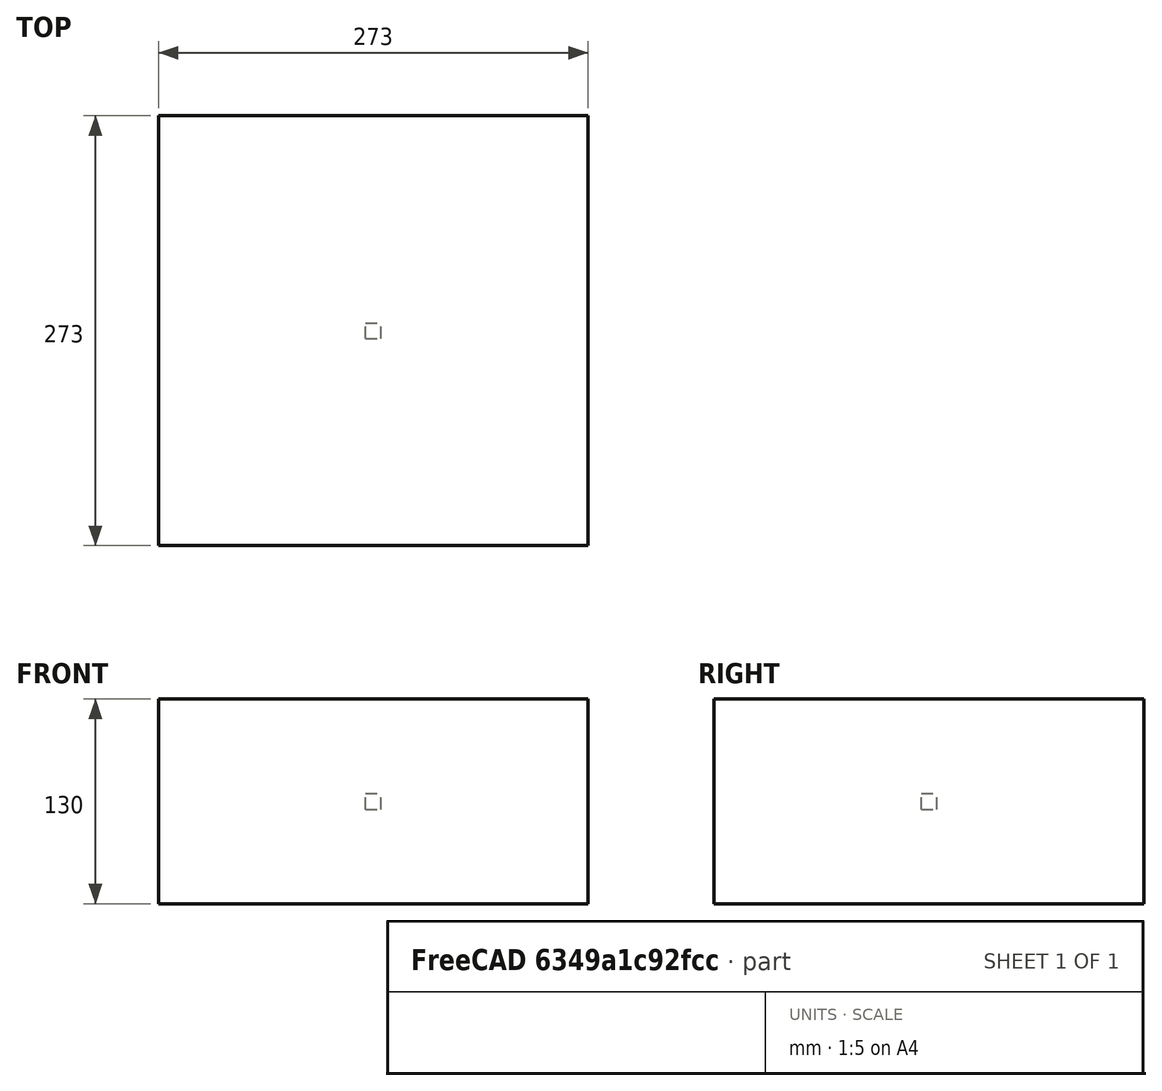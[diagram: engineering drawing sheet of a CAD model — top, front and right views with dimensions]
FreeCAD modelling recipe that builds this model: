
FCSTD DOCUMENT  (FreeCAD 1.0R39109 (Git))
Label: polarArray
License: All rights reserved
LicenseURL: http://en.wikipedia.org/wiki/All_rights_reserved
objects: App::DocumentObjectGroupPython×1251, Part::FeaturePython×3, App::Part×3
note: 2 computed .brp shape members not serialized (recipe doc carries the construction recipe); baked Part::Feature solids carry a one-line shape summary decoded from their .brp

FEATURE [App::DocumentObjectGroupPython] HALFPI  # scripted group (container) (typed FeaturePython)
  name = HALFPI
  value = pi/2.
FEATURE [App::DocumentObjectGroupPython] PI  # scripted group (container) (typed FeaturePython)
  name = PI
  value = 1.*pi
FEATURE [App::DocumentObjectGroupPython] TWOPI  # scripted group (container) (typed FeaturePython)
  name = TWOPI
  value = 2.*pi
FEATURE [App::DocumentObjectGroupPython] Constants  # scripted group (container) (typed FeaturePython)
  Group = -> [HALFPI,PI,TWOPI]
FEATURE [App::DocumentObjectGroupPython] Variables  # scripted group (container) (typed FeaturePython)
FEATURE [App::DocumentObjectGroupPython] Quantities  # scripted group (container) (typed FeaturePython)
FEATURE [App::DocumentObjectGroupPython] Isotopes  # scripted group (container) (typed FeaturePython)
FEATURE [App::DocumentObjectGroupPython] Elements  # scripted group (container) (typed FeaturePython)
FEATURE [App::DocumentObjectGroupPython] Matrix  # scripted group (container) (typed FeaturePython)
FEATURE [App::DocumentObjectGroupPython] Surfaces  # scripted group (container) (typed FeaturePython)
FEATURE [App::DocumentObjectGroupPython] Opticals  # scripted group (container) (typed FeaturePython)
  Group = -> [Matrix,Surfaces]
FEATURE [App::DocumentObjectGroupPython] G4Isotopes  # scripted group (container) (typed FeaturePython)
FEATURE [App::DocumentObjectGroupPython] H_element  # scripted group (container) (typed FeaturePython)
  Z = 1
  atom_value = 1.008
  formula = H
  name = H_element
FEATURE [App::DocumentObjectGroupPython] He_element  # scripted group (container) (typed FeaturePython)
  Z = 2
  atom_value = 4.0026
  formula = He
  name = He_element
FEATURE [App::DocumentObjectGroupPython] Li_element  # scripted group (container) (typed FeaturePython)
  Z = 3
  atom_value = 6.94
  formula = Li
  name = Li_element
FEATURE [App::DocumentObjectGroupPython] Be_element  # scripted group (container) (typed FeaturePython)
  Z = 4
  atom_value = 9.01218
  formula = Be
  name = Be_element
FEATURE [App::DocumentObjectGroupPython] B_element  # scripted group (container) (typed FeaturePython)
  Z = 5
  atom_value = 10.81
  formula = B
  name = B_element
FEATURE [App::DocumentObjectGroupPython] C_element  # scripted group (container) (typed FeaturePython)
  Z = 6
  atom_value = 12.011
  formula = C
  name = C_element
FEATURE [App::DocumentObjectGroupPython] N_element  # scripted group (container) (typed FeaturePython)
  Z = 7
  atom_value = 14.007
  formula = N
  name = N_element
FEATURE [App::DocumentObjectGroupPython] O_element  # scripted group (container) (typed FeaturePython)
  Z = 8
  atom_value = 15.999
  formula = O
  name = O_element
FEATURE [App::DocumentObjectGroupPython] F_element  # scripted group (container) (typed FeaturePython)
  Z = 9
  atom_value = 18.9984
  formula = F
  name = F_element
FEATURE [App::DocumentObjectGroupPython] Ne_element  # scripted group (container) (typed FeaturePython)
  Z = 10
  atom_value = 20.1797
  formula = Ne
  name = Ne_element
FEATURE [App::DocumentObjectGroupPython] Na_element  # scripted group (container) (typed FeaturePython)
  Z = 11
  atom_value = 22.9898
  formula = Na
  name = Na_element
FEATURE [App::DocumentObjectGroupPython] Mg_element  # scripted group (container) (typed FeaturePython)
  Z = 12
  atom_value = 24.305
  formula = Mg
  name = Mg_element
FEATURE [App::DocumentObjectGroupPython] Al_element  # scripted group (container) (typed FeaturePython)
  Z = 13
  atom_value = 26.9815
  formula = Al
  name = Al_element
FEATURE [App::DocumentObjectGroupPython] Si_element  # scripted group (container) (typed FeaturePython)
  Z = 14
  atom_value = 28.085
  formula = Si
  name = Si_element
FEATURE [App::DocumentObjectGroupPython] P_element  # scripted group (container) (typed FeaturePython)
  Z = 15
  atom_value = 30.9738
  formula = P
  name = P_element
FEATURE [App::DocumentObjectGroupPython] S_element  # scripted group (container) (typed FeaturePython)
  Z = 16
  atom_value = 32.06
  formula = S
  name = S_element
FEATURE [App::DocumentObjectGroupPython] Cl_element  # scripted group (container) (typed FeaturePython)
  Z = 17
  atom_value = 35.45
  formula = Cl
  name = Cl_element
FEATURE [App::DocumentObjectGroupPython] Ar_element  # scripted group (container) (typed FeaturePython)
  Z = 18
  atom_value = 39.95
  formula = Ar
  name = Ar_element
FEATURE [App::DocumentObjectGroupPython] K_element  # scripted group (container) (typed FeaturePython)
  Z = 19
  atom_value = 39.0983
  formula = K
  name = K_element
FEATURE [App::DocumentObjectGroupPython] Ca_element  # scripted group (container) (typed FeaturePython)
  Z = 20
  atom_value = 40.078
  formula = Ca
  name = Ca_element
FEATURE [App::DocumentObjectGroupPython] Sc_element  # scripted group (container) (typed FeaturePython)
  Z = 21
  atom_value = 44.9559
  formula = Sc
  name = Sc_element
FEATURE [App::DocumentObjectGroupPython] Ti_element  # scripted group (container) (typed FeaturePython)
  Z = 22
  atom_value = 47.867
  formula = Ti
  name = Ti_element
FEATURE [App::DocumentObjectGroupPython] V_element  # scripted group (container) (typed FeaturePython)
  Z = 23
  atom_value = 50.9415
  formula = V
  name = V_element
FEATURE [App::DocumentObjectGroupPython] Cr_element  # scripted group (container) (typed FeaturePython)
  Z = 24
  atom_value = 51.9961
  formula = Cr
  name = Cr_element
FEATURE [App::DocumentObjectGroupPython] Mn_element  # scripted group (container) (typed FeaturePython)
  Z = 25
  atom_value = 54.938
  formula = Mn
  name = Mn_element
FEATURE [App::DocumentObjectGroupPython] Fe_element  # scripted group (container) (typed FeaturePython)
  Z = 26
  atom_value = 55.845
  formula = Fe
  name = Fe_element
FEATURE [App::DocumentObjectGroupPython] Co_element  # scripted group (container) (typed FeaturePython)
  Z = 27
  atom_value = 58.9332
  formula = Co
  name = Co_element
FEATURE [App::DocumentObjectGroupPython] Ni_element  # scripted group (container) (typed FeaturePython)
  Z = 28
  atom_value = 58.6934
  formula = Ni
  name = Ni_element
FEATURE [App::DocumentObjectGroupPython] Cu_element  # scripted group (container) (typed FeaturePython)
  Z = 29
  atom_value = 63.546
  formula = Cu
  name = Cu_element
FEATURE [App::DocumentObjectGroupPython] Zn_element  # scripted group (container) (typed FeaturePython)
  Z = 30
  atom_value = 65.38
  formula = Zn
  name = Zn_element
FEATURE [App::DocumentObjectGroupPython] Ga_element  # scripted group (container) (typed FeaturePython)
  Z = 31
  atom_value = 69.723
  formula = Ga
  name = Ga_element
FEATURE [App::DocumentObjectGroupPython] Ge_element  # scripted group (container) (typed FeaturePython)
  Z = 32
  atom_value = 72.63
  formula = Ge
  name = Ge_element
FEATURE [App::DocumentObjectGroupPython] As_element  # scripted group (container) (typed FeaturePython)
  Z = 33
  atom_value = 74.9216
  formula = As
  name = As_element
FEATURE [App::DocumentObjectGroupPython] Se_element  # scripted group (container) (typed FeaturePython)
  Z = 34
  atom_value = 78.971
  formula = Se
  name = Se_element
FEATURE [App::DocumentObjectGroupPython] Br_element  # scripted group (container) (typed FeaturePython)
  Z = 35
  atom_value = 79.904
  formula = Br
  name = Br_element
FEATURE [App::DocumentObjectGroupPython] Kr_element  # scripted group (container) (typed FeaturePython)
  Z = 36
  atom_value = 83.798
  formula = Kr
  name = Kr_element
FEATURE [App::DocumentObjectGroupPython] Rb_element  # scripted group (container) (typed FeaturePython)
  Z = 37
  atom_value = 85.4678
  formula = Rb
  name = Rb_element
FEATURE [App::DocumentObjectGroupPython] Sr_element  # scripted group (container) (typed FeaturePython)
  Z = 38
  atom_value = 87.62
  formula = Sr
  name = Sr_element
FEATURE [App::DocumentObjectGroupPython] Y_element  # scripted group (container) (typed FeaturePython)
  Z = 39
  atom_value = 88.9058
  formula = Y
  name = Y_element
FEATURE [App::DocumentObjectGroupPython] Zr_element  # scripted group (container) (typed FeaturePython)
  Z = 40
  atom_value = 91.224
  formula = Zr
  name = Zr_element
FEATURE [App::DocumentObjectGroupPython] Nb_element  # scripted group (container) (typed FeaturePython)
  Z = 41
  atom_value = 92.9064
  formula = Nb
  name = Nb_element
FEATURE [App::DocumentObjectGroupPython] Mo_element  # scripted group (container) (typed FeaturePython)
  Z = 42
  atom_value = 95.95
  formula = Mo
  name = Mo_element
FEATURE [App::DocumentObjectGroupPython] Tc_element  # scripted group (container) (typed FeaturePython)
  Z = 43
  atom_value = 97
  formula = Tc
  name = Tc_element
FEATURE [App::DocumentObjectGroupPython] Ru_element  # scripted group (container) (typed FeaturePython)
  Z = 44
  atom_value = 101.07
  formula = Ru
  name = Ru_element
FEATURE [App::DocumentObjectGroupPython] Rh_element  # scripted group (container) (typed FeaturePython)
  Z = 45
  atom_value = 102.905
  formula = Rh
  name = Rh_element
FEATURE [App::DocumentObjectGroupPython] Pd_element  # scripted group (container) (typed FeaturePython)
  Z = 46
  atom_value = 106.42
  formula = Pd
  name = Pd_element
FEATURE [App::DocumentObjectGroupPython] Ag_element  # scripted group (container) (typed FeaturePython)
  Z = 47
  atom_value = 107.868
  formula = Ag
  name = Ag_element
FEATURE [App::DocumentObjectGroupPython] Cd_element  # scripted group (container) (typed FeaturePython)
  Z = 48
  atom_value = 112.414
  formula = Cd
  name = Cd_element
FEATURE [App::DocumentObjectGroupPython] In_element  # scripted group (container) (typed FeaturePython)
  Z = 49
  atom_value = 114.818
  formula = In
  name = In_element
FEATURE [App::DocumentObjectGroupPython] Sn_element  # scripted group (container) (typed FeaturePython)
  Z = 50
  atom_value = 118.71
  formula = Sn
  name = Sn_element
FEATURE [App::DocumentObjectGroupPython] Sb_element  # scripted group (container) (typed FeaturePython)
  Z = 51
  atom_value = 121.76
  formula = Sb
  name = Sb_element
FEATURE [App::DocumentObjectGroupPython] Te_element  # scripted group (container) (typed FeaturePython)
  Z = 52
  atom_value = 127.6
  formula = Te
  name = Te_element
FEATURE [App::DocumentObjectGroupPython] I_element  # scripted group (container) (typed FeaturePython)
  Z = 53
  atom_value = 126.904
  formula = I
  name = I_element
FEATURE [App::DocumentObjectGroupPython] Xe_element  # scripted group (container) (typed FeaturePython)
  Z = 54
  atom_value = 131.293
  formula = Xe
  name = Xe_element
FEATURE [App::DocumentObjectGroupPython] Cs_element  # scripted group (container) (typed FeaturePython)
  Z = 55
  atom_value = 132.905
  formula = Cs
  name = Cs_element
FEATURE [App::DocumentObjectGroupPython] Ba_element  # scripted group (container) (typed FeaturePython)
  Z = 56
  atom_value = 137.327
  formula = Ba
  name = Ba_element
FEATURE [App::DocumentObjectGroupPython] La_element  # scripted group (container) (typed FeaturePython)
  Z = 57
  atom_value = 138.905
  formula = La
  name = La_element
FEATURE [App::DocumentObjectGroupPython] Ce_element  # scripted group (container) (typed FeaturePython)
  Z = 58
  atom_value = 140.116
  formula = Ce
  name = Ce_element
FEATURE [App::DocumentObjectGroupPython] Pr_element  # scripted group (container) (typed FeaturePython)
  Z = 59
  atom_value = 140.908
  formula = Pr
  name = Pr_element
FEATURE [App::DocumentObjectGroupPython] Nd_element  # scripted group (container) (typed FeaturePython)
  Z = 60
  atom_value = 144.242
  formula = Nd
  name = Nd_element
FEATURE [App::DocumentObjectGroupPython] Pm_element  # scripted group (container) (typed FeaturePython)
  Z = 61
  atom_value = 145
  formula = Pm
  name = Pm_element
FEATURE [App::DocumentObjectGroupPython] Sm_element  # scripted group (container) (typed FeaturePython)
  Z = 62
  atom_value = 150.36
  formula = Sm
  name = Sm_element
FEATURE [App::DocumentObjectGroupPython] Eu_element  # scripted group (container) (typed FeaturePython)
  Z = 63
  atom_value = 151.964
  formula = Eu
  name = Eu_element
FEATURE [App::DocumentObjectGroupPython] Gd_element  # scripted group (container) (typed FeaturePython)
  Z = 64
  atom_value = 157.25
  formula = Gd
  name = Gd_element
FEATURE [App::DocumentObjectGroupPython] Tb_element  # scripted group (container) (typed FeaturePython)
  Z = 65
  atom_value = 158.925
  formula = Tb
  name = Tb_element
FEATURE [App::DocumentObjectGroupPython] Dy_element  # scripted group (container) (typed FeaturePython)
  Z = 66
  atom_value = 162.5
  formula = Dy
  name = Dy_element
FEATURE [App::DocumentObjectGroupPython] Ho_element  # scripted group (container) (typed FeaturePython)
  Z = 67
  atom_value = 164.93
  formula = Ho
  name = Ho_element
FEATURE [App::DocumentObjectGroupPython] Er_element  # scripted group (container) (typed FeaturePython)
  Z = 68
  atom_value = 167.259
  formula = Er
  name = Er_element
FEATURE [App::DocumentObjectGroupPython] Tm_element  # scripted group (container) (typed FeaturePython)
  Z = 69
  atom_value = 168.934
  formula = Tm
  name = Tm_element
FEATURE [App::DocumentObjectGroupPython] Yb_element  # scripted group (container) (typed FeaturePython)
  Z = 70
  atom_value = 173.045
  formula = Yb
  name = Yb_element
FEATURE [App::DocumentObjectGroupPython] Lu_element  # scripted group (container) (typed FeaturePython)
  Z = 71
  atom_value = 174.967
  formula = Lu
  name = Lu_element
FEATURE [App::DocumentObjectGroupPython] Hf_element  # scripted group (container) (typed FeaturePython)
  Z = 72
  atom_value = 178.49
  formula = Hf
  name = Hf_element
FEATURE [App::DocumentObjectGroupPython] Ta_element  # scripted group (container) (typed FeaturePython)
  Z = 73
  atom_value = 180.948
  formula = Ta
  name = Ta_element
FEATURE [App::DocumentObjectGroupPython] W_element  # scripted group (container) (typed FeaturePython)
  Z = 74
  atom_value = 183.84
  formula = W
  name = W_element
FEATURE [App::DocumentObjectGroupPython] Re_element  # scripted group (container) (typed FeaturePython)
  Z = 75
  atom_value = 186.207
  formula = Re
  name = Re_element
FEATURE [App::DocumentObjectGroupPython] Os_element  # scripted group (container) (typed FeaturePython)
  Z = 76
  atom_value = 190.23
  formula = Os
  name = Os_element
FEATURE [App::DocumentObjectGroupPython] Ir_element  # scripted group (container) (typed FeaturePython)
  Z = 77
  atom_value = 192.217
  formula = Ir
  name = Ir_element
FEATURE [App::DocumentObjectGroupPython] Pt_element  # scripted group (container) (typed FeaturePython)
  Z = 78
  atom_value = 195.084
  formula = Pt
  name = Pt_element
FEATURE [App::DocumentObjectGroupPython] Au_element  # scripted group (container) (typed FeaturePython)
  Z = 79
  atom_value = 196.967
  formula = Au
  name = Au_element
FEATURE [App::DocumentObjectGroupPython] Hg_element  # scripted group (container) (typed FeaturePython)
  Z = 80
  atom_value = 200.592
  formula = Hg
  name = Hg_element
FEATURE [App::DocumentObjectGroupPython] Tl_element  # scripted group (container) (typed FeaturePython)
  Z = 81
  atom_value = 204.38
  formula = Tl
  name = Tl_element
FEATURE [App::DocumentObjectGroupPython] Pb_element  # scripted group (container) (typed FeaturePython)
  Z = 82
  atom_value = 207.2
  formula = Pb
  name = Pb_element
FEATURE [App::DocumentObjectGroupPython] Bi_element  # scripted group (container) (typed FeaturePython)
  Z = 83
  atom_value = 208.98
  formula = Bi
  name = Bi_element
FEATURE [App::DocumentObjectGroupPython] Po_element  # scripted group (container) (typed FeaturePython)
  Z = 84
  atom_value = 209
  formula = Po
  name = Po_element
FEATURE [App::DocumentObjectGroupPython] At_element  # scripted group (container) (typed FeaturePython)
  Z = 85
  atom_value = 210
  formula = At
  name = At_element
FEATURE [App::DocumentObjectGroupPython] Rn_element  # scripted group (container) (typed FeaturePython)
  Z = 86
  atom_value = 222
  formula = Rn
  name = Rn_element
FEATURE [App::DocumentObjectGroupPython] Fr_element  # scripted group (container) (typed FeaturePython)
  Z = 87
  atom_value = 223
  formula = Fr
  name = Fr_element
FEATURE [App::DocumentObjectGroupPython] Ra_element  # scripted group (container) (typed FeaturePython)
  Z = 88
  atom_value = 226
  formula = Ra
  name = Ra_element
FEATURE [App::DocumentObjectGroupPython] Ac_element  # scripted group (container) (typed FeaturePython)
  Z = 89
  atom_value = 227
  formula = Ac
  name = Ac_element
FEATURE [App::DocumentObjectGroupPython] Th_element  # scripted group (container) (typed FeaturePython)
  Z = 90
  atom_value = 232.038
  formula = Th
  name = Th_element
FEATURE [App::DocumentObjectGroupPython] Pa_element  # scripted group (container) (typed FeaturePython)
  Z = 91
  atom_value = 231.036
  formula = Pa
  name = Pa_element
FEATURE [App::DocumentObjectGroupPython] U_element  # scripted group (container) (typed FeaturePython)
  Z = 92
  atom_value = 238.029
  formula = U
  name = U_element
FEATURE [App::DocumentObjectGroupPython] Np_element  # scripted group (container) (typed FeaturePython)
  Z = 93
  atom_value = 237
  formula = Np
  name = Np_element
FEATURE [App::DocumentObjectGroupPython] Pu_element  # scripted group (container) (typed FeaturePython)
  Z = 94
  atom_value = 244
  formula = Pu
  name = Pu_element
FEATURE [App::DocumentObjectGroupPython] Am_element  # scripted group (container) (typed FeaturePython)
  Z = 95
  atom_value = 243
  formula = Am
  name = Am_element
FEATURE [App::DocumentObjectGroupPython] Cm_element  # scripted group (container) (typed FeaturePython)
  Z = 96
  atom_value = 247
  formula = Cm
  name = Cm_element
FEATURE [App::DocumentObjectGroupPython] Bk_element  # scripted group (container) (typed FeaturePython)
  Z = 97
  atom_value = 247
  formula = Bk
  name = Bk_element
FEATURE [App::DocumentObjectGroupPython] Cf_element  # scripted group (container) (typed FeaturePython)
  Z = 98
  atom_value = 251
  formula = Cf
  name = Cf_element
FEATURE [App::DocumentObjectGroupPython] G4Elements  # scripted group (container) (typed FeaturePython)
  Group = -> [H_element,He_element,Li_element,Be_element,B_element,C_element,N_element,O_element,F_element,Ne_element,Na_element,Mg_element,Al_element,Si_element,P_element,S_element,Cl_element,Ar_element,K_element,Ca_element,Sc_element,Ti_element,V_element,Cr_element,Mn_element,Fe_element,Co_element,Ni_element,Cu_element,Zn_element,Ga_element,Ge_element,As_element,Se_element,Br_element,Kr_element,Rb_element,+61 more]
FEATURE [App::DocumentObjectGroupPython] H_element001  label="H_element : 0.101"  # scripted group (container) (typed FeaturePython)
  n = 0.101327
FEATURE [App::DocumentObjectGroupPython] C_element001  label="C_element : 0.775"  # scripted group (container) (typed FeaturePython)
  n = 0.7755
FEATURE [App::DocumentObjectGroupPython] N_element001  label="N_element : 0.035"  # scripted group (container) (typed FeaturePython)
  n = 0.035057
FEATURE [App::DocumentObjectGroupPython] O_element001  label="O_element : 0.052"  # scripted group (container) (typed FeaturePython)
  n = 0.0523159
FEATURE [App::DocumentObjectGroupPython] F_element001  label="F_element : 0.017"  # scripted group (container) (typed FeaturePython)
  n = 0.017422
FEATURE [App::DocumentObjectGroupPython] Ca_element001  label="Ca_element : 0.018"  # scripted group (container) (typed FeaturePython)
  n = 0.018378
FEATURE [App::DocumentObjectGroupPython] G4_A_150_TISSUE  label="G4_A-150_TISSUE"  # scripted group (container) (typed FeaturePython)
  Dunit = g/cm3
  Dvalue = 1.127
  Group = -> [H_element001,C_element001,N_element001,O_element001,F_element001,Ca_element001]
  conduct = 2
  density = 1
  expand = 3
  formula = G4_A-150_TISSUE
  name = G4_A-150_TISSUE
  specific = 4
FEATURE [App::DocumentObjectGroupPython] C_element002  label="C_element : 3"  # scripted group (container) (typed FeaturePython)
  n = 3
  ref = C_element
FEATURE [App::DocumentObjectGroupPython] H_element002  label="H_element : 6"  # scripted group (container) (typed FeaturePython)
  n = 6
  ref = H_element
FEATURE [App::DocumentObjectGroupPython] O_element002  label="O_element : 1"  # scripted group (container) (typed FeaturePython)
  n = 1
  ref = O_element
FEATURE [App::DocumentObjectGroupPython] G4_ACETONE  # scripted group (container) (typed FeaturePython)
  Dunit = g/cm3
  Dvalue = 0.7899
  Group = -> [C_element002,H_element002,O_element002]
  conduct = 2
  density = 1
  expand = 3
  formula = G4_ACETONE
  name = G4_ACETONE
  specific = 4
FEATURE [App::DocumentObjectGroupPython] C_element003  label="C_element : 2"  # scripted group (container) (typed FeaturePython)
  n = 2
  ref = C_element
FEATURE [App::DocumentObjectGroupPython] H_element003  label="H_element : 2"  # scripted group (container) (typed FeaturePython)
  n = 2
  ref = H_element
FEATURE [App::DocumentObjectGroupPython] G4_ACETYLENE  # scripted group (container) (typed FeaturePython)
  Dunit = g/cm3
  Dvalue = 0.0010967
  Group = -> [C_element003,H_element003]
  conduct = 2
  density = 1
  expand = 3
  formula = G4_ACETYLENE
  name = G4_ACETYLENE
  specific = 4
FEATURE [App::DocumentObjectGroupPython] C_element004  label="C_element : 5"  # scripted group (container) (typed FeaturePython)
  n = 5
  ref = C_element
FEATURE [App::DocumentObjectGroupPython] H_element004  label="H_element : 5"  # scripted group (container) (typed FeaturePython)
  n = 5
  ref = H_element
FEATURE [App::DocumentObjectGroupPython] N_element002  label="N_element : 5"  # scripted group (container) (typed FeaturePython)
  n = 5
  ref = N_element
FEATURE [App::DocumentObjectGroupPython] G4_ADENINE  # scripted group (container) (typed FeaturePython)
  Dunit = g/cm3
  Dvalue = 1.6
  Group = -> [C_element004,H_element004,N_element002]
  conduct = 2
  density = 1
  expand = 3
  formula = G4_ADENINE
  name = G4_ADENINE
  specific = 4
FEATURE [App::DocumentObjectGroupPython] H_element005  label="H_element : 0.114"  # scripted group (container) (typed FeaturePython)
  n = 0.114
FEATURE [App::DocumentObjectGroupPython] C_element005  label="C_element : 0.598"  # scripted group (container) (typed FeaturePython)
  n = 0.598
FEATURE [App::DocumentObjectGroupPython] N_element003  label="N_element : 0.007"  # scripted group (container) (typed FeaturePython)
  n = 0.007
FEATURE [App::DocumentObjectGroupPython] O_element003  label="O_element : 0.278"  # scripted group (container) (typed FeaturePython)
  n = 0.278
FEATURE [App::DocumentObjectGroupPython] Na_element001  label="Na_element : 0.001"  # scripted group (container) (typed FeaturePython)
  n = 0.001
FEATURE [App::DocumentObjectGroupPython] S_element001  label="S_element : 0.001"  # scripted group (container) (typed FeaturePython)
  n = 0.001
FEATURE [App::DocumentObjectGroupPython] Cl_element001  label="Cl_element : 0.001"  # scripted group (container) (typed FeaturePython)
  n = 0.001
FEATURE [App::DocumentObjectGroupPython] G4_ADIPOSE_TISSUE_ICRP  # scripted group (container) (typed FeaturePython)
  Dunit = g/cm3
  Dvalue = 0.95
  Group = -> [H_element005,C_element005,N_element003,O_element003,Na_element001,S_element001,Cl_element001]
  conduct = 2
  density = 1
  expand = 3
  formula = G4_ADIPOSE_TISSUE_ICRP
  name = G4_ADIPOSE_TISSUE_ICRP
  specific = 4
FEATURE [App::DocumentObjectGroupPython] C_element006  label="C_element : 0.000"  # scripted group (container) (typed FeaturePython)
  n = 0.000124
FEATURE [App::DocumentObjectGroupPython] N_element004  label="N_element : 0.755"  # scripted group (container) (typed FeaturePython)
  n = 0.755268
FEATURE [App::DocumentObjectGroupPython] O_element004  label="O_element : 0.232"  # scripted group (container) (typed FeaturePython)
  n = 0.231781
FEATURE [App::DocumentObjectGroupPython] Ar_element001  label="Ar_element : 0.013"  # scripted group (container) (typed FeaturePython)
  n = 0.012827
FEATURE [App::DocumentObjectGroupPython] G4_AIR  # scripted group (container) (typed FeaturePython)
  Dunit = g/cm3
  Dvalue = 0.00120479
  Group = -> [C_element006,N_element004,O_element004,Ar_element001]
  conduct = 2
  density = 1
  expand = 3
  formula = G4_AIR
  name = G4_AIR
  specific = 4
FEATURE [App::DocumentObjectGroupPython] C_element007  label="C_element : 006"  # scripted group (container) (typed FeaturePython)
  n = 3
  ref = C_element
FEATURE [App::DocumentObjectGroupPython] H_element006  label="H_element : 7"  # scripted group (container) (typed FeaturePython)
  n = 7
  ref = H_element
FEATURE [App::DocumentObjectGroupPython] N_element005  label="N_element : 1"  # scripted group (container) (typed FeaturePython)
  n = 1
  ref = N_element
FEATURE [App::DocumentObjectGroupPython] O_element005  label="O_element : 2"  # scripted group (container) (typed FeaturePython)
  n = 2
  ref = O_element
FEATURE [App::DocumentObjectGroupPython] G4_ALANINE  # scripted group (container) (typed FeaturePython)
  Dunit = g/cm3
  Dvalue = 1.42
  Group = -> [C_element007,H_element006,N_element005,O_element005]
  conduct = 2
  density = 1
  expand = 3
  formula = G4_ALANINE
  name = G4_ALANINE
  specific = 4
FEATURE [App::DocumentObjectGroupPython] Al_element001  label="Al_element : 2"  # scripted group (container) (typed FeaturePython)
  n = 2
  ref = Al_element
FEATURE [App::DocumentObjectGroupPython] O_element006  label="O_element : 3"  # scripted group (container) (typed FeaturePython)
  n = 3
  ref = O_element
FEATURE [App::DocumentObjectGroupPython] G4_ALUMINUM_OXIDE  # scripted group (container) (typed FeaturePython)
  Dunit = g/cm3
  Dvalue = 3.97
  Group = -> [Al_element001,O_element006]
  conduct = 2
  density = 1
  expand = 3
  formula = G4_ALUMINUM_OXIDE
  name = G4_ALUMINUM_OXIDE
  specific = 4
FEATURE [App::DocumentObjectGroupPython] H_element007  label="H_element : 0.106"  # scripted group (container) (typed FeaturePython)
  n = 0.10593
FEATURE [App::DocumentObjectGroupPython] C_element008  label="C_element : 0.789"  # scripted group (container) (typed FeaturePython)
  n = 0.788974
FEATURE [App::DocumentObjectGroupPython] O_element007  label="O_element : 0.105"  # scripted group (container) (typed FeaturePython)
  n = 0.105096
FEATURE [App::DocumentObjectGroupPython] G4_AMBER  # scripted group (container) (typed FeaturePython)
  Dunit = g/cm3
  Dvalue = 1.1
  Group = -> [H_element007,C_element008,O_element007]
  conduct = 2
  density = 1
  expand = 3
  formula = G4_AMBER
  name = G4_AMBER
  specific = 4
FEATURE [App::DocumentObjectGroupPython] N_element006  label="N_element : 006"  # scripted group (container) (typed FeaturePython)
  n = 1
  ref = N_element
FEATURE [App::DocumentObjectGroupPython] H_element008  label="H_element : 3"  # scripted group (container) (typed FeaturePython)
  n = 3
  ref = H_element
FEATURE [App::DocumentObjectGroupPython] G4_AMMONIA  # scripted group (container) (typed FeaturePython)
  Dunit = g/cm3
  Dvalue = 0.000826019
  Group = -> [N_element006,H_element008]
  conduct = 2
  density = 1
  expand = 3
  formula = G4_AMMONIA
  name = G4_AMMONIA
  specific = 4
FEATURE [App::DocumentObjectGroupPython] C_element009  label="C_element : 6"  # scripted group (container) (typed FeaturePython)
  n = 6
  ref = C_element
FEATURE [App::DocumentObjectGroupPython] H_element009  label="H_element : 008"  # scripted group (container) (typed FeaturePython)
  n = 7
  ref = H_element
FEATURE [App::DocumentObjectGroupPython] N_element007  label="N_element : 007"  # scripted group (container) (typed FeaturePython)
  n = 1
  ref = N_element
FEATURE [App::DocumentObjectGroupPython] G4_ANILINE  # scripted group (container) (typed FeaturePython)
  Dunit = g/cm3
  Dvalue = 1.0235
  Group = -> [C_element009,H_element009,N_element007]
  conduct = 2
  density = 1
  expand = 3
  formula = G4_ANILINE
  name = G4_ANILINE
  specific = 4
FEATURE [App::DocumentObjectGroupPython] C_element010  label="C_element : 14"  # scripted group (container) (typed FeaturePython)
  n = 14
  ref = C_element
FEATURE [App::DocumentObjectGroupPython] H_element010  label="H_element : 10"  # scripted group (container) (typed FeaturePython)
  n = 10
  ref = H_element
FEATURE [App::DocumentObjectGroupPython] G4_ANTHRACENE  # scripted group (container) (typed FeaturePython)
  Dunit = g/cm3
  Dvalue = 1.283
  Group = -> [C_element010,H_element010]
  conduct = 2
  density = 1
  expand = 3
  formula = G4_ANTHRACENE
  name = G4_ANTHRACENE
  specific = 4
FEATURE [App::DocumentObjectGroupPython] H_element011  label="H_element : 0.065"  # scripted group (container) (typed FeaturePython)
  n = 0.0654709
FEATURE [App::DocumentObjectGroupPython] C_element011  label="C_element : 0.537"  # scripted group (container) (typed FeaturePython)
  n = 0.536944
FEATURE [App::DocumentObjectGroupPython] N_element008  label="N_element : 0.021"  # scripted group (container) (typed FeaturePython)
  n = 0.0215
FEATURE [App::DocumentObjectGroupPython] O_element008  label="O_element : 0.032"  # scripted group (container) (typed FeaturePython)
  n = 0.032085
FEATURE [App::DocumentObjectGroupPython] F_element002  label="F_element : 0.167"  # scripted group (container) (typed FeaturePython)
  n = 0.167411
FEATURE [App::DocumentObjectGroupPython] Ca_element002  label="Ca_element : 0.177"  # scripted group (container) (typed FeaturePython)
  n = 0.176589
FEATURE [App::DocumentObjectGroupPython] G4_B_100_BONE  label="G4_B-100_BONE"  # scripted group (container) (typed FeaturePython)
  Dunit = g/cm3
  Dvalue = 1.45
  Group = -> [H_element011,C_element011,N_element008,O_element008,F_element002,Ca_element002]
  conduct = 2
  density = 1
  expand = 3
  formula = G4_B-100_BONE
  name = G4_B-100_BONE
  specific = 4
FEATURE [App::DocumentObjectGroupPython] H_element012  label="H_element : 0.057"  # scripted group (container) (typed FeaturePython)
  n = 0.057441
FEATURE [App::DocumentObjectGroupPython] C_element012  label="C_element : 0.790"  # scripted group (container) (typed FeaturePython)
  n = 0.774591
FEATURE [App::DocumentObjectGroupPython] O_element009  label="O_element : 0.168"  # scripted group (container) (typed FeaturePython)
  n = 0.167968
FEATURE [App::DocumentObjectGroupPython] G4_BAKELITE  # scripted group (container) (typed FeaturePython)
  Dunit = g/cm3
  Dvalue = 1.25
  Group = -> [H_element012,C_element012,O_element009]
  conduct = 2
  density = 1
  expand = 3
  formula = G4_BAKELITE
  name = G4_BAKELITE
  specific = 4
FEATURE [App::DocumentObjectGroupPython] Ba_element001  label="Ba_element : 1"  # scripted group (container) (typed FeaturePython)
  n = 1
  ref = Ba_element
FEATURE [App::DocumentObjectGroupPython] F_element003  label="F_element : 2"  # scripted group (container) (typed FeaturePython)
  n = 2
  ref = F_element
FEATURE [App::DocumentObjectGroupPython] G4_BARIUM_FLUORIDE  # scripted group (container) (typed FeaturePython)
  Dunit = g/cm3
  Dvalue = 4.89
  Group = -> [Ba_element001,F_element003]
  conduct = 2
  density = 1
  expand = 3
  formula = G4_BARIUM_FLUORIDE
  name = G4_BARIUM_FLUORIDE
  specific = 4
FEATURE [App::DocumentObjectGroupPython] Ba_element002  label="Ba_element : 002"  # scripted group (container) (typed FeaturePython)
  n = 1
  ref = Ba_element
FEATURE [App::DocumentObjectGroupPython] S_element002  label="S_element : 1"  # scripted group (container) (typed FeaturePython)
  n = 1
  ref = S_element
FEATURE [App::DocumentObjectGroupPython] O_element010  label="O_element : 4"  # scripted group (container) (typed FeaturePython)
  n = 4
  ref = O_element
FEATURE [App::DocumentObjectGroupPython] G4_BARIUM_SULFATE  # scripted group (container) (typed FeaturePython)
  Dunit = g/cm3
  Dvalue = 4.5
  Group = -> [Ba_element002,S_element002,O_element010]
  conduct = 2
  density = 1
  expand = 3
  formula = G4_BARIUM_SULFATE
  name = G4_BARIUM_SULFATE
  specific = 4
FEATURE [App::DocumentObjectGroupPython] C_element013  label="C_element : 007"  # scripted group (container) (typed FeaturePython)
  n = 6
  ref = C_element
FEATURE [App::DocumentObjectGroupPython] H_element013  label="H_element : 009"  # scripted group (container) (typed FeaturePython)
  n = 6
  ref = H_element
FEATURE [App::DocumentObjectGroupPython] G4_BENZENE  # scripted group (container) (typed FeaturePython)
  Dunit = g/cm3
  Dvalue = 0.87865
  Group = -> [C_element013,H_element013]
  conduct = 2
  density = 1
  expand = 3
  formula = G4_BENZENE
  name = G4_BENZENE
  specific = 4
FEATURE [App::DocumentObjectGroupPython] Be_element001  label="Be_element : 1"  # scripted group (container) (typed FeaturePython)
  n = 1
  ref = Be_element
FEATURE [App::DocumentObjectGroupPython] O_element011  label="O_element : 005"  # scripted group (container) (typed FeaturePython)
  n = 1
  ref = O_element
FEATURE [App::DocumentObjectGroupPython] G4_BERYLLIUM_OXIDE  # scripted group (container) (typed FeaturePython)
  Dunit = g/cm3
  Dvalue = 3.01
  Group = -> [Be_element001,O_element011]
  conduct = 2
  density = 1
  expand = 3
  formula = G4_BERYLLIUM_OXIDE
  name = G4_BERYLLIUM_OXIDE
  specific = 4
FEATURE [App::DocumentObjectGroupPython] Bi_element001  label="Bi_element : 4"  # scripted group (container) (typed FeaturePython)
  n = 4
  ref = Bi_element
FEATURE [App::DocumentObjectGroupPython] Ge_element001  label="Ge_element : 3"  # scripted group (container) (typed FeaturePython)
  n = 3
  ref = Ge_element
FEATURE [App::DocumentObjectGroupPython] O_element012  label="O_element : 12"  # scripted group (container) (typed FeaturePython)
  n = 12
  ref = O_element
FEATURE [App::DocumentObjectGroupPython] G4_BGO  # scripted group (container) (typed FeaturePython)
  Dunit = g/cm3
  Dvalue = 7.13
  Group = -> [Bi_element001,Ge_element001,O_element012]
  conduct = 2
  density = 1
  expand = 3
  formula = G4_BGO
  name = G4_BGO
  specific = 4
FEATURE [App::DocumentObjectGroupPython] H_element014  label="H_element : 0.102"  # scripted group (container) (typed FeaturePython)
  n = 0.102
FEATURE [App::DocumentObjectGroupPython] C_element014  label="C_element : 0.110"  # scripted group (container) (typed FeaturePython)
  n = 0.11
FEATURE [App::DocumentObjectGroupPython] N_element009  label="N_element : 0.033"  # scripted group (container) (typed FeaturePython)
  n = 0.033
FEATURE [App::DocumentObjectGroupPython] O_element013  label="O_element : 0.745"  # scripted group (container) (typed FeaturePython)
  n = 0.745
FEATURE [App::DocumentObjectGroupPython] Na_element002  label="Na_element : 0.002"  # scripted group (container) (typed FeaturePython)
  n = 0.001
FEATURE [App::DocumentObjectGroupPython] P_element001  label="P_element : 0.001"  # scripted group (container) (typed FeaturePython)
  n = 0.001
FEATURE [App::DocumentObjectGroupPython] S_element003  label="S_element : 0.002"  # scripted group (container) (typed FeaturePython)
  n = 0.002
FEATURE [App::DocumentObjectGroupPython] Cl_element002  label="Cl_element : 0.003"  # scripted group (container) (typed FeaturePython)
  n = 0.003
FEATURE [App::DocumentObjectGroupPython] K_element001  label="K_element : 0.002"  # scripted group (container) (typed FeaturePython)
  n = 0.002
FEATURE [App::DocumentObjectGroupPython] Fe_element001  label="Fe_element : 0.001"  # scripted group (container) (typed FeaturePython)
  n = 0.001
FEATURE [App::DocumentObjectGroupPython] G4_BLOOD_ICRP  # scripted group (container) (typed FeaturePython)
  Dunit = g/cm3
  Dvalue = 1.06
  Group = -> [H_element014,C_element014,N_element009,O_element013,Na_element002,P_element001,S_element003,Cl_element002,K_element001,Fe_element001]
  conduct = 2
  density = 1
  expand = 3
  formula = G4_BLOOD_ICRP
  name = G4_BLOOD_ICRP
  specific = 4
FEATURE [App::DocumentObjectGroupPython] H_element015  label="H_element : 0.064"  # scripted group (container) (typed FeaturePython)
  n = 0.064
FEATURE [App::DocumentObjectGroupPython] C_element015  label="C_element : 0.278"  # scripted group (container) (typed FeaturePython)
  n = 0.278
FEATURE [App::DocumentObjectGroupPython] N_element010  label="N_element : 0.027"  # scripted group (container) (typed FeaturePython)
  n = 0.027
FEATURE [App::DocumentObjectGroupPython] O_element014  label="O_element : 0.410"  # scripted group (container) (typed FeaturePython)
  n = 0.41
FEATURE [App::DocumentObjectGroupPython] Mg_element001  label="Mg_element : 0.002"  # scripted group (container) (typed FeaturePython)
  n = 0.002
FEATURE [App::DocumentObjectGroupPython] P_element002  label="P_element : 0.070"  # scripted group (container) (typed FeaturePython)
  n = 0.07
FEATURE [App::DocumentObjectGroupPython] S_element004  label="S_element : 0.003"  # scripted group (container) (typed FeaturePython)
  n = 0.002
FEATURE [App::DocumentObjectGroupPython] Ca_element003  label="Ca_element : 0.147"  # scripted group (container) (typed FeaturePython)
  n = 0.147
FEATURE [App::DocumentObjectGroupPython] G4_BONE_COMPACT_ICRU  # scripted group (container) (typed FeaturePython)
  Dunit = g/cm3
  Dvalue = 1.85
  Group = -> [H_element015,C_element015,N_element010,O_element014,Mg_element001,P_element002,S_element004,Ca_element003]
  conduct = 2
  density = 1
  expand = 3
  formula = G4_BONE_COMPACT_ICRU
  name = G4_BONE_COMPACT_ICRU
  specific = 4
FEATURE [App::DocumentObjectGroupPython] H_element016  label="H_element : 0.034"  # scripted group (container) (typed FeaturePython)
  n = 0.034
FEATURE [App::DocumentObjectGroupPython] C_element016  label="C_element : 0.155"  # scripted group (container) (typed FeaturePython)
  n = 0.155
FEATURE [App::DocumentObjectGroupPython] N_element011  label="N_element : 0.042"  # scripted group (container) (typed FeaturePython)
  n = 0.042
FEATURE [App::DocumentObjectGroupPython] O_element015  label="O_element : 0.435"  # scripted group (container) (typed FeaturePython)
  n = 0.435
FEATURE [App::DocumentObjectGroupPython] Na_element003  label="Na_element : 0.003"  # scripted group (container) (typed FeaturePython)
  n = 0.001
FEATURE [App::DocumentObjectGroupPython] Mg_element002  label="Mg_element : 0.003"  # scripted group (container) (typed FeaturePython)
  n = 0.002
FEATURE [App::DocumentObjectGroupPython] P_element003  label="P_element : 0.103"  # scripted group (container) (typed FeaturePython)
  n = 0.103
FEATURE [App::DocumentObjectGroupPython] S_element005  label="S_element : 0.004"  # scripted group (container) (typed FeaturePython)
  n = 0.003
FEATURE [App::DocumentObjectGroupPython] Ca_element004  label="Ca_element : 0.225"  # scripted group (container) (typed FeaturePython)
  n = 0.225
FEATURE [App::DocumentObjectGroupPython] G4_BONE_CORTICAL_ICRP  # scripted group (container) (typed FeaturePython)
  Dunit = g/cm3
  Dvalue = 1.92
  Group = -> [H_element016,C_element016,N_element011,O_element015,Na_element003,Mg_element002,P_element003,S_element005,Ca_element004]
  conduct = 2
  density = 1
  expand = 3
  formula = G4_BONE_CORTICAL_ICRP
  name = G4_BONE_CORTICAL_ICRP
  specific = 4
FEATURE [App::DocumentObjectGroupPython] B_element001  label="B_element : 4"  # scripted group (container) (typed FeaturePython)
  n = 4
  ref = B_element
FEATURE [App::DocumentObjectGroupPython] C_element017  label="C_element : 1"  # scripted group (container) (typed FeaturePython)
  n = 1
  ref = C_element
FEATURE [App::DocumentObjectGroupPython] G4_BORON_CARBIDE  # scripted group (container) (typed FeaturePython)
  Dunit = g/cm3
  Dvalue = 2.52
  Group = -> [B_element001,C_element017]
  conduct = 2
  density = 1
  expand = 3
  formula = G4_BORON_CARBIDE
  name = G4_BORON_CARBIDE
  specific = 4
FEATURE [App::DocumentObjectGroupPython] B_element002  label="B_element : 2"  # scripted group (container) (typed FeaturePython)
  n = 2
  ref = B_element
FEATURE [App::DocumentObjectGroupPython] O_element016  label="O_element : 006"  # scripted group (container) (typed FeaturePython)
  n = 3
  ref = O_element
FEATURE [App::DocumentObjectGroupPython] G4_BORON_OXIDE  # scripted group (container) (typed FeaturePython)
  Dunit = g/cm3
  Dvalue = 1.812
  Group = -> [B_element002,O_element016]
  conduct = 2
  density = 1
  expand = 3
  formula = G4_BORON_OXIDE
  name = G4_BORON_OXIDE
  specific = 4
FEATURE [App::DocumentObjectGroupPython] H_element017  label="H_element : 0.107"  # scripted group (container) (typed FeaturePython)
  n = 0.107
FEATURE [App::DocumentObjectGroupPython] C_element018  label="C_element : 0.145"  # scripted group (container) (typed FeaturePython)
  n = 0.145
FEATURE [App::DocumentObjectGroupPython] N_element012  label="N_element : 0.022"  # scripted group (container) (typed FeaturePython)
  n = 0.022
FEATURE [App::DocumentObjectGroupPython] O_element017  label="O_element : 0.712"  # scripted group (container) (typed FeaturePython)
  n = 0.712
FEATURE [App::DocumentObjectGroupPython] Na_element004  label="Na_element : 0.004"  # scripted group (container) (typed FeaturePython)
  n = 0.002
FEATURE [App::DocumentObjectGroupPython] P_element004  label="P_element : 0.004"  # scripted group (container) (typed FeaturePython)
  n = 0.004
FEATURE [App::DocumentObjectGroupPython] S_element006  label="S_element : 0.005"  # scripted group (container) (typed FeaturePython)
  n = 0.002
FEATURE [App::DocumentObjectGroupPython] Cl_element003  label="Cl_element : 0.004"  # scripted group (container) (typed FeaturePython)
  n = 0.003
FEATURE [App::DocumentObjectGroupPython] K_element002  label="K_element : 0.003"  # scripted group (container) (typed FeaturePython)
  n = 0.003
FEATURE [App::DocumentObjectGroupPython] G4_BRAIN_ICRP  # scripted group (container) (typed FeaturePython)
  Dunit = g/cm3
  Dvalue = 1.04
  Group = -> [H_element017,C_element018,N_element012,O_element017,Na_element004,P_element004,S_element006,Cl_element003,K_element002]
  conduct = 2
  density = 1
  expand = 3
  formula = G4_BRAIN_ICRP
  name = G4_BRAIN_ICRP
  specific = 4
FEATURE [App::DocumentObjectGroupPython] C_element019  label="C_element : 4"  # scripted group (container) (typed FeaturePython)
  n = 4
  ref = C_element
FEATURE [App::DocumentObjectGroupPython] H_element018  label="H_element : 010"  # scripted group (container) (typed FeaturePython)
  n = 10
  ref = H_element
FEATURE [App::DocumentObjectGroupPython] G4_BUTANE  # scripted group (container) (typed FeaturePython)
  Dunit = g/cm3
  Dvalue = 0.00249343
  Group = -> [C_element019,H_element018]
  conduct = 2
  density = 1
  expand = 3
  formula = G4_BUTANE
  name = G4_BUTANE
  specific = 4
FEATURE [App::DocumentObjectGroupPython] C_element020  label="C_element : 008"  # scripted group (container) (typed FeaturePython)
  n = 4
  ref = C_element
FEATURE [App::DocumentObjectGroupPython] H_element019  label="H_element : 011"  # scripted group (container) (typed FeaturePython)
  n = 10
  ref = H_element
FEATURE [App::DocumentObjectGroupPython] O_element018  label="O_element : 007"  # scripted group (container) (typed FeaturePython)
  n = 1
  ref = O_element
FEATURE [App::DocumentObjectGroupPython] G4_N_BUTYL_ALCOHOL  label="G4_N-BUTYL_ALCOHOL"  # scripted group (container) (typed FeaturePython)
  Dunit = g/cm3
  Dvalue = 0.8098
  Group = -> [C_element020,H_element019,O_element018]
  conduct = 2
  density = 1
  expand = 3
  formula = G4_N-BUTYL_ALCOHOL
  name = G4_N-BUTYL_ALCOHOL
  specific = 4
FEATURE [App::DocumentObjectGroupPython] H_element020  label="H_element : 0.025"  # scripted group (container) (typed FeaturePython)
  n = 0.02468
FEATURE [App::DocumentObjectGroupPython] C_element021  label="C_element : 0.502"  # scripted group (container) (typed FeaturePython)
  n = 0.501611
FEATURE [App::DocumentObjectGroupPython] O_element019  label="O_element : 0.005"  # scripted group (container) (typed FeaturePython)
  n = 0.004527
FEATURE [App::DocumentObjectGroupPython] F_element004  label="F_element : 0.465"  # scripted group (container) (typed FeaturePython)
  n = 0.465209
FEATURE [App::DocumentObjectGroupPython] Si_element001  label="Si_element : 0.004"  # scripted group (container) (typed FeaturePython)
  n = 0.003973
FEATURE [App::DocumentObjectGroupPython] G4_C_552  label="G4_C-552"  # scripted group (container) (typed FeaturePython)
  Dunit = g/cm3
  Dvalue = 1.76
  Group = -> [H_element020,C_element021,O_element019,F_element004,Si_element001]
  conduct = 2
  density = 1
  expand = 3
  formula = G4_C-552
  name = G4_C-552
  specific = 4
FEATURE [App::DocumentObjectGroupPython] Cd_element001  label="Cd_element : 1"  # scripted group (container) (typed FeaturePython)
  n = 1
  ref = Cd_element
FEATURE [App::DocumentObjectGroupPython] Te_element001  label="Te_element : 1"  # scripted group (container) (typed FeaturePython)
  n = 1
  ref = Te_element
FEATURE [App::DocumentObjectGroupPython] G4_CADMIUM_TELLURIDE  # scripted group (container) (typed FeaturePython)
  Dunit = g/cm3
  Dvalue = 6.2
  Group = -> [Cd_element001,Te_element001]
  conduct = 2
  density = 1
  expand = 3
  formula = G4_CADMIUM_TELLURIDE
  name = G4_CADMIUM_TELLURIDE
  specific = 4
FEATURE [App::DocumentObjectGroupPython] Cd_element002  label="Cd_element : 002"  # scripted group (container) (typed FeaturePython)
  n = 1
  ref = Cd_element
FEATURE [App::DocumentObjectGroupPython] W_element001  label="W_element : 1"  # scripted group (container) (typed FeaturePython)
  n = 1
  ref = W_element
FEATURE [App::DocumentObjectGroupPython] O_element020  label="O_element : 008"  # scripted group (container) (typed FeaturePython)
  n = 4
  ref = O_element
FEATURE [App::DocumentObjectGroupPython] G4_CADMIUM_TUNGSTATE  # scripted group (container) (typed FeaturePython)
  Dunit = g/cm3
  Dvalue = 7.9
  Group = -> [Cd_element002,W_element001,O_element020]
  conduct = 2
  density = 1
  expand = 3
  formula = G4_CADMIUM_TUNGSTATE
  name = G4_CADMIUM_TUNGSTATE
  specific = 4
FEATURE [App::DocumentObjectGroupPython] Ca_element005  label="Ca_element : 1"  # scripted group (container) (typed FeaturePython)
  n = 1
  ref = Ca_element
FEATURE [App::DocumentObjectGroupPython] C_element022  label="C_element : 009"  # scripted group (container) (typed FeaturePython)
  n = 1
  ref = C_element
FEATURE [App::DocumentObjectGroupPython] O_element021  label="O_element : 009"  # scripted group (container) (typed FeaturePython)
  n = 3
  ref = O_element
FEATURE [App::DocumentObjectGroupPython] G4_CALCIUM_CARBONATE  # scripted group (container) (typed FeaturePython)
  Dunit = g/cm3
  Dvalue = 2.8
  Group = -> [Ca_element005,C_element022,O_element021]
  conduct = 2
  density = 1
  expand = 3
  formula = G4_CALCIUM_CARBONATE
  name = G4_CALCIUM_CARBONATE
  specific = 4
FEATURE [App::DocumentObjectGroupPython] Ca_element006  label="Ca_element : 002"  # scripted group (container) (typed FeaturePython)
  n = 1
  ref = Ca_element
FEATURE [App::DocumentObjectGroupPython] F_element005  label="F_element : 003"  # scripted group (container) (typed FeaturePython)
  n = 2
  ref = F_element
FEATURE [App::DocumentObjectGroupPython] G4_CALCIUM_FLUORIDE  # scripted group (container) (typed FeaturePython)
  Dunit = g/cm3
  Dvalue = 3.18
  Group = -> [Ca_element006,F_element005]
  conduct = 2
  density = 1
  expand = 3
  formula = G4_CALCIUM_FLUORIDE
  name = G4_CALCIUM_FLUORIDE
  specific = 4
FEATURE [App::DocumentObjectGroupPython] Ca_element007  label="Ca_element : 003"  # scripted group (container) (typed FeaturePython)
  n = 1
  ref = Ca_element
FEATURE [App::DocumentObjectGroupPython] O_element022  label="O_element : 010"  # scripted group (container) (typed FeaturePython)
  n = 1
  ref = O_element
FEATURE [App::DocumentObjectGroupPython] G4_CALCIUM_OXIDE  # scripted group (container) (typed FeaturePython)
  Dunit = g/cm3
  Dvalue = 3.3
  Group = -> [Ca_element007,O_element022]
  conduct = 2
  density = 1
  expand = 3
  formula = G4_CALCIUM_OXIDE
  name = G4_CALCIUM_OXIDE
  specific = 4
FEATURE [App::DocumentObjectGroupPython] Ca_element008  label="Ca_element : 004"  # scripted group (container) (typed FeaturePython)
  n = 1
  ref = Ca_element
FEATURE [App::DocumentObjectGroupPython] S_element007  label="S_element : 002"  # scripted group (container) (typed FeaturePython)
  n = 1
  ref = S_element
FEATURE [App::DocumentObjectGroupPython] O_element023  label="O_element : 011"  # scripted group (container) (typed FeaturePython)
  n = 4
  ref = O_element
FEATURE [App::DocumentObjectGroupPython] G4_CALCIUM_SULFATE  # scripted group (container) (typed FeaturePython)
  Dunit = g/cm3
  Dvalue = 2.96
  Group = -> [Ca_element008,S_element007,O_element023]
  conduct = 2
  density = 1
  expand = 3
  formula = G4_CALCIUM_SULFATE
  name = G4_CALCIUM_SULFATE
  specific = 4
FEATURE [App::DocumentObjectGroupPython] Ca_element009  label="Ca_element : 005"  # scripted group (container) (typed FeaturePython)
  n = 1
  ref = Ca_element
FEATURE [App::DocumentObjectGroupPython] W_element002  label="W_element : 002"  # scripted group (container) (typed FeaturePython)
  n = 1
  ref = W_element
FEATURE [App::DocumentObjectGroupPython] O_element024  label="O_element : 012"  # scripted group (container) (typed FeaturePython)
  n = 4
  ref = O_element
FEATURE [App::DocumentObjectGroupPython] G4_CALCIUM_TUNGSTATE  # scripted group (container) (typed FeaturePython)
  Dunit = g/cm3
  Dvalue = 6.062
  Group = -> [Ca_element009,W_element002,O_element024]
  conduct = 2
  density = 1
  expand = 3
  formula = G4_CALCIUM_TUNGSTATE
  name = G4_CALCIUM_TUNGSTATE
  specific = 4
FEATURE [App::DocumentObjectGroupPython] C_element023  label="C_element : 010"  # scripted group (container) (typed FeaturePython)
  n = 1
  ref = C_element
FEATURE [App::DocumentObjectGroupPython] O_element025  label="O_element : 013"  # scripted group (container) (typed FeaturePython)
  n = 2
  ref = O_element
FEATURE [App::DocumentObjectGroupPython] G4_CARBON_DIOXIDE  # scripted group (container) (typed FeaturePython)
  Dunit = g/cm3
  Dvalue = 0.00184212
  Group = -> [C_element023,O_element025]
  conduct = 2
  density = 1
  expand = 3
  formula = G4_CARBON_DIOXIDE
  name = G4_CARBON_DIOXIDE
  specific = 4
FEATURE [App::DocumentObjectGroupPython] C_element024  label="C_element : 011"  # scripted group (container) (typed FeaturePython)
  n = 1
  ref = C_element
FEATURE [App::DocumentObjectGroupPython] Cl_element004  label="Cl_element : 4"  # scripted group (container) (typed FeaturePython)
  n = 4
  ref = Cl_element
FEATURE [App::DocumentObjectGroupPython] G4_CARBON_TETRACHLORIDE  # scripted group (container) (typed FeaturePython)
  Dunit = g/cm3
  Dvalue = 1.594
  Group = -> [C_element024,Cl_element004]
  conduct = 2
  density = 1
  expand = 3
  formula = G4_CARBON_TETRACHLORIDE
  name = G4_CARBON_TETRACHLORIDE
  specific = 4
FEATURE [App::DocumentObjectGroupPython] C_element025  label="C_element : 012"  # scripted group (container) (typed FeaturePython)
  n = 6
  ref = C_element
FEATURE [App::DocumentObjectGroupPython] H_element021  label="H_element : 012"  # scripted group (container) (typed FeaturePython)
  n = 10
  ref = H_element
FEATURE [App::DocumentObjectGroupPython] O_element026  label="O_element : 5"  # scripted group (container) (typed FeaturePython)
  n = 5
  ref = O_element
FEATURE [App::DocumentObjectGroupPython] G4_CELLULOSE_CELLOPHANE  # scripted group (container) (typed FeaturePython)
  Dunit = g/cm3
  Dvalue = 1.42
  Group = -> [C_element025,H_element021,O_element026]
  conduct = 2
  density = 1
  expand = 3
  formula = G4_CELLULOSE_CELLOPHANE
  name = G4_CELLULOSE_CELLOPHANE
  specific = 4
FEATURE [App::DocumentObjectGroupPython] H_element022  label="H_element : 0.067"  # scripted group (container) (typed FeaturePython)
  n = 0.067125
FEATURE [App::DocumentObjectGroupPython] C_element026  label="C_element : 0.545"  # scripted group (container) (typed FeaturePython)
  n = 0.545403
FEATURE [App::DocumentObjectGroupPython] O_element027  label="O_element : 0.387"  # scripted group (container) (typed FeaturePython)
  n = 0.387472
FEATURE [App::DocumentObjectGroupPython] G4_CELLULOSE_BUTYRATE  # scripted group (container) (typed FeaturePython)
  Dunit = g/cm3
  Dvalue = 1.2
  Group = -> [H_element022,C_element026,O_element027]
  conduct = 2
  density = 1
  expand = 3
  formula = G4_CELLULOSE_BUTYRATE
  name = G4_CELLULOSE_BUTYRATE
  specific = 4
FEATURE [App::DocumentObjectGroupPython] H_element023  label="H_element : 0.029"  # scripted group (container) (typed FeaturePython)
  n = 0.029216
FEATURE [App::DocumentObjectGroupPython] C_element027  label="C_element : 0.271"  # scripted group (container) (typed FeaturePython)
  n = 0.271296
FEATURE [App::DocumentObjectGroupPython] N_element013  label="N_element : 0.121"  # scripted group (container) (typed FeaturePython)
  n = 0.121276
FEATURE [App::DocumentObjectGroupPython] O_element028  label="O_element : 0.578"  # scripted group (container) (typed FeaturePython)
  n = 0.578212
FEATURE [App::DocumentObjectGroupPython] G4_CELLULOSE_NITRATE  # scripted group (container) (typed FeaturePython)
  Dunit = g/cm3
  Dvalue = 1.49
  Group = -> [H_element023,C_element027,N_element013,O_element028]
  conduct = 2
  density = 1
  expand = 3
  formula = G4_CELLULOSE_NITRATE
  name = G4_CELLULOSE_NITRATE
  specific = 4
FEATURE [App::DocumentObjectGroupPython] H_element024  label="H_element : 0.108"  # scripted group (container) (typed FeaturePython)
  n = 0.107596
FEATURE [App::DocumentObjectGroupPython] N_element014  label="N_element : 0.001"  # scripted group (container) (typed FeaturePython)
  n = 0.0008
FEATURE [App::DocumentObjectGroupPython] O_element029  label="O_element : 0.875"  # scripted group (container) (typed FeaturePython)
  n = 0.874976
FEATURE [App::DocumentObjectGroupPython] S_element008  label="S_element : 0.015"  # scripted group (container) (typed FeaturePython)
  n = 0.014627
FEATURE [App::DocumentObjectGroupPython] Ce_element001  label="Ce_element : 0.002"  # scripted group (container) (typed FeaturePython)
  n = 0.002001
FEATURE [App::DocumentObjectGroupPython] G4_CERIC_SULFATE  # scripted group (container) (typed FeaturePython)
  Dunit = g/cm3
  Dvalue = 1.03
  Group = -> [H_element024,N_element014,O_element029,S_element008,Ce_element001]
  conduct = 2
  density = 1
  expand = 3
  formula = G4_CERIC_SULFATE
  name = G4_CERIC_SULFATE
  specific = 4
FEATURE [App::DocumentObjectGroupPython] Cs_element001  label="Cs_element : 1"  # scripted group (container) (typed FeaturePython)
  n = 1
  ref = Cs_element
FEATURE [App::DocumentObjectGroupPython] F_element006  label="F_element : 1"  # scripted group (container) (typed FeaturePython)
  n = 1
  ref = F_element
FEATURE [App::DocumentObjectGroupPython] G4_CESIUM_FLUORIDE  # scripted group (container) (typed FeaturePython)
  Dunit = g/cm3
  Dvalue = 4.115
  Group = -> [Cs_element001,F_element006]
  conduct = 2
  density = 1
  expand = 3
  formula = G4_CESIUM_FLUORIDE
  name = G4_CESIUM_FLUORIDE
  specific = 4
FEATURE [App::DocumentObjectGroupPython] Cs_element002  label="Cs_element : 002"  # scripted group (container) (typed FeaturePython)
  n = 1
  ref = Cs_element
FEATURE [App::DocumentObjectGroupPython] I_element001  label="I_element : 1"  # scripted group (container) (typed FeaturePython)
  n = 1
  ref = I_element
FEATURE [App::DocumentObjectGroupPython] G4_CESIUM_IODIDE  # scripted group (container) (typed FeaturePython)
  Dunit = g/cm3
  Dvalue = 4.51
  Group = -> [Cs_element002,I_element001]
  conduct = 2
  density = 1
  expand = 3
  formula = G4_CESIUM_IODIDE
  name = G4_CESIUM_IODIDE
  specific = 4
FEATURE [App::DocumentObjectGroupPython] C_element028  label="C_element : 013"  # scripted group (container) (typed FeaturePython)
  n = 6
  ref = C_element
FEATURE [App::DocumentObjectGroupPython] H_element025  label="H_element : 013"  # scripted group (container) (typed FeaturePython)
  n = 5
  ref = H_element
FEATURE [App::DocumentObjectGroupPython] Cl_element005  label="Cl_element : 1"  # scripted group (container) (typed FeaturePython)
  n = 1
  ref = Cl_element
FEATURE [App::DocumentObjectGroupPython] G4_CHLOROBENZENE  # scripted group (container) (typed FeaturePython)
  Dunit = g/cm3
  Dvalue = 1.1058
  Group = -> [C_element028,H_element025,Cl_element005]
  conduct = 2
  density = 1
  expand = 3
  formula = G4_CHLOROBENZENE
  name = G4_CHLOROBENZENE
  specific = 4
FEATURE [App::DocumentObjectGroupPython] C_element029  label="C_element : 014"  # scripted group (container) (typed FeaturePython)
  n = 1
  ref = C_element
FEATURE [App::DocumentObjectGroupPython] H_element026  label="H_element : 1"  # scripted group (container) (typed FeaturePython)
  n = 1
  ref = H_element
FEATURE [App::DocumentObjectGroupPython] Cl_element006  label="Cl_element : 3"  # scripted group (container) (typed FeaturePython)
  n = 3
  ref = Cl_element
FEATURE [App::DocumentObjectGroupPython] G4_CHLOROFORM  # scripted group (container) (typed FeaturePython)
  Dunit = g/cm3
  Dvalue = 1.4832
  Group = -> [C_element029,H_element026,Cl_element006]
  conduct = 2
  density = 1
  expand = 3
  formula = G4_CHLOROFORM
  name = G4_CHLOROFORM
  specific = 4
FEATURE [App::DocumentObjectGroupPython] H_element027  label="H_element : 0.010"  # scripted group (container) (typed FeaturePython)
  n = 0.01
FEATURE [App::DocumentObjectGroupPython] C_element030  label="C_element : 0.001"  # scripted group (container) (typed FeaturePython)
  n = 0.001
FEATURE [App::DocumentObjectGroupPython] O_element030  label="O_element : 0.529"  # scripted group (container) (typed FeaturePython)
  n = 0.529107
FEATURE [App::DocumentObjectGroupPython] Na_element005  label="Na_element : 0.016"  # scripted group (container) (typed FeaturePython)
  n = 0.016
FEATURE [App::DocumentObjectGroupPython] Mg_element003  label="Mg_element : 0.004"  # scripted group (container) (typed FeaturePython)
  n = 0.002
FEATURE [App::DocumentObjectGroupPython] Al_element002  label="Al_element : 0.034"  # scripted group (container) (typed FeaturePython)
  n = 0.033872
FEATURE [App::DocumentObjectGroupPython] Si_element002  label="Si_element : 0.337"  # scripted group (container) (typed FeaturePython)
  n = 0.337021
FEATURE [App::DocumentObjectGroupPython] K_element003  label="K_element : 0.013"  # scripted group (container) (typed FeaturePython)
  n = 0.013
FEATURE [App::DocumentObjectGroupPython] Ca_element010  label="Ca_element : 0.044"  # scripted group (container) (typed FeaturePython)
  n = 0.044
FEATURE [App::DocumentObjectGroupPython] Fe_element002  label="Fe_element : 0.014"  # scripted group (container) (typed FeaturePython)
  n = 0.014
FEATURE [App::DocumentObjectGroupPython] G4_CONCRETE  # scripted group (container) (typed FeaturePython)
  Dunit = g/cm3
  Dvalue = 2.3
  Group = -> [H_element027,C_element030,O_element030,Na_element005,Mg_element003,Al_element002,Si_element002,K_element003,Ca_element010,Fe_element002]
  conduct = 2
  density = 1
  expand = 3
  formula = G4_CONCRETE
  name = G4_CONCRETE
  specific = 4
FEATURE [App::DocumentObjectGroupPython] C_element031  label="C_element : 015"  # scripted group (container) (typed FeaturePython)
  n = 6
  ref = C_element
FEATURE [App::DocumentObjectGroupPython] H_element028  label="H_element : 12"  # scripted group (container) (typed FeaturePython)
  n = 12
  ref = H_element
FEATURE [App::DocumentObjectGroupPython] G4_CYCLOHEXANE  # scripted group (container) (typed FeaturePython)
  Dunit = g/cm3
  Dvalue = 0.779
  Group = -> [C_element031,H_element028]
  conduct = 2
  density = 1
  expand = 3
  formula = G4_CYCLOHEXANE
  name = G4_CYCLOHEXANE
  specific = 4
FEATURE [App::DocumentObjectGroupPython] C_element032  label="C_element : 016"  # scripted group (container) (typed FeaturePython)
  n = 6
  ref = C_element
FEATURE [App::DocumentObjectGroupPython] H_element029  label="H_element : 4"  # scripted group (container) (typed FeaturePython)
  n = 4
  ref = H_element
FEATURE [App::DocumentObjectGroupPython] Cl_element007  label="Cl_element : 2"  # scripted group (container) (typed FeaturePython)
  n = 2
  ref = Cl_element
FEATURE [App::DocumentObjectGroupPython] G4_1_2_DICHLOROBENZENE  label="G4_1.2-DICHLOROBENZENE"  # scripted group (container) (typed FeaturePython)
  Dunit = g/cm3
  Dvalue = 1.3048
  Group = -> [C_element032,H_element029,Cl_element007]
  conduct = 2
  density = 1
  expand = 3
  formula = G4_1.2-DICHLOROBENZENE
  name = G4_1.2-DICHLOROBENZENE
  specific = 4
FEATURE [App::DocumentObjectGroupPython] C_element033  label="C_element : 017"  # scripted group (container) (typed FeaturePython)
  n = 4
  ref = C_element
FEATURE [App::DocumentObjectGroupPython] H_element030  label="H_element : 8"  # scripted group (container) (typed FeaturePython)
  n = 8
  ref = H_element
FEATURE [App::DocumentObjectGroupPython] O_element031  label="O_element : 014"  # scripted group (container) (typed FeaturePython)
  n = 1
  ref = O_element
FEATURE [App::DocumentObjectGroupPython] Cl_element008  label="Cl_element : 005"  # scripted group (container) (typed FeaturePython)
  n = 2
  ref = Cl_element
FEATURE [App::DocumentObjectGroupPython] G4_DICHLORODIETHYL_ETHER  # scripted group (container) (typed FeaturePython)
  Dunit = g/cm3
  Dvalue = 1.2199
  Group = -> [C_element033,H_element030,O_element031,Cl_element008]
  conduct = 2
  density = 1
  expand = 3
  formula = G4_DICHLORODIETHYL_ETHER
  name = G4_DICHLORODIETHYL_ETHER
  specific = 4
FEATURE [App::DocumentObjectGroupPython] C_element034  label="C_element : 018"  # scripted group (container) (typed FeaturePython)
  n = 2
  ref = C_element
FEATURE [App::DocumentObjectGroupPython] H_element031  label="H_element : 014"  # scripted group (container) (typed FeaturePython)
  n = 4
  ref = H_element
FEATURE [App::DocumentObjectGroupPython] Cl_element009  label="Cl_element : 006"  # scripted group (container) (typed FeaturePython)
  n = 2
  ref = Cl_element
FEATURE [App::DocumentObjectGroupPython] G4_1_2_DICHLOROETHANE  label="G4_1.2-DICHLOROETHANE"  # scripted group (container) (typed FeaturePython)
  Dunit = g/cm3
  Dvalue = 1.2351
  Group = -> [C_element034,H_element031,Cl_element009]
  conduct = 2
  density = 1
  expand = 3
  formula = G4_1.2-DICHLOROETHANE
  name = G4_1.2-DICHLOROETHANE
  specific = 4
FEATURE [App::DocumentObjectGroupPython] C_element035  label="C_element : 019"  # scripted group (container) (typed FeaturePython)
  n = 4
  ref = C_element
FEATURE [App::DocumentObjectGroupPython] H_element032  label="H_element : 015"  # scripted group (container) (typed FeaturePython)
  n = 10
  ref = H_element
FEATURE [App::DocumentObjectGroupPython] O_element032  label="O_element : 015"  # scripted group (container) (typed FeaturePython)
  n = 1
  ref = O_element
FEATURE [App::DocumentObjectGroupPython] G4_DIETHYL_ETHER  # scripted group (container) (typed FeaturePython)
  Dunit = g/cm3
  Dvalue = 0.71378
  Group = -> [C_element035,H_element032,O_element032]
  conduct = 2
  density = 1
  expand = 3
  formula = G4_DIETHYL_ETHER
  name = G4_DIETHYL_ETHER
  specific = 4
FEATURE [App::DocumentObjectGroupPython] C_element036  label="C_element : 020"  # scripted group (container) (typed FeaturePython)
  n = 3
  ref = C_element
FEATURE [App::DocumentObjectGroupPython] H_element033  label="H_element : 016"  # scripted group (container) (typed FeaturePython)
  n = 7
  ref = H_element
FEATURE [App::DocumentObjectGroupPython] N_element015  label="N_element : 008"  # scripted group (container) (typed FeaturePython)
  n = 1
  ref = N_element
FEATURE [App::DocumentObjectGroupPython] O_element033  label="O_element : 016"  # scripted group (container) (typed FeaturePython)
  n = 1
  ref = O_element
FEATURE [App::DocumentObjectGroupPython] G4_N_N_DIMETHYL_FORMAMIDE  label="G4_N.N-DIMETHYL_FORMAMIDE"  # scripted group (container) (typed FeaturePython)
  Dunit = g/cm3
  Dvalue = 0.9487
  Group = -> [C_element036,H_element033,N_element015,O_element033]
  conduct = 2
  density = 1
  expand = 3
  formula = G4_N.N-DIMETHYL_FORMAMIDE
  name = G4_N.N-DIMETHYL_FORMAMIDE
  specific = 4
FEATURE [App::DocumentObjectGroupPython] C_element037  label="C_element : 021"  # scripted group (container) (typed FeaturePython)
  n = 2
  ref = C_element
FEATURE [App::DocumentObjectGroupPython] H_element034  label="H_element : 017"  # scripted group (container) (typed FeaturePython)
  n = 6
  ref = H_element
FEATURE [App::DocumentObjectGroupPython] O_element034  label="O_element : 017"  # scripted group (container) (typed FeaturePython)
  n = 1
  ref = O_element
FEATURE [App::DocumentObjectGroupPython] S_element009  label="S_element : 003"  # scripted group (container) (typed FeaturePython)
  n = 1
  ref = S_element
FEATURE [App::DocumentObjectGroupPython] G4_DIMETHYL_SULFOXIDE  # scripted group (container) (typed FeaturePython)
  Dunit = g/cm3
  Dvalue = 1.1014
  Group = -> [C_element037,H_element034,O_element034,S_element009]
  conduct = 2
  density = 1
  expand = 3
  formula = G4_DIMETHYL_SULFOXIDE
  name = G4_DIMETHYL_SULFOXIDE
  specific = 4
FEATURE [App::DocumentObjectGroupPython] C_element038  label="C_element : 022"  # scripted group (container) (typed FeaturePython)
  n = 2
  ref = C_element
FEATURE [App::DocumentObjectGroupPython] H_element035  label="H_element : 018"  # scripted group (container) (typed FeaturePython)
  n = 6
  ref = H_element
FEATURE [App::DocumentObjectGroupPython] G4_ETHANE  # scripted group (container) (typed FeaturePython)
  Dunit = g/cm3
  Dvalue = 0.00125324
  Group = -> [C_element038,H_element035]
  conduct = 2
  density = 1
  expand = 3
  formula = G4_ETHANE
  name = G4_ETHANE
  specific = 4
FEATURE [App::DocumentObjectGroupPython] C_element039  label="C_element : 023"  # scripted group (container) (typed FeaturePython)
  n = 2
  ref = C_element
FEATURE [App::DocumentObjectGroupPython] H_element036  label="H_element : 019"  # scripted group (container) (typed FeaturePython)
  n = 6
  ref = H_element
FEATURE [App::DocumentObjectGroupPython] O_element035  label="O_element : 018"  # scripted group (container) (typed FeaturePython)
  n = 1
  ref = O_element
FEATURE [App::DocumentObjectGroupPython] G4_ETHYL_ALCOHOL  # scripted group (container) (typed FeaturePython)
  Dunit = g/cm3
  Dvalue = 0.7893
  Group = -> [C_element039,H_element036,O_element035]
  conduct = 2
  density = 1
  expand = 3
  formula = G4_ETHYL_ALCOHOL
  name = G4_ETHYL_ALCOHOL
  specific = 4
FEATURE [App::DocumentObjectGroupPython] H_element037  label="H_element : 0.090"  # scripted group (container) (typed FeaturePython)
  n = 0.090027
FEATURE [App::DocumentObjectGroupPython] C_element040  label="C_element : 0.585"  # scripted group (container) (typed FeaturePython)
  n = 0.585182
FEATURE [App::DocumentObjectGroupPython] O_element036  label="O_element : 0.325"  # scripted group (container) (typed FeaturePython)
  n = 0.324791
FEATURE [App::DocumentObjectGroupPython] G4_ETHYL_CELLULOSE  # scripted group (container) (typed FeaturePython)
  Dunit = g/cm3
  Dvalue = 1.13
  Group = -> [H_element037,C_element040,O_element036]
  conduct = 2
  density = 1
  expand = 3
  formula = G4_ETHYL_CELLULOSE
  name = G4_ETHYL_CELLULOSE
  specific = 4
FEATURE [App::DocumentObjectGroupPython] C_element041  label="C_element : 024"  # scripted group (container) (typed FeaturePython)
  n = 2
  ref = C_element
FEATURE [App::DocumentObjectGroupPython] H_element038  label="H_element : 020"  # scripted group (container) (typed FeaturePython)
  n = 4
  ref = H_element
FEATURE [App::DocumentObjectGroupPython] G4_ETHYLENE  # scripted group (container) (typed FeaturePython)
  Dunit = g/cm3
  Dvalue = 0.00117497
  Group = -> [C_element041,H_element038]
  conduct = 2
  density = 1
  expand = 3
  formula = G4_ETHYLENE
  name = G4_ETHYLENE
  specific = 4
FEATURE [App::DocumentObjectGroupPython] H_element039  label="H_element : 0.096"  # scripted group (container) (typed FeaturePython)
  n = 0.096
FEATURE [App::DocumentObjectGroupPython] C_element042  label="C_element : 0.195"  # scripted group (container) (typed FeaturePython)
  n = 0.195
FEATURE [App::DocumentObjectGroupPython] N_element016  label="N_element : 0.057"  # scripted group (container) (typed FeaturePython)
  n = 0.057
FEATURE [App::DocumentObjectGroupPython] O_element037  label="O_element : 0.646"  # scripted group (container) (typed FeaturePython)
  n = 0.646
FEATURE [App::DocumentObjectGroupPython] Na_element006  label="Na_element : 0.017"  # scripted group (container) (typed FeaturePython)
  n = 0.001
FEATURE [App::DocumentObjectGroupPython] P_element005  label="P_element : 0.104"  # scripted group (container) (typed FeaturePython)
  n = 0.001
FEATURE [App::DocumentObjectGroupPython] S_element010  label="S_element : 0.016"  # scripted group (container) (typed FeaturePython)
  n = 0.003
FEATURE [App::DocumentObjectGroupPython] Cl_element010  label="Cl_element : 0.005"  # scripted group (container) (typed FeaturePython)
  n = 0.001
FEATURE [App::DocumentObjectGroupPython] G4_EYE_LENS_ICRP  # scripted group (container) (typed FeaturePython)
  Dunit = g/cm3
  Dvalue = 1.07
  Group = -> [H_element039,C_element042,N_element016,O_element037,Na_element006,P_element005,S_element010,Cl_element010]
  conduct = 2
  density = 1
  expand = 3
  formula = G4_EYE_LENS_ICRP
  name = G4_EYE_LENS_ICRP
  specific = 4
FEATURE [App::DocumentObjectGroupPython] Fe_element003  label="Fe_element : 2"  # scripted group (container) (typed FeaturePython)
  n = 2
  ref = Fe_element
FEATURE [App::DocumentObjectGroupPython] O_element038  label="O_element : 019"  # scripted group (container) (typed FeaturePython)
  n = 3
  ref = O_element
FEATURE [App::DocumentObjectGroupPython] G4_FERRIC_OXIDE  # scripted group (container) (typed FeaturePython)
  Dunit = g/cm3
  Dvalue = 5.2
  Group = -> [Fe_element003,O_element038]
  conduct = 2
  density = 1
  expand = 3
  formula = G4_FERRIC_OXIDE
  name = G4_FERRIC_OXIDE
  specific = 4
FEATURE [App::DocumentObjectGroupPython] Fe_element004  label="Fe_element : 1"  # scripted group (container) (typed FeaturePython)
  n = 1
  ref = Fe_element
FEATURE [App::DocumentObjectGroupPython] B_element003  label="B_element : 1"  # scripted group (container) (typed FeaturePython)
  n = 1
  ref = B_element
FEATURE [App::DocumentObjectGroupPython] G4_FERROBORIDE  # scripted group (container) (typed FeaturePython)
  Dunit = g/cm3
  Dvalue = 7.15
  Group = -> [Fe_element004,B_element003]
  conduct = 2
  density = 1
  expand = 3
  formula = G4_FERROBORIDE
  name = G4_FERROBORIDE
  specific = 4
FEATURE [App::DocumentObjectGroupPython] Fe_element005  label="Fe_element : 003"  # scripted group (container) (typed FeaturePython)
  n = 1
  ref = Fe_element
FEATURE [App::DocumentObjectGroupPython] O_element039  label="O_element : 020"  # scripted group (container) (typed FeaturePython)
  n = 1
  ref = O_element
FEATURE [App::DocumentObjectGroupPython] G4_FERROUS_OXIDE  # scripted group (container) (typed FeaturePython)
  Dunit = g/cm3
  Dvalue = 5.7
  Group = -> [Fe_element005,O_element039]
  conduct = 2
  density = 1
  expand = 3
  formula = G4_FERROUS_OXIDE
  name = G4_FERROUS_OXIDE
  specific = 4
FEATURE [App::DocumentObjectGroupPython] H_element040  label="H_element : 0.115"  # scripted group (container) (typed FeaturePython)
  n = 0.108259
FEATURE [App::DocumentObjectGroupPython] N_element017  label="N_element : 0.000"  # scripted group (container) (typed FeaturePython)
  n = 2.7e-05
FEATURE [App::DocumentObjectGroupPython] O_element040  label="O_element : 0.879"  # scripted group (container) (typed FeaturePython)
  n = 0.878636
FEATURE [App::DocumentObjectGroupPython] Na_element007  label="Na_element : 0.000"  # scripted group (container) (typed FeaturePython)
  n = 2.2e-05
FEATURE [App::DocumentObjectGroupPython] S_element011  label="S_element : 0.013"  # scripted group (container) (typed FeaturePython)
  n = 0.012968
FEATURE [App::DocumentObjectGroupPython] Cl_element011  label="Cl_element : 0.000"  # scripted group (container) (typed FeaturePython)
  n = 3.4e-05
FEATURE [App::DocumentObjectGroupPython] Fe_element006  label="Fe_element : 0.000"  # scripted group (container) (typed FeaturePython)
  n = 5.4e-05
FEATURE [App::DocumentObjectGroupPython] G4_FERROUS_SULFATE  # scripted group (container) (typed FeaturePython)
  Dunit = g/cm3
  Dvalue = 1.024
  Group = -> [H_element040,N_element017,O_element040,Na_element007,S_element011,Cl_element011,Fe_element006]
  conduct = 2
  density = 1
  expand = 3
  formula = G4_FERROUS_SULFATE
  name = G4_FERROUS_SULFATE
  specific = 4
FEATURE [App::DocumentObjectGroupPython] C_element043  label="C_element : 0.099"  # scripted group (container) (typed FeaturePython)
  n = 0.099335
FEATURE [App::DocumentObjectGroupPython] F_element007  label="F_element : 0.314"  # scripted group (container) (typed FeaturePython)
  n = 0.314247
FEATURE [App::DocumentObjectGroupPython] Cl_element012  label="Cl_element : 0.586"  # scripted group (container) (typed FeaturePython)
  n = 0.586418
FEATURE [App::DocumentObjectGroupPython] G4_FREON_12  label="G4_FREON-12"  # scripted group (container) (typed FeaturePython)
  Dunit = g/cm3
  Dvalue = 1.12
  Group = -> [C_element043,F_element007,Cl_element012]
  conduct = 2
  density = 1
  expand = 3
  formula = G4_FREON-12
  name = G4_FREON-12
  specific = 4
FEATURE [App::DocumentObjectGroupPython] C_element044  label="C_element : 0.057"  # scripted group (container) (typed FeaturePython)
  n = 0.057245
FEATURE [App::DocumentObjectGroupPython] F_element008  label="F_element : 0.181"  # scripted group (container) (typed FeaturePython)
  n = 0.181096
FEATURE [App::DocumentObjectGroupPython] Br_element001  label="Br_element : 0.762"  # scripted group (container) (typed FeaturePython)
  n = 0.761659
FEATURE [App::DocumentObjectGroupPython] G4_FREON_12B2  label="G4_FREON-12B2"  # scripted group (container) (typed FeaturePython)
  Dunit = g/cm3
  Dvalue = 1.8
  Group = -> [C_element044,F_element008,Br_element001]
  conduct = 2
  density = 1
  expand = 3
  formula = G4_FREON-12B2
  name = G4_FREON-12B2
  specific = 4
FEATURE [App::DocumentObjectGroupPython] C_element045  label="C_element : 0.115"  # scripted group (container) (typed FeaturePython)
  n = 0.114983
FEATURE [App::DocumentObjectGroupPython] F_element009  label="F_element : 0.546"  # scripted group (container) (typed FeaturePython)
  n = 0.545621
FEATURE [App::DocumentObjectGroupPython] Cl_element013  label="Cl_element : 0.339"  # scripted group (container) (typed FeaturePython)
  n = 0.339396
FEATURE [App::DocumentObjectGroupPython] G4_FREON_13  label="G4_FREON-13"  # scripted group (container) (typed FeaturePython)
  Dunit = g/cm3
  Dvalue = 0.95
  Group = -> [C_element045,F_element009,Cl_element013]
  conduct = 2
  density = 1
  expand = 3
  formula = G4_FREON-13
  name = G4_FREON-13
  specific = 4
FEATURE [App::DocumentObjectGroupPython] C_element046  label="C_element : 025"  # scripted group (container) (typed FeaturePython)
  n = 1
  ref = C_element
FEATURE [App::DocumentObjectGroupPython] F_element010  label="F_element : 3"  # scripted group (container) (typed FeaturePython)
  n = 3
  ref = F_element
FEATURE [App::DocumentObjectGroupPython] Br_element002  label="Br_element : 1"  # scripted group (container) (typed FeaturePython)
  n = 1
  ref = Br_element
FEATURE [App::DocumentObjectGroupPython] G4_FREON_13B1  label="G4_FREON-13B1"  # scripted group (container) (typed FeaturePython)
  Dunit = g/cm3
  Dvalue = 1.5
  Group = -> [C_element046,F_element010,Br_element002]
  conduct = 2
  density = 1
  expand = 3
  formula = G4_FREON-13B1
  name = G4_FREON-13B1
  specific = 4
FEATURE [App::DocumentObjectGroupPython] C_element047  label="C_element : 0.061"  # scripted group (container) (typed FeaturePython)
  n = 0.061309
FEATURE [App::DocumentObjectGroupPython] F_element011  label="F_element : 0.291"  # scripted group (container) (typed FeaturePython)
  n = 0.290924
FEATURE [App::DocumentObjectGroupPython] I_element002  label="I_element : 0.648"  # scripted group (container) (typed FeaturePython)
  n = 0.647767
FEATURE [App::DocumentObjectGroupPython] G4_FREON_13I1  label="G4_FREON-13I1"  # scripted group (container) (typed FeaturePython)
  Dunit = g/cm3
  Dvalue = 1.8
  Group = -> [C_element047,F_element011,I_element002]
  conduct = 2
  density = 1
  expand = 3
  formula = G4_FREON-13I1
  name = G4_FREON-13I1
  specific = 4
FEATURE [App::DocumentObjectGroupPython] Gd_element001  label="Gd_element : 2"  # scripted group (container) (typed FeaturePython)
  n = 2
  ref = Gd_element
FEATURE [App::DocumentObjectGroupPython] O_element041  label="O_element : 021"  # scripted group (container) (typed FeaturePython)
  n = 2
  ref = O_element
FEATURE [App::DocumentObjectGroupPython] S_element012  label="S_element : 004"  # scripted group (container) (typed FeaturePython)
  n = 1
  ref = S_element
FEATURE [App::DocumentObjectGroupPython] G4_GADOLINIUM_OXYSULFIDE  # scripted group (container) (typed FeaturePython)
  Dunit = g/cm3
  Dvalue = 7.44
  Group = -> [Gd_element001,O_element041,S_element012]
  conduct = 2
  density = 1
  expand = 3
  formula = G4_GADOLINIUM_OXYSULFIDE
  name = G4_GADOLINIUM_OXYSULFIDE
  specific = 4
FEATURE [App::DocumentObjectGroupPython] Ga_element001  label="Ga_element : 1"  # scripted group (container) (typed FeaturePython)
  n = 1
  ref = Ga_element
FEATURE [App::DocumentObjectGroupPython] As_element001  label="As_element : 1"  # scripted group (container) (typed FeaturePython)
  n = 1
  ref = As_element
FEATURE [App::DocumentObjectGroupPython] G4_GALLIUM_ARSENIDE  # scripted group (container) (typed FeaturePython)
  Dunit = g/cm3
  Dvalue = 5.31
  Group = -> [Ga_element001,As_element001]
  conduct = 2
  density = 1
  expand = 3
  formula = G4_GALLIUM_ARSENIDE
  name = G4_GALLIUM_ARSENIDE
  specific = 4
FEATURE [App::DocumentObjectGroupPython] H_element041  label="H_element : 0.081"  # scripted group (container) (typed FeaturePython)
  n = 0.08118
FEATURE [App::DocumentObjectGroupPython] C_element048  label="C_element : 0.416"  # scripted group (container) (typed FeaturePython)
  n = 0.41606
FEATURE [App::DocumentObjectGroupPython] N_element018  label="N_element : 0.111"  # scripted group (container) (typed FeaturePython)
  n = 0.11124
FEATURE [App::DocumentObjectGroupPython] O_element042  label="O_element : 0.381"  # scripted group (container) (typed FeaturePython)
  n = 0.38064
FEATURE [App::DocumentObjectGroupPython] S_element013  label="S_element : 0.011"  # scripted group (container) (typed FeaturePython)
  n = 0.01088
FEATURE [App::DocumentObjectGroupPython] G4_GEL_PHOTO_EMULSION  # scripted group (container) (typed FeaturePython)
  Dunit = g/cm3
  Dvalue = 1.2914
  Group = -> [H_element041,C_element048,N_element018,O_element042,S_element013]
  conduct = 2
  density = 1
  expand = 3
  formula = G4_GEL_PHOTO_EMULSION
  name = G4_GEL_PHOTO_EMULSION
  specific = 4
FEATURE [App::DocumentObjectGroupPython] B_element004  label="B_element : 0.040"  # scripted group (container) (typed FeaturePython)
  n = 0.0400639
FEATURE [App::DocumentObjectGroupPython] O_element043  label="O_element : 0.540"  # scripted group (container) (typed FeaturePython)
  n = 0.539561
FEATURE [App::DocumentObjectGroupPython] Na_element008  label="Na_element : 0.028"  # scripted group (container) (typed FeaturePython)
  n = 0.0281909
FEATURE [App::DocumentObjectGroupPython] Al_element003  label="Al_element : 0.012"  # scripted group (container) (typed FeaturePython)
  n = 0.011644
FEATURE [App::DocumentObjectGroupPython] Si_element003  label="Si_element : 0.377"  # scripted group (container) (typed FeaturePython)
  n = 0.377219
FEATURE [App::DocumentObjectGroupPython] K_element004  label="K_element : 0.014"  # scripted group (container) (typed FeaturePython)
  n = 0.00332099
FEATURE [App::DocumentObjectGroupPython] G4_Pyrex_Glass  # scripted group (container) (typed FeaturePython)
  Dunit = g/cm3
  Dvalue = 2.23
  Group = -> [B_element004,O_element043,Na_element008,Al_element003,Si_element003,K_element004]
  conduct = 2
  density = 1
  expand = 3
  formula = G4_Pyrex_Glass
  name = G4_Pyrex_Glass
  specific = 4
FEATURE [App::DocumentObjectGroupPython] O_element044  label="O_element : 0.156"  # scripted group (container) (typed FeaturePython)
  n = 0.156453
FEATURE [App::DocumentObjectGroupPython] Si_element004  label="Si_element : 0.081"  # scripted group (container) (typed FeaturePython)
  n = 0.080866
FEATURE [App::DocumentObjectGroupPython] Ti_element001  label="Ti_element : 0.008"  # scripted group (container) (typed FeaturePython)
  n = 0.008092
FEATURE [App::DocumentObjectGroupPython] As_element002  label="As_element : 0.003"  # scripted group (container) (typed FeaturePython)
  n = 0.002651
FEATURE [App::DocumentObjectGroupPython] Pb_element001  label="Pb_element : 0.752"  # scripted group (container) (typed FeaturePython)
  n = 0.751938
FEATURE [App::DocumentObjectGroupPython] G4_GLASS_LEAD  # scripted group (container) (typed FeaturePython)
  Dunit = g/cm3
  Dvalue = 6.22
  Group = -> [O_element044,Si_element004,Ti_element001,As_element002,Pb_element001]
  conduct = 2
  density = 1
  expand = 3
  formula = G4_GLASS_LEAD
  name = G4_GLASS_LEAD
  specific = 4
FEATURE [App::DocumentObjectGroupPython] O_element045  label="O_element : 0.460"  # scripted group (container) (typed FeaturePython)
  n = 0.4598
FEATURE [App::DocumentObjectGroupPython] Na_element009  label="Na_element : 0.096"  # scripted group (container) (typed FeaturePython)
  n = 0.0964411
FEATURE [App::DocumentObjectGroupPython] Si_element005  label="Si_element : 0.378"  # scripted group (container) (typed FeaturePython)
  n = 0.336553
FEATURE [App::DocumentObjectGroupPython] Ca_element011  label="Ca_element : 0.107"  # scripted group (container) (typed FeaturePython)
  n = 0.107205
FEATURE [App::DocumentObjectGroupPython] G4_GLASS_PLATE  # scripted group (container) (typed FeaturePython)
  Dunit = g/cm3
  Dvalue = 2.4
  Group = -> [O_element045,Na_element009,Si_element005,Ca_element011]
  conduct = 2
  density = 1
  expand = 3
  formula = G4_GLASS_PLATE
  name = G4_GLASS_PLATE
  specific = 4
FEATURE [App::DocumentObjectGroupPython] C_element049  label="C_element : 026"  # scripted group (container) (typed FeaturePython)
  n = 5
  ref = C_element
FEATURE [App::DocumentObjectGroupPython] H_element042  label="H_element : 021"  # scripted group (container) (typed FeaturePython)
  n = 10
  ref = H_element
FEATURE [App::DocumentObjectGroupPython] N_element019  label="N_element : 2"  # scripted group (container) (typed FeaturePython)
  n = 2
  ref = N_element
FEATURE [App::DocumentObjectGroupPython] O_element046  label="O_element : 022"  # scripted group (container) (typed FeaturePython)
  n = 3
  ref = O_element
FEATURE [App::DocumentObjectGroupPython] G4_GLUTAMINE  # scripted group (container) (typed FeaturePython)
  Dunit = g/cm3
  Dvalue = 1.46
  Group = -> [C_element049,H_element042,N_element019,O_element046]
  conduct = 2
  density = 1
  expand = 3
  formula = G4_GLUTAMINE
  name = G4_GLUTAMINE
  specific = 4
FEATURE [App::DocumentObjectGroupPython] C_element050  label="C_element : 027"  # scripted group (container) (typed FeaturePython)
  n = 3
  ref = C_element
FEATURE [App::DocumentObjectGroupPython] H_element043  label="H_element : 022"  # scripted group (container) (typed FeaturePython)
  n = 8
  ref = H_element
FEATURE [App::DocumentObjectGroupPython] O_element047  label="O_element : 023"  # scripted group (container) (typed FeaturePython)
  n = 3
  ref = O_element
FEATURE [App::DocumentObjectGroupPython] G4_GLYCEROL  # scripted group (container) (typed FeaturePython)
  Dunit = g/cm3
  Dvalue = 1.2613
  Group = -> [C_element050,H_element043,O_element047]
  conduct = 2
  density = 1
  expand = 3
  formula = G4_GLYCEROL
  name = G4_GLYCEROL
  specific = 4
FEATURE [App::DocumentObjectGroupPython] C_element051  label="C_element : 028"  # scripted group (container) (typed FeaturePython)
  n = 5
  ref = C_element
FEATURE [App::DocumentObjectGroupPython] H_element044  label="H_element : 023"  # scripted group (container) (typed FeaturePython)
  n = 5
  ref = H_element
FEATURE [App::DocumentObjectGroupPython] N_element020  label="N_element : 009"  # scripted group (container) (typed FeaturePython)
  n = 5
  ref = N_element
FEATURE [App::DocumentObjectGroupPython] O_element048  label="O_element : 024"  # scripted group (container) (typed FeaturePython)
  n = 1
  ref = O_element
FEATURE [App::DocumentObjectGroupPython] G4_GUANINE  # scripted group (container) (typed FeaturePython)
  Dunit = g/cm3
  Dvalue = 2.2
  Group = -> [C_element051,H_element044,N_element020,O_element048]
  conduct = 2
  density = 1
  expand = 3
  formula = G4_GUANINE
  name = G4_GUANINE
  specific = 4
FEATURE [App::DocumentObjectGroupPython] Ca_element012  label="Ca_element : 006"  # scripted group (container) (typed FeaturePython)
  n = 1
  ref = Ca_element
FEATURE [App::DocumentObjectGroupPython] S_element014  label="S_element : 005"  # scripted group (container) (typed FeaturePython)
  n = 1
  ref = S_element
FEATURE [App::DocumentObjectGroupPython] O_element049  label="O_element : 6"  # scripted group (container) (typed FeaturePython)
  n = 6
  ref = O_element
FEATURE [App::DocumentObjectGroupPython] H_element045  label="H_element : 024"  # scripted group (container) (typed FeaturePython)
  n = 4
  ref = H_element
FEATURE [App::DocumentObjectGroupPython] G4_GYPSUM  # scripted group (container) (typed FeaturePython)
  Dunit = g/cm3
  Dvalue = 2.32
  Group = -> [Ca_element012,S_element014,O_element049,H_element045]
  conduct = 2
  density = 1
  expand = 3
  formula = G4_GYPSUM
  name = G4_GYPSUM
  specific = 4
FEATURE [App::DocumentObjectGroupPython] C_element052  label="C_element : 7"  # scripted group (container) (typed FeaturePython)
  n = 7
  ref = C_element
FEATURE [App::DocumentObjectGroupPython] H_element046  label="H_element : 16"  # scripted group (container) (typed FeaturePython)
  n = 16
  ref = H_element
FEATURE [App::DocumentObjectGroupPython] G4_N_HEPTANE  label="G4_N-HEPTANE"  # scripted group (container) (typed FeaturePython)
  Dunit = g/cm3
  Dvalue = 0.68376
  Group = -> [C_element052,H_element046]
  conduct = 2
  density = 1
  expand = 3
  formula = G4_N-HEPTANE
  name = G4_N-HEPTANE
  specific = 4
FEATURE [App::DocumentObjectGroupPython] C_element053  label="C_element : 029"  # scripted group (container) (typed FeaturePython)
  n = 6
  ref = C_element
FEATURE [App::DocumentObjectGroupPython] H_element047  label="H_element : 14"  # scripted group (container) (typed FeaturePython)
  n = 14
  ref = H_element
FEATURE [App::DocumentObjectGroupPython] G4_N_HEXANE  label="G4_N-HEXANE"  # scripted group (container) (typed FeaturePython)
  Dunit = g/cm3
  Dvalue = 0.6603
  Group = -> [C_element053,H_element047]
  conduct = 2
  density = 1
  expand = 3
  formula = G4_N-HEXANE
  name = G4_N-HEXANE
  specific = 4
FEATURE [App::DocumentObjectGroupPython] C_element054  label="C_element : 22"  # scripted group (container) (typed FeaturePython)
  n = 22
  ref = C_element
FEATURE [App::DocumentObjectGroupPython] H_element048  label="H_element : 025"  # scripted group (container) (typed FeaturePython)
  n = 10
  ref = H_element
FEATURE [App::DocumentObjectGroupPython] N_element021  label="N_element : 010"  # scripted group (container) (typed FeaturePython)
  n = 2
  ref = N_element
FEATURE [App::DocumentObjectGroupPython] O_element050  label="O_element : 025"  # scripted group (container) (typed FeaturePython)
  n = 5
  ref = O_element
FEATURE [App::DocumentObjectGroupPython] G4_KAPTON  # scripted group (container) (typed FeaturePython)
  Dunit = g/cm3
  Dvalue = 1.42
  Group = -> [C_element054,H_element048,N_element021,O_element050]
  conduct = 2
  density = 1
  expand = 3
  formula = G4_KAPTON
  name = G4_KAPTON
  specific = 4
FEATURE [App::DocumentObjectGroupPython] La_element001  label="La_element : 1"  # scripted group (container) (typed FeaturePython)
  n = 1
  ref = La_element
FEATURE [App::DocumentObjectGroupPython] Br_element003  label="Br_element : 002"  # scripted group (container) (typed FeaturePython)
  n = 1
  ref = Br_element
FEATURE [App::DocumentObjectGroupPython] O_element051  label="O_element : 026"  # scripted group (container) (typed FeaturePython)
  n = 1
  ref = O_element
FEATURE [App::DocumentObjectGroupPython] G4_LANTHANUM_OXYBROMIDE  # scripted group (container) (typed FeaturePython)
  Dunit = g/cm3
  Dvalue = 6.28
  Group = -> [La_element001,Br_element003,O_element051]
  conduct = 2
  density = 1
  expand = 3
  formula = G4_LANTHANUM_OXYBROMIDE
  name = G4_LANTHANUM_OXYBROMIDE
  specific = 4
FEATURE [App::DocumentObjectGroupPython] La_element002  label="La_element : 2"  # scripted group (container) (typed FeaturePython)
  n = 2
  ref = La_element
FEATURE [App::DocumentObjectGroupPython] O_element052  label="O_element : 027"  # scripted group (container) (typed FeaturePython)
  n = 2
  ref = O_element
FEATURE [App::DocumentObjectGroupPython] S_element015  label="S_element : 006"  # scripted group (container) (typed FeaturePython)
  n = 1
  ref = S_element
FEATURE [App::DocumentObjectGroupPython] G4_LANTHANUM_OXYSULFIDE  # scripted group (container) (typed FeaturePython)
  Dunit = g/cm3
  Dvalue = 5.86
  Group = -> [La_element002,O_element052,S_element015]
  conduct = 2
  density = 1
  expand = 3
  formula = G4_LANTHANUM_OXYSULFIDE
  name = G4_LANTHANUM_OXYSULFIDE
  specific = 4
FEATURE [App::DocumentObjectGroupPython] O_element053  label="O_element : 0.072"  # scripted group (container) (typed FeaturePython)
  n = 0.071682
FEATURE [App::DocumentObjectGroupPython] Pb_element002  label="Pb_element : 0.928"  # scripted group (container) (typed FeaturePython)
  n = 0.928318
FEATURE [App::DocumentObjectGroupPython] G4_LEAD_OXIDE  # scripted group (container) (typed FeaturePython)
  Dunit = g/cm3
  Dvalue = 9.53
  Group = -> [O_element053,Pb_element002]
  conduct = 2
  density = 1
  expand = 3
  formula = G4_LEAD_OXIDE
  name = G4_LEAD_OXIDE
  specific = 4
FEATURE [App::DocumentObjectGroupPython] Li_element001  label="Li_element : 1"  # scripted group (container) (typed FeaturePython)
  n = 1
  ref = Li_element
FEATURE [App::DocumentObjectGroupPython] N_element022  label="N_element : 011"  # scripted group (container) (typed FeaturePython)
  n = 1
  ref = N_element
FEATURE [App::DocumentObjectGroupPython] H_element049  label="H_element : 026"  # scripted group (container) (typed FeaturePython)
  n = 2
  ref = H_element
FEATURE [App::DocumentObjectGroupPython] G4_LITHIUM_AMIDE  # scripted group (container) (typed FeaturePython)
  Dunit = g/cm3
  Dvalue = 1.178
  Group = -> [Li_element001,N_element022,H_element049]
  conduct = 2
  density = 1
  expand = 3
  formula = G4_LITHIUM_AMIDE
  name = G4_LITHIUM_AMIDE
  specific = 4
FEATURE [App::DocumentObjectGroupPython] Li_element002  label="Li_element : 2"  # scripted group (container) (typed FeaturePython)
  n = 2
  ref = Li_element
FEATURE [App::DocumentObjectGroupPython] C_element055  label="C_element : 030"  # scripted group (container) (typed FeaturePython)
  n = 1
  ref = C_element
FEATURE [App::DocumentObjectGroupPython] O_element054  label="O_element : 028"  # scripted group (container) (typed FeaturePython)
  n = 3
  ref = O_element
FEATURE [App::DocumentObjectGroupPython] G4_LITHIUM_CARBONATE  # scripted group (container) (typed FeaturePython)
  Dunit = g/cm3
  Dvalue = 2.11
  Group = -> [Li_element002,C_element055,O_element054]
  conduct = 2
  density = 1
  expand = 3
  formula = G4_LITHIUM_CARBONATE
  name = G4_LITHIUM_CARBONATE
  specific = 4
FEATURE [App::DocumentObjectGroupPython] Li_element003  label="Li_element : 003"  # scripted group (container) (typed FeaturePython)
  n = 1
  ref = Li_element
FEATURE [App::DocumentObjectGroupPython] F_element012  label="F_element : 004"  # scripted group (container) (typed FeaturePython)
  n = 1
  ref = F_element
FEATURE [App::DocumentObjectGroupPython] G4_LITHIUM_FLUORIDE  # scripted group (container) (typed FeaturePython)
  Dunit = g/cm3
  Dvalue = 2.635
  Group = -> [Li_element003,F_element012]
  conduct = 2
  density = 1
  expand = 3
  formula = G4_LITHIUM_FLUORIDE
  name = G4_LITHIUM_FLUORIDE
  specific = 4
FEATURE [App::DocumentObjectGroupPython] Li_element004  label="Li_element : 004"  # scripted group (container) (typed FeaturePython)
  n = 1
  ref = Li_element
FEATURE [App::DocumentObjectGroupPython] H_element050  label="H_element : 027"  # scripted group (container) (typed FeaturePython)
  n = 1
  ref = H_element
FEATURE [App::DocumentObjectGroupPython] G4_LITHIUM_HYDRIDE  # scripted group (container) (typed FeaturePython)
  Dunit = g/cm3
  Dvalue = 0.82
  Group = -> [Li_element004,H_element050]
  conduct = 2
  density = 1
  expand = 3
  formula = G4_LITHIUM_HYDRIDE
  name = G4_LITHIUM_HYDRIDE
  specific = 4
FEATURE [App::DocumentObjectGroupPython] Li_element005  label="Li_element : 005"  # scripted group (container) (typed FeaturePython)
  n = 1
  ref = Li_element
FEATURE [App::DocumentObjectGroupPython] I_element003  label="I_element : 002"  # scripted group (container) (typed FeaturePython)
  n = 1
  ref = I_element
FEATURE [App::DocumentObjectGroupPython] G4_LITHIUM_IODIDE  # scripted group (container) (typed FeaturePython)
  Dunit = g/cm3
  Dvalue = 3.494
  Group = -> [Li_element005,I_element003]
  conduct = 2
  density = 1
  expand = 3
  formula = G4_LITHIUM_IODIDE
  name = G4_LITHIUM_IODIDE
  specific = 4
FEATURE [App::DocumentObjectGroupPython] Li_element006  label="Li_element : 006"  # scripted group (container) (typed FeaturePython)
  n = 2
  ref = Li_element
FEATURE [App::DocumentObjectGroupPython] O_element055  label="O_element : 029"  # scripted group (container) (typed FeaturePython)
  n = 1
  ref = O_element
FEATURE [App::DocumentObjectGroupPython] G4_LITHIUM_OXIDE  # scripted group (container) (typed FeaturePython)
  Dunit = g/cm3
  Dvalue = 2.013
  Group = -> [Li_element006,O_element055]
  conduct = 2
  density = 1
  expand = 3
  formula = G4_LITHIUM_OXIDE
  name = G4_LITHIUM_OXIDE
  specific = 4
FEATURE [App::DocumentObjectGroupPython] Li_element007  label="Li_element : 007"  # scripted group (container) (typed FeaturePython)
  n = 2
  ref = Li_element
FEATURE [App::DocumentObjectGroupPython] B_element005  label="B_element : 005"  # scripted group (container) (typed FeaturePython)
  n = 4
  ref = B_element
FEATURE [App::DocumentObjectGroupPython] O_element056  label="O_element : 7"  # scripted group (container) (typed FeaturePython)
  n = 7
  ref = O_element
FEATURE [App::DocumentObjectGroupPython] G4_LITHIUM_TETRABORATE  # scripted group (container) (typed FeaturePython)
  Dunit = g/cm3
  Dvalue = 2.44
  Group = -> [Li_element007,B_element005,O_element056]
  conduct = 2
  density = 1
  expand = 3
  formula = G4_LITHIUM_TETRABORATE
  name = G4_LITHIUM_TETRABORATE
  specific = 4
FEATURE [App::DocumentObjectGroupPython] H_element051  label="H_element : 0.105"  # scripted group (container) (typed FeaturePython)
  n = 0.105
FEATURE [App::DocumentObjectGroupPython] C_element056  label="C_element : 0.083"  # scripted group (container) (typed FeaturePython)
  n = 0.083
FEATURE [App::DocumentObjectGroupPython] N_element023  label="N_element : 0.023"  # scripted group (container) (typed FeaturePython)
  n = 0.023
FEATURE [App::DocumentObjectGroupPython] O_element057  label="O_element : 0.779"  # scripted group (container) (typed FeaturePython)
  n = 0.779
FEATURE [App::DocumentObjectGroupPython] Na_element010  label="Na_element : 0.097"  # scripted group (container) (typed FeaturePython)
  n = 0.002
FEATURE [App::DocumentObjectGroupPython] P_element006  label="P_element : 0.105"  # scripted group (container) (typed FeaturePython)
  n = 0.001
FEATURE [App::DocumentObjectGroupPython] S_element016  label="S_element : 0.017"  # scripted group (container) (typed FeaturePython)
  n = 0.002
FEATURE [App::DocumentObjectGroupPython] Cl_element014  label="Cl_element : 0.587"  # scripted group (container) (typed FeaturePython)
  n = 0.003
FEATURE [App::DocumentObjectGroupPython] K_element005  label="K_element : 0.015"  # scripted group (container) (typed FeaturePython)
  n = 0.002
FEATURE [App::DocumentObjectGroupPython] G4_LUNG_ICRP  # scripted group (container) (typed FeaturePython)
  Dunit = g/cm3
  Dvalue = 1.04
  Group = -> [H_element051,C_element056,N_element023,O_element057,Na_element010,P_element006,S_element016,Cl_element014,K_element005]
  conduct = 2
  density = 1
  expand = 3
  formula = G4_LUNG_ICRP
  name = G4_LUNG_ICRP
  specific = 4
FEATURE [App::DocumentObjectGroupPython] H_element052  label="H_element : 0.116"  # scripted group (container) (typed FeaturePython)
  n = 0.114318
FEATURE [App::DocumentObjectGroupPython] C_element057  label="C_element : 0.656"  # scripted group (container) (typed FeaturePython)
  n = 0.655824
FEATURE [App::DocumentObjectGroupPython] O_element058  label="O_element : 0.092"  # scripted group (container) (typed FeaturePython)
  n = 0.0921831
FEATURE [App::DocumentObjectGroupPython] Mg_element004  label="Mg_element : 0.135"  # scripted group (container) (typed FeaturePython)
  n = 0.134792
FEATURE [App::DocumentObjectGroupPython] Ca_element013  label="Ca_element : 0.003"  # scripted group (container) (typed FeaturePython)
  n = 0.002883
FEATURE [App::DocumentObjectGroupPython] G4_M3_WAX  # scripted group (container) (typed FeaturePython)
  Dunit = g/cm3
  Dvalue = 1.05
  Group = -> [H_element052,C_element057,O_element058,Mg_element004,Ca_element013]
  conduct = 2
  density = 1
  expand = 3
  formula = G4_M3_WAX
  name = G4_M3_WAX
  specific = 4
FEATURE [App::DocumentObjectGroupPython] Mg_element005  label="Mg_element : 1"  # scripted group (container) (typed FeaturePython)
  n = 1
  ref = Mg_element
FEATURE [App::DocumentObjectGroupPython] C_element058  label="C_element : 031"  # scripted group (container) (typed FeaturePython)
  n = 1
  ref = C_element
FEATURE [App::DocumentObjectGroupPython] O_element059  label="O_element : 030"  # scripted group (container) (typed FeaturePython)
  n = 3
  ref = O_element
FEATURE [App::DocumentObjectGroupPython] G4_MAGNESIUM_CARBONATE  # scripted group (container) (typed FeaturePython)
  Dunit = g/cm3
  Dvalue = 2.958
  Group = -> [Mg_element005,C_element058,O_element059]
  conduct = 2
  density = 1
  expand = 3
  formula = G4_MAGNESIUM_CARBONATE
  name = G4_MAGNESIUM_CARBONATE
  specific = 4
FEATURE [App::DocumentObjectGroupPython] Mg_element006  label="Mg_element : 002"  # scripted group (container) (typed FeaturePython)
  n = 1
  ref = Mg_element
FEATURE [App::DocumentObjectGroupPython] F_element013  label="F_element : 005"  # scripted group (container) (typed FeaturePython)
  n = 2
  ref = F_element
FEATURE [App::DocumentObjectGroupPython] G4_MAGNESIUM_FLUORIDE  # scripted group (container) (typed FeaturePython)
  Dunit = g/cm3
  Dvalue = 3
  Group = -> [Mg_element006,F_element013]
  conduct = 2
  density = 1
  expand = 3
  formula = G4_MAGNESIUM_FLUORIDE
  name = G4_MAGNESIUM_FLUORIDE
  specific = 4
FEATURE [App::DocumentObjectGroupPython] Mg_element007  label="Mg_element : 003"  # scripted group (container) (typed FeaturePython)
  n = 1
  ref = Mg_element
FEATURE [App::DocumentObjectGroupPython] O_element060  label="O_element : 031"  # scripted group (container) (typed FeaturePython)
  n = 1
  ref = O_element
FEATURE [App::DocumentObjectGroupPython] G4_MAGNESIUM_OXIDE  # scripted group (container) (typed FeaturePython)
  Dunit = g/cm3
  Dvalue = 3.58
  Group = -> [Mg_element007,O_element060]
  conduct = 2
  density = 1
  expand = 3
  formula = G4_MAGNESIUM_OXIDE
  name = G4_MAGNESIUM_OXIDE
  specific = 4
FEATURE [App::DocumentObjectGroupPython] Mg_element008  label="Mg_element : 004"  # scripted group (container) (typed FeaturePython)
  n = 1
  ref = Mg_element
FEATURE [App::DocumentObjectGroupPython] B_element006  label="B_element : 006"  # scripted group (container) (typed FeaturePython)
  n = 4
  ref = B_element
FEATURE [App::DocumentObjectGroupPython] O_element061  label="O_element : 032"  # scripted group (container) (typed FeaturePython)
  n = 7
  ref = O_element
FEATURE [App::DocumentObjectGroupPython] G4_MAGNESIUM_TETRABORATE  # scripted group (container) (typed FeaturePython)
  Dunit = g/cm3
  Dvalue = 2.53
  Group = -> [Mg_element008,B_element006,O_element061]
  conduct = 2
  density = 1
  expand = 3
  formula = G4_MAGNESIUM_TETRABORATE
  name = G4_MAGNESIUM_TETRABORATE
  specific = 4
FEATURE [App::DocumentObjectGroupPython] Hg_element001  label="Hg_element : 1"  # scripted group (container) (typed FeaturePython)
  n = 1
  ref = Hg_element
FEATURE [App::DocumentObjectGroupPython] I_element004  label="I_element : 2"  # scripted group (container) (typed FeaturePython)
  n = 2
  ref = I_element
FEATURE [App::DocumentObjectGroupPython] G4_MERCURIC_IODIDE  # scripted group (container) (typed FeaturePython)
  Dunit = g/cm3
  Dvalue = 6.36
  Group = -> [Hg_element001,I_element004]
  conduct = 2
  density = 1
  expand = 3
  formula = G4_MERCURIC_IODIDE
  name = G4_MERCURIC_IODIDE
  specific = 4
FEATURE [App::DocumentObjectGroupPython] C_element059  label="C_element : 032"  # scripted group (container) (typed FeaturePython)
  n = 1
  ref = C_element
FEATURE [App::DocumentObjectGroupPython] H_element053  label="H_element : 028"  # scripted group (container) (typed FeaturePython)
  n = 4
  ref = H_element
FEATURE [App::DocumentObjectGroupPython] G4_METHANE  # scripted group (container) (typed FeaturePython)
  Dunit = g/cm3
  Dvalue = 0.000667151
  Group = -> [C_element059,H_element053]
  conduct = 2
  density = 1
  expand = 3
  formula = G4_METHANE
  name = G4_METHANE
  specific = 4
FEATURE [App::DocumentObjectGroupPython] C_element060  label="C_element : 033"  # scripted group (container) (typed FeaturePython)
  n = 1
  ref = C_element
FEATURE [App::DocumentObjectGroupPython] H_element054  label="H_element : 029"  # scripted group (container) (typed FeaturePython)
  n = 4
  ref = H_element
FEATURE [App::DocumentObjectGroupPython] O_element062  label="O_element : 033"  # scripted group (container) (typed FeaturePython)
  n = 1
  ref = O_element
FEATURE [App::DocumentObjectGroupPython] G4_METHANOL  # scripted group (container) (typed FeaturePython)
  Dunit = g/cm3
  Dvalue = 0.7914
  Group = -> [C_element060,H_element054,O_element062]
  conduct = 2
  density = 1
  expand = 3
  formula = G4_METHANOL
  name = G4_METHANOL
  specific = 4
FEATURE [App::DocumentObjectGroupPython] H_element055  label="H_element : 0.134"  # scripted group (container) (typed FeaturePython)
  n = 0.13404
FEATURE [App::DocumentObjectGroupPython] C_element061  label="C_element : 0.778"  # scripted group (container) (typed FeaturePython)
  n = 0.77796
FEATURE [App::DocumentObjectGroupPython] O_element063  label="O_element : 0.035"  # scripted group (container) (typed FeaturePython)
  n = 0.03502
FEATURE [App::DocumentObjectGroupPython] Mg_element009  label="Mg_element : 0.039"  # scripted group (container) (typed FeaturePython)
  n = 0.038594
FEATURE [App::DocumentObjectGroupPython] Ti_element002  label="Ti_element : 0.014"  # scripted group (container) (typed FeaturePython)
  n = 0.014386
FEATURE [App::DocumentObjectGroupPython] G4_MIX_D_WAX  # scripted group (container) (typed FeaturePython)
  Dunit = g/cm3
  Dvalue = 0.99
  Group = -> [H_element055,C_element061,O_element063,Mg_element009,Ti_element002]
  conduct = 2
  density = 1
  expand = 3
  formula = G4_MIX_D_WAX
  name = G4_MIX_D_WAX
  specific = 4
FEATURE [App::DocumentObjectGroupPython] H_element056  label="H_element : 0.135"  # scripted group (container) (typed FeaturePython)
  n = 0.081192
FEATURE [App::DocumentObjectGroupPython] C_element062  label="C_element : 0.583"  # scripted group (container) (typed FeaturePython)
  n = 0.583442
FEATURE [App::DocumentObjectGroupPython] N_element024  label="N_element : 0.018"  # scripted group (container) (typed FeaturePython)
  n = 0.017798
FEATURE [App::DocumentObjectGroupPython] O_element064  label="O_element : 0.186"  # scripted group (container) (typed FeaturePython)
  n = 0.186381
FEATURE [App::DocumentObjectGroupPython] Mg_element010  label="Mg_element : 0.130"  # scripted group (container) (typed FeaturePython)
  n = 0.130287
FEATURE [App::DocumentObjectGroupPython] Cl_element015  label="Cl_element : 0.588"  # scripted group (container) (typed FeaturePython)
  n = 0.0009
FEATURE [App::DocumentObjectGroupPython] G4_MS20_TISSUE  # scripted group (container) (typed FeaturePython)
  Dunit = g/cm3
  Dvalue = 1
  Group = -> [H_element056,C_element062,N_element024,O_element064,Mg_element010,Cl_element015]
  conduct = 2
  density = 1
  expand = 3
  formula = G4_MS20_TISSUE
  name = G4_MS20_TISSUE
  specific = 4
FEATURE [App::DocumentObjectGroupPython] H_element057  label="H_element : 0.136"  # scripted group (container) (typed FeaturePython)
  n = 0.102
FEATURE [App::DocumentObjectGroupPython] C_element063  label="C_element : 0.143"  # scripted group (container) (typed FeaturePython)
  n = 0.143
FEATURE [App::DocumentObjectGroupPython] N_element025  label="N_element : 0.034"  # scripted group (container) (typed FeaturePython)
  n = 0.034
FEATURE [App::DocumentObjectGroupPython] O_element065  label="O_element : 0.710"  # scripted group (container) (typed FeaturePython)
  n = 0.71
FEATURE [App::DocumentObjectGroupPython] Na_element011  label="Na_element : 0.098"  # scripted group (container) (typed FeaturePython)
  n = 0.001
FEATURE [App::DocumentObjectGroupPython] P_element007  label="P_element : 0.002"  # scripted group (container) (typed FeaturePython)
  n = 0.002
FEATURE [App::DocumentObjectGroupPython] S_element017  label="S_element : 0.018"  # scripted group (container) (typed FeaturePython)
  n = 0.003
FEATURE [App::DocumentObjectGroupPython] Cl_element016  label="Cl_element : 0.589"  # scripted group (container) (typed FeaturePython)
  n = 0.001
FEATURE [App::DocumentObjectGroupPython] K_element006  label="K_element : 0.004"  # scripted group (container) (typed FeaturePython)
  n = 0.004
FEATURE [App::DocumentObjectGroupPython] G4_MUSCLE_SKELETAL_ICRP  # scripted group (container) (typed FeaturePython)
  Dunit = g/cm3
  Dvalue = 1.05
  Group = -> [H_element057,C_element063,N_element025,O_element065,Na_element011,P_element007,S_element017,Cl_element016,K_element006]
  conduct = 2
  density = 1
  expand = 3
  formula = G4_MUSCLE_SKELETAL_ICRP
  name = G4_MUSCLE_SKELETAL_ICRP
  specific = 4
FEATURE [App::DocumentObjectGroupPython] H_element058  label="H_element : 0.137"  # scripted group (container) (typed FeaturePython)
  n = 0.102102
FEATURE [App::DocumentObjectGroupPython] C_element064  label="C_element : 0.123"  # scripted group (container) (typed FeaturePython)
  n = 0.123123
FEATURE [App::DocumentObjectGroupPython] N_element026  label="N_element : 0.756"  # scripted group (container) (typed FeaturePython)
  n = 0.035035
FEATURE [App::DocumentObjectGroupPython] O_element066  label="O_element : 0.730"  # scripted group (container) (typed FeaturePython)
  n = 0.72973
FEATURE [App::DocumentObjectGroupPython] Na_element012  label="Na_element : 0.099"  # scripted group (container) (typed FeaturePython)
  n = 0.001001
FEATURE [App::DocumentObjectGroupPython] P_element008  label="P_element : 0.106"  # scripted group (container) (typed FeaturePython)
  n = 0.002002
FEATURE [App::DocumentObjectGroupPython] S_element018  label="S_element : 0.019"  # scripted group (container) (typed FeaturePython)
  n = 0.004004
FEATURE [App::DocumentObjectGroupPython] K_element007  label="K_element : 0.016"  # scripted group (container) (typed FeaturePython)
  n = 0.003003
FEATURE [App::DocumentObjectGroupPython] G4_MUSCLE_STRIATED_ICRU  # scripted group (container) (typed FeaturePython)
  Dunit = g/cm3
  Dvalue = 1.04
  Group = -> [H_element058,C_element064,N_element026,O_element066,Na_element012,P_element008,S_element018,K_element007]
  conduct = 2
  density = 1
  expand = 3
  formula = G4_MUSCLE_STRIATED_ICRU
  name = G4_MUSCLE_STRIATED_ICRU
  specific = 4
FEATURE [App::DocumentObjectGroupPython] H_element059  label="H_element : 0.098"  # scripted group (container) (typed FeaturePython)
  n = 0.0982341
FEATURE [App::DocumentObjectGroupPython] C_element065  label="C_element : 0.156"  # scripted group (container) (typed FeaturePython)
  n = 0.156214
FEATURE [App::DocumentObjectGroupPython] N_element027  label="N_element : 0.757"  # scripted group (container) (typed FeaturePython)
  n = 0.035451
FEATURE [App::DocumentObjectGroupPython] O_element067  label="O_element : 0.880"  # scripted group (container) (typed FeaturePython)
  n = 0.710101
FEATURE [App::DocumentObjectGroupPython] G4_MUSCLE_WITH_SUCROSE  # scripted group (container) (typed FeaturePython)
  Dunit = g/cm3
  Dvalue = 1.11
  Group = -> [H_element059,C_element065,N_element027,O_element067]
  conduct = 2
  density = 1
  expand = 3
  formula = G4_MUSCLE_WITH_SUCROSE
  name = G4_MUSCLE_WITH_SUCROSE
  specific = 4
FEATURE [App::DocumentObjectGroupPython] H_element060  label="H_element : 0.138"  # scripted group (container) (typed FeaturePython)
  n = 0.101969
FEATURE [App::DocumentObjectGroupPython] C_element066  label="C_element : 0.120"  # scripted group (container) (typed FeaturePython)
  n = 0.120058
FEATURE [App::DocumentObjectGroupPython] N_element028  label="N_element : 0.758"  # scripted group (container) (typed FeaturePython)
  n = 0.035451
FEATURE [App::DocumentObjectGroupPython] O_element068  label="O_element : 0.743"  # scripted group (container) (typed FeaturePython)
  n = 0.742522
FEATURE [App::DocumentObjectGroupPython] G4_MUSCLE_WITHOUT_SUCROSE  # scripted group (container) (typed FeaturePython)
  Dunit = g/cm3
  Dvalue = 1.07
  Group = -> [H_element060,C_element066,N_element028,O_element068]
  conduct = 2
  density = 1
  expand = 3
  formula = G4_MUSCLE_WITHOUT_SUCROSE
  name = G4_MUSCLE_WITHOUT_SUCROSE
  specific = 4
FEATURE [App::DocumentObjectGroupPython] C_element067  label="C_element : 10"  # scripted group (container) (typed FeaturePython)
  n = 10
  ref = C_element
FEATURE [App::DocumentObjectGroupPython] H_element061  label="H_element : 030"  # scripted group (container) (typed FeaturePython)
  n = 8
  ref = H_element
FEATURE [App::DocumentObjectGroupPython] G4_NAPHTHALENE  # scripted group (container) (typed FeaturePython)
  Dunit = g/cm3
  Dvalue = 1.145
  Group = -> [C_element067,H_element061]
  conduct = 2
  density = 1
  expand = 3
  formula = G4_NAPHTHALENE
  name = G4_NAPHTHALENE
  specific = 4
FEATURE [App::DocumentObjectGroupPython] C_element068  label="C_element : 034"  # scripted group (container) (typed FeaturePython)
  n = 6
  ref = C_element
FEATURE [App::DocumentObjectGroupPython] H_element062  label="H_element : 031"  # scripted group (container) (typed FeaturePython)
  n = 5
  ref = H_element
FEATURE [App::DocumentObjectGroupPython] N_element029  label="N_element : 012"  # scripted group (container) (typed FeaturePython)
  n = 1
  ref = N_element
FEATURE [App::DocumentObjectGroupPython] O_element069  label="O_element : 034"  # scripted group (container) (typed FeaturePython)
  n = 2
  ref = O_element
FEATURE [App::DocumentObjectGroupPython] G4_NITROBENZENE  # scripted group (container) (typed FeaturePython)
  Dunit = g/cm3
  Dvalue = 1.19867
  Group = -> [C_element068,H_element062,N_element029,O_element069]
  conduct = 2
  density = 1
  expand = 3
  formula = G4_NITROBENZENE
  name = G4_NITROBENZENE
  specific = 4
FEATURE [App::DocumentObjectGroupPython] N_element030  label="N_element : 013"  # scripted group (container) (typed FeaturePython)
  n = 2
  ref = N_element
FEATURE [App::DocumentObjectGroupPython] O_element070  label="O_element : 035"  # scripted group (container) (typed FeaturePython)
  n = 1
  ref = O_element
FEATURE [App::DocumentObjectGroupPython] G4_NITROUS_OXIDE  # scripted group (container) (typed FeaturePython)
  Dunit = g/cm3
  Dvalue = 0.00183094
  Group = -> [N_element030,O_element070]
  conduct = 2
  density = 1
  expand = 3
  formula = G4_NITROUS_OXIDE
  name = G4_NITROUS_OXIDE
  specific = 4
FEATURE [App::DocumentObjectGroupPython] H_element063  label="H_element : 0.104"  # scripted group (container) (typed FeaturePython)
  n = 0.103509
FEATURE [App::DocumentObjectGroupPython] C_element069  label="C_element : 0.648"  # scripted group (container) (typed FeaturePython)
  n = 0.648416
FEATURE [App::DocumentObjectGroupPython] N_element031  label="N_element : 0.100"  # scripted group (container) (typed FeaturePython)
  n = 0.0995361
FEATURE [App::DocumentObjectGroupPython] O_element071  label="O_element : 0.149"  # scripted group (container) (typed FeaturePython)
  n = 0.148539
FEATURE [App::DocumentObjectGroupPython] G4_NYLON_8062  label="G4_NYLON-8062"  # scripted group (container) (typed FeaturePython)
  Dunit = g/cm3
  Dvalue = 1.08
  Group = -> [H_element063,C_element069,N_element031,O_element071]
  conduct = 2
  density = 1
  expand = 3
  formula = G4_NYLON-8062
  name = G4_NYLON-8062
  specific = 4
FEATURE [App::DocumentObjectGroupPython] C_element070  label="C_element : 035"  # scripted group (container) (typed FeaturePython)
  n = 6
  ref = C_element
FEATURE [App::DocumentObjectGroupPython] H_element064  label="H_element : 11"  # scripted group (container) (typed FeaturePython)
  n = 11
  ref = H_element
FEATURE [App::DocumentObjectGroupPython] N_element032  label="N_element : 014"  # scripted group (container) (typed FeaturePython)
  n = 1
  ref = N_element
FEATURE [App::DocumentObjectGroupPython] O_element072  label="O_element : 036"  # scripted group (container) (typed FeaturePython)
  n = 1
  ref = O_element
FEATURE [App::DocumentObjectGroupPython] G4_NYLON_6_6  label="G4_NYLON-6-6"  # scripted group (container) (typed FeaturePython)
  Dunit = g/cm3
  Dvalue = 1.14
  Group = -> [C_element070,H_element064,N_element032,O_element072]
  conduct = 2
  density = 1
  expand = 3
  formula = G4_NYLON-6-6
  name = G4_NYLON-6-6
  specific = 4
FEATURE [App::DocumentObjectGroupPython] H_element065  label="H_element : 0.139"  # scripted group (container) (typed FeaturePython)
  n = 0.107062
FEATURE [App::DocumentObjectGroupPython] C_element071  label="C_element : 0.680"  # scripted group (container) (typed FeaturePython)
  n = 0.680449
FEATURE [App::DocumentObjectGroupPython] N_element033  label="N_element : 0.099"  # scripted group (container) (typed FeaturePython)
  n = 0.099189
FEATURE [App::DocumentObjectGroupPython] O_element073  label="O_element : 0.113"  # scripted group (container) (typed FeaturePython)
  n = 0.1133
FEATURE [App::DocumentObjectGroupPython] G4_NYLON_6_10  label="G4_NYLON-6-10"  # scripted group (container) (typed FeaturePython)
  Dunit = g/cm3
  Dvalue = 1.14
  Group = -> [H_element065,C_element071,N_element033,O_element073]
  conduct = 2
  density = 1
  expand = 3
  formula = G4_NYLON-6-10
  name = G4_NYLON-6-10
  specific = 4
FEATURE [App::DocumentObjectGroupPython] H_element066  label="H_element : 0.140"  # scripted group (container) (typed FeaturePython)
  n = 0.115476
FEATURE [App::DocumentObjectGroupPython] C_element072  label="C_element : 0.721"  # scripted group (container) (typed FeaturePython)
  n = 0.720818
FEATURE [App::DocumentObjectGroupPython] N_element034  label="N_element : 0.076"  # scripted group (container) (typed FeaturePython)
  n = 0.0764169
FEATURE [App::DocumentObjectGroupPython] O_element074  label="O_element : 0.087"  # scripted group (container) (typed FeaturePython)
  n = 0.0872889
FEATURE [App::DocumentObjectGroupPython] G4_NYLON_11_RILSAN  label="G4_NYLON-11_RILSAN"  # scripted group (container) (typed FeaturePython)
  Dunit = g/cm3
  Dvalue = 1.425
  Group = -> [H_element066,C_element072,N_element034,O_element074]
  conduct = 2
  density = 1
  expand = 3
  formula = G4_NYLON-11_RILSAN
  name = G4_NYLON-11_RILSAN
  specific = 4
FEATURE [App::DocumentObjectGroupPython] C_element073  label="C_element : 8"  # scripted group (container) (typed FeaturePython)
  n = 8
  ref = C_element
FEATURE [App::DocumentObjectGroupPython] H_element067  label="H_element : 18"  # scripted group (container) (typed FeaturePython)
  n = 18
  ref = H_element
FEATURE [App::DocumentObjectGroupPython] G4_OCTANE  # scripted group (container) (typed FeaturePython)
  Dunit = g/cm3
  Dvalue = 0.7026
  Group = -> [C_element073,H_element067]
  conduct = 2
  density = 1
  expand = 3
  formula = G4_OCTANE
  name = G4_OCTANE
  specific = 4
FEATURE [App::DocumentObjectGroupPython] C_element074  label="C_element : 25"  # scripted group (container) (typed FeaturePython)
  n = 25
  ref = C_element
FEATURE [App::DocumentObjectGroupPython] H_element068  label="H_element : 52"  # scripted group (container) (typed FeaturePython)
  n = 52
  ref = H_element
FEATURE [App::DocumentObjectGroupPython] G4_PARAFFIN  # scripted group (container) (typed FeaturePython)
  Dunit = g/cm3
  Dvalue = 0.93
  Group = -> [C_element074,H_element068]
  conduct = 2
  density = 1
  expand = 3
  formula = G4_PARAFFIN
  name = G4_PARAFFIN
  specific = 4
FEATURE [App::DocumentObjectGroupPython] C_element075  label="C_element : 036"  # scripted group (container) (typed FeaturePython)
  n = 5
  ref = C_element
FEATURE [App::DocumentObjectGroupPython] H_element069  label="H_element : 032"  # scripted group (container) (typed FeaturePython)
  n = 12
  ref = H_element
FEATURE [App::DocumentObjectGroupPython] G4_N_PENTANE  label="G4_N-PENTANE"  # scripted group (container) (typed FeaturePython)
  Dunit = g/cm3
  Dvalue = 0.6262
  Group = -> [C_element075,H_element069]
  conduct = 2
  density = 1
  expand = 3
  formula = G4_N-PENTANE
  name = G4_N-PENTANE
  specific = 4
FEATURE [App::DocumentObjectGroupPython] H_element070  label="H_element : 0.014"  # scripted group (container) (typed FeaturePython)
  n = 0.0141
FEATURE [App::DocumentObjectGroupPython] C_element076  label="C_element : 0.072"  # scripted group (container) (typed FeaturePython)
  n = 0.072261
FEATURE [App::DocumentObjectGroupPython] N_element035  label="N_element : 0.019"  # scripted group (container) (typed FeaturePython)
  n = 0.01932
FEATURE [App::DocumentObjectGroupPython] O_element075  label="O_element : 0.066"  # scripted group (container) (typed FeaturePython)
  n = 0.066101
FEATURE [App::DocumentObjectGroupPython] S_element019  label="S_element : 0.020"  # scripted group (container) (typed FeaturePython)
  n = 0.00189
FEATURE [App::DocumentObjectGroupPython] Br_element004  label="Br_element : 0.349"  # scripted group (container) (typed FeaturePython)
  n = 0.349103
FEATURE [App::DocumentObjectGroupPython] Ag_element001  label="Ag_element : 0.474"  # scripted group (container) (typed FeaturePython)
  n = 0.474105
FEATURE [App::DocumentObjectGroupPython] I_element005  label="I_element : 0.003"  # scripted group (container) (typed FeaturePython)
  n = 0.00312
FEATURE [App::DocumentObjectGroupPython] G4_PHOTO_EMULSION  # scripted group (container) (typed FeaturePython)
  Dunit = g/cm3
  Dvalue = 3.815
  Group = -> [H_element070,C_element076,N_element035,O_element075,S_element019,Br_element004,Ag_element001,I_element005]
  conduct = 2
  density = 1
  expand = 3
  formula = G4_PHOTO_EMULSION
  name = G4_PHOTO_EMULSION
  specific = 4
FEATURE [App::DocumentObjectGroupPython] C_element077  label="C_element : 9"  # scripted group (container) (typed FeaturePython)
  n = 9
  ref = C_element
FEATURE [App::DocumentObjectGroupPython] H_element071  label="H_element : 033"  # scripted group (container) (typed FeaturePython)
  n = 10
  ref = H_element
FEATURE [App::DocumentObjectGroupPython] G4_PLASTIC_SC_VINYLTOLUENE  # scripted group (container) (typed FeaturePython)
  Dunit = g/cm3
  Dvalue = 1.032
  Group = -> [C_element077,H_element071]
  conduct = 2
  density = 1
  expand = 3
  formula = G4_PLASTIC_SC_VINYLTOLUENE
  name = G4_PLASTIC_SC_VINYLTOLUENE
  specific = 4
FEATURE [App::DocumentObjectGroupPython] Pu_element001  label="Pu_element : 1"  # scripted group (container) (typed FeaturePython)
  n = 1
  ref = Pu_element
FEATURE [App::DocumentObjectGroupPython] O_element076  label="O_element : 037"  # scripted group (container) (typed FeaturePython)
  n = 2
  ref = O_element
FEATURE [App::DocumentObjectGroupPython] G4_PLUTONIUM_DIOXIDE  # scripted group (container) (typed FeaturePython)
  Dunit = g/cm3
  Dvalue = 11.46
  Group = -> [Pu_element001,O_element076]
  conduct = 2
  density = 1
  expand = 3
  formula = G4_PLUTONIUM_DIOXIDE
  name = G4_PLUTONIUM_DIOXIDE
  specific = 4
FEATURE [App::DocumentObjectGroupPython] C_element078  label="C_element : 037"  # scripted group (container) (typed FeaturePython)
  n = 3
  ref = C_element
FEATURE [App::DocumentObjectGroupPython] H_element072  label="H_element : 034"  # scripted group (container) (typed FeaturePython)
  n = 3
  ref = H_element
FEATURE [App::DocumentObjectGroupPython] N_element036  label="N_element : 015"  # scripted group (container) (typed FeaturePython)
  n = 1
  ref = N_element
FEATURE [App::DocumentObjectGroupPython] G4_POLYACRYLONITRILE  # scripted group (container) (typed FeaturePython)
  Dunit = g/cm3
  Dvalue = 1.17
  Group = -> [C_element078,H_element072,N_element036]
  conduct = 2
  density = 1
  expand = 3
  formula = G4_POLYACRYLONITRILE
  name = G4_POLYACRYLONITRILE
  specific = 4
FEATURE [App::DocumentObjectGroupPython] C_element079  label="C_element : 16"  # scripted group (container) (typed FeaturePython)
  n = 16
  ref = C_element
FEATURE [App::DocumentObjectGroupPython] H_element073  label="H_element : 035"  # scripted group (container) (typed FeaturePython)
  n = 14
  ref = H_element
FEATURE [App::DocumentObjectGroupPython] O_element077  label="O_element : 038"  # scripted group (container) (typed FeaturePython)
  n = 3
  ref = O_element
FEATURE [App::DocumentObjectGroupPython] G4_POLYCARBONATE  # scripted group (container) (typed FeaturePython)
  Dunit = g/cm3
  Dvalue = 1.2
  Group = -> [C_element079,H_element073,O_element077]
  conduct = 2
  density = 1
  expand = 3
  formula = G4_POLYCARBONATE
  name = G4_POLYCARBONATE
  specific = 4
FEATURE [App::DocumentObjectGroupPython] C_element080  label="C_element : 038"  # scripted group (container) (typed FeaturePython)
  n = 8
  ref = C_element
FEATURE [App::DocumentObjectGroupPython] H_element074  label="H_element : 036"  # scripted group (container) (typed FeaturePython)
  n = 7
  ref = H_element
FEATURE [App::DocumentObjectGroupPython] Cl_element017  label="Cl_element : 007"  # scripted group (container) (typed FeaturePython)
  n = 1
  ref = Cl_element
FEATURE [App::DocumentObjectGroupPython] G4_POLYCHLOROSTYRENE  # scripted group (container) (typed FeaturePython)
  Dunit = g/cm3
  Dvalue = 1.3
  Group = -> [C_element080,H_element074,Cl_element017]
  conduct = 2
  density = 1
  expand = 3
  formula = G4_POLYCHLOROSTYRENE
  name = G4_POLYCHLOROSTYRENE
  specific = 4
FEATURE [App::DocumentObjectGroupPython] C_element081  label="C_element : 039"  # scripted group (container) (typed FeaturePython)
  n = 1
  ref = C_element
FEATURE [App::DocumentObjectGroupPython] H_element075  label="H_element : 037"  # scripted group (container) (typed FeaturePython)
  n = 2
  ref = H_element
FEATURE [App::DocumentObjectGroupPython] G4_POLYETHYLENE  # scripted group (container) (typed FeaturePython)
  Dunit = g/cm3
  Dvalue = 0.94
  Group = -> [C_element081,H_element075]
  conduct = 2
  density = 1
  expand = 3
  formula = G4_POLYETHYLENE
  name = G4_POLYETHYLENE
  specific = 4
FEATURE [App::DocumentObjectGroupPython] C_element082  label="C_element : 040"  # scripted group (container) (typed FeaturePython)
  n = 10
  ref = C_element
FEATURE [App::DocumentObjectGroupPython] H_element076  label="H_element : 038"  # scripted group (container) (typed FeaturePython)
  n = 8
  ref = H_element
FEATURE [App::DocumentObjectGroupPython] O_element078  label="O_element : 039"  # scripted group (container) (typed FeaturePython)
  n = 4
  ref = O_element
FEATURE [App::DocumentObjectGroupPython] G4_MYLAR  # scripted group (container) (typed FeaturePython)
  Dunit = g/cm3
  Dvalue = 1.4
  Group = -> [C_element082,H_element076,O_element078]
  conduct = 2
  density = 1
  expand = 3
  formula = G4_MYLAR
  name = G4_MYLAR
  specific = 4
FEATURE [App::DocumentObjectGroupPython] C_element083  label="C_element : 041"  # scripted group (container) (typed FeaturePython)
  n = 5
  ref = C_element
FEATURE [App::DocumentObjectGroupPython] H_element077  label="H_element : 039"  # scripted group (container) (typed FeaturePython)
  n = 8
  ref = H_element
FEATURE [App::DocumentObjectGroupPython] O_element079  label="O_element : 040"  # scripted group (container) (typed FeaturePython)
  n = 2
  ref = O_element
FEATURE [App::DocumentObjectGroupPython] G4_PLEXIGLASS  # scripted group (container) (typed FeaturePython)
  Dunit = g/cm3
  Dvalue = 1.19
  Group = -> [C_element083,H_element077,O_element079]
  conduct = 2
  density = 1
  expand = 3
  formula = G4_PLEXIGLASS
  name = G4_PLEXIGLASS
  specific = 4
FEATURE [App::DocumentObjectGroupPython] C_element084  label="C_element : 042"  # scripted group (container) (typed FeaturePython)
  n = 1
  ref = C_element
FEATURE [App::DocumentObjectGroupPython] H_element078  label="H_element : 040"  # scripted group (container) (typed FeaturePython)
  n = 2
  ref = H_element
FEATURE [App::DocumentObjectGroupPython] O_element080  label="O_element : 041"  # scripted group (container) (typed FeaturePython)
  n = 1
  ref = O_element
FEATURE [App::DocumentObjectGroupPython] G4_POLYOXYMETHYLENE  # scripted group (container) (typed FeaturePython)
  Dunit = g/cm3
  Dvalue = 1.425
  Group = -> [C_element084,H_element078,O_element080]
  conduct = 2
  density = 1
  expand = 3
  formula = G4_POLYOXYMETHYLENE
  name = G4_POLYOXYMETHYLENE
  specific = 4
FEATURE [App::DocumentObjectGroupPython] C_element085  label="C_element : 043"  # scripted group (container) (typed FeaturePython)
  n = 2
  ref = C_element
FEATURE [App::DocumentObjectGroupPython] H_element079  label="H_element : 041"  # scripted group (container) (typed FeaturePython)
  n = 4
  ref = H_element
FEATURE [App::DocumentObjectGroupPython] G4_POLYPROPYLENE  # scripted group (container) (typed FeaturePython)
  Dunit = g/cm3
  Dvalue = 0.9
  Group = -> [C_element085,H_element079]
  conduct = 2
  density = 1
  expand = 3
  formula = G4_POLYPROPYLENE
  name = G4_POLYPROPYLENE
  specific = 4
FEATURE [App::DocumentObjectGroupPython] C_element086  label="C_element : 044"  # scripted group (container) (typed FeaturePython)
  n = 8
  ref = C_element
FEATURE [App::DocumentObjectGroupPython] H_element080  label="H_element : 042"  # scripted group (container) (typed FeaturePython)
  n = 8
  ref = H_element
FEATURE [App::DocumentObjectGroupPython] G4_POLYSTYRENE  # scripted group (container) (typed FeaturePython)
  Dunit = g/cm3
  Dvalue = 1.06
  Group = -> [C_element086,H_element080]
  conduct = 2
  density = 1
  expand = 3
  formula = G4_POLYSTYRENE
  name = G4_POLYSTYRENE
  specific = 4
FEATURE [App::DocumentObjectGroupPython] C_element087  label="C_element : 045"  # scripted group (container) (typed FeaturePython)
  n = 2
  ref = C_element
FEATURE [App::DocumentObjectGroupPython] F_element014  label="F_element : 4"  # scripted group (container) (typed FeaturePython)
  n = 4
  ref = F_element
FEATURE [App::DocumentObjectGroupPython] G4_TEFLON  # scripted group (container) (typed FeaturePython)
  Dunit = g/cm3
  Dvalue = 2.2
  Group = -> [C_element087,F_element014]
  conduct = 2
  density = 1
  expand = 3
  formula = G4_TEFLON
  name = G4_TEFLON
  specific = 4
FEATURE [App::DocumentObjectGroupPython] C_element088  label="C_element : 046"  # scripted group (container) (typed FeaturePython)
  n = 2
  ref = C_element
FEATURE [App::DocumentObjectGroupPython] F_element015  label="F_element : 006"  # scripted group (container) (typed FeaturePython)
  n = 3
  ref = F_element
FEATURE [App::DocumentObjectGroupPython] Cl_element018  label="Cl_element : 008"  # scripted group (container) (typed FeaturePython)
  n = 1
  ref = Cl_element
FEATURE [App::DocumentObjectGroupPython] G4_POLYTRIFLUOROCHLOROETHYLENE  # scripted group (container) (typed FeaturePython)
  Dunit = g/cm3
  Dvalue = 2.1
  Group = -> [C_element088,F_element015,Cl_element018]
  conduct = 2
  density = 1
  expand = 3
  formula = G4_POLYTRIFLUOROCHLOROETHYLENE
  name = G4_POLYTRIFLUOROCHLOROETHYLENE
  specific = 4
FEATURE [App::DocumentObjectGroupPython] C_element089  label="C_element : 047"  # scripted group (container) (typed FeaturePython)
  n = 4
  ref = C_element
FEATURE [App::DocumentObjectGroupPython] H_element081  label="H_element : 043"  # scripted group (container) (typed FeaturePython)
  n = 6
  ref = H_element
FEATURE [App::DocumentObjectGroupPython] O_element081  label="O_element : 042"  # scripted group (container) (typed FeaturePython)
  n = 2
  ref = O_element
FEATURE [App::DocumentObjectGroupPython] G4_POLYVINYL_ACETATE  # scripted group (container) (typed FeaturePython)
  Dunit = g/cm3
  Dvalue = 1.19
  Group = -> [C_element089,H_element081,O_element081]
  conduct = 2
  density = 1
  expand = 3
  formula = G4_POLYVINYL_ACETATE
  name = G4_POLYVINYL_ACETATE
  specific = 4
FEATURE [App::DocumentObjectGroupPython] C_element090  label="C_element : 048"  # scripted group (container) (typed FeaturePython)
  n = 2
  ref = C_element
FEATURE [App::DocumentObjectGroupPython] H_element082  label="H_element : 044"  # scripted group (container) (typed FeaturePython)
  n = 4
  ref = H_element
FEATURE [App::DocumentObjectGroupPython] O_element082  label="O_element : 043"  # scripted group (container) (typed FeaturePython)
  n = 1
  ref = O_element
FEATURE [App::DocumentObjectGroupPython] G4_POLYVINYL_ALCOHOL  # scripted group (container) (typed FeaturePython)
  Dunit = g/cm3
  Dvalue = 1.3
  Group = -> [C_element090,H_element082,O_element082]
  conduct = 2
  density = 1
  expand = 3
  formula = G4_POLYVINYL_ALCOHOL
  name = G4_POLYVINYL_ALCOHOL
  specific = 4
FEATURE [App::DocumentObjectGroupPython] C_element091  label="C_element : 049"  # scripted group (container) (typed FeaturePython)
  n = 8
  ref = C_element
FEATURE [App::DocumentObjectGroupPython] H_element083  label="H_element : 045"  # scripted group (container) (typed FeaturePython)
  n = 14
  ref = H_element
FEATURE [App::DocumentObjectGroupPython] O_element083  label="O_element : 044"  # scripted group (container) (typed FeaturePython)
  n = 2
  ref = O_element
FEATURE [App::DocumentObjectGroupPython] G4_POLYVINYL_BUTYRAL  # scripted group (container) (typed FeaturePython)
  Dunit = g/cm3
  Dvalue = 1.12
  Group = -> [C_element091,H_element083,O_element083]
  conduct = 2
  density = 1
  expand = 3
  formula = G4_POLYVINYL_BUTYRAL
  name = G4_POLYVINYL_BUTYRAL
  specific = 4
FEATURE [App::DocumentObjectGroupPython] C_element092  label="C_element : 050"  # scripted group (container) (typed FeaturePython)
  n = 2
  ref = C_element
FEATURE [App::DocumentObjectGroupPython] H_element084  label="H_element : 046"  # scripted group (container) (typed FeaturePython)
  n = 3
  ref = H_element
FEATURE [App::DocumentObjectGroupPython] Cl_element019  label="Cl_element : 009"  # scripted group (container) (typed FeaturePython)
  n = 1
  ref = Cl_element
FEATURE [App::DocumentObjectGroupPython] G4_POLYVINYL_CHLORIDE  # scripted group (container) (typed FeaturePython)
  Dunit = g/cm3
  Dvalue = 1.3
  Group = -> [C_element092,H_element084,Cl_element019]
  conduct = 2
  density = 1
  expand = 3
  formula = G4_POLYVINYL_CHLORIDE
  name = G4_POLYVINYL_CHLORIDE
  specific = 4
FEATURE [App::DocumentObjectGroupPython] C_element093  label="C_element : 051"  # scripted group (container) (typed FeaturePython)
  n = 2
  ref = C_element
FEATURE [App::DocumentObjectGroupPython] H_element085  label="H_element : 047"  # scripted group (container) (typed FeaturePython)
  n = 2
  ref = H_element
FEATURE [App::DocumentObjectGroupPython] Cl_element020  label="Cl_element : 010"  # scripted group (container) (typed FeaturePython)
  n = 2
  ref = Cl_element
FEATURE [App::DocumentObjectGroupPython] G4_POLYVINYLIDENE_CHLORIDE  # scripted group (container) (typed FeaturePython)
  Dunit = g/cm3
  Dvalue = 1.7
  Group = -> [C_element093,H_element085,Cl_element020]
  conduct = 2
  density = 1
  expand = 3
  formula = G4_POLYVINYLIDENE_CHLORIDE
  name = G4_POLYVINYLIDENE_CHLORIDE
  specific = 4
FEATURE [App::DocumentObjectGroupPython] C_element094  label="C_element : 052"  # scripted group (container) (typed FeaturePython)
  n = 2
  ref = C_element
FEATURE [App::DocumentObjectGroupPython] H_element086  label="H_element : 048"  # scripted group (container) (typed FeaturePython)
  n = 2
  ref = H_element
FEATURE [App::DocumentObjectGroupPython] F_element016  label="F_element : 007"  # scripted group (container) (typed FeaturePython)
  n = 2
  ref = F_element
FEATURE [App::DocumentObjectGroupPython] G4_POLYVINYLIDENE_FLUORIDE  # scripted group (container) (typed FeaturePython)
  Dunit = g/cm3
  Dvalue = 1.76
  Group = -> [C_element094,H_element086,F_element016]
  conduct = 2
  density = 1
  expand = 3
  formula = G4_POLYVINYLIDENE_FLUORIDE
  name = G4_POLYVINYLIDENE_FLUORIDE
  specific = 4
FEATURE [App::DocumentObjectGroupPython] C_element095  label="C_element : 053"  # scripted group (container) (typed FeaturePython)
  n = 6
  ref = C_element
FEATURE [App::DocumentObjectGroupPython] H_element087  label="H_element : 9"  # scripted group (container) (typed FeaturePython)
  n = 9
  ref = H_element
FEATURE [App::DocumentObjectGroupPython] N_element037  label="N_element : 016"  # scripted group (container) (typed FeaturePython)
  n = 1
  ref = N_element
FEATURE [App::DocumentObjectGroupPython] O_element084  label="O_element : 045"  # scripted group (container) (typed FeaturePython)
  n = 1
  ref = O_element
FEATURE [App::DocumentObjectGroupPython] G4_POLYVINYL_PYRROLIDONE  # scripted group (container) (typed FeaturePython)
  Dunit = g/cm3
  Dvalue = 1.25
  Group = -> [C_element095,H_element087,N_element037,O_element084]
  conduct = 2
  density = 1
  expand = 3
  formula = G4_POLYVINYL_PYRROLIDONE
  name = G4_POLYVINYL_PYRROLIDONE
  specific = 4
FEATURE [App::DocumentObjectGroupPython] K_element008  label="K_element : 1"  # scripted group (container) (typed FeaturePython)
  n = 1
  ref = K_element
FEATURE [App::DocumentObjectGroupPython] I_element006  label="I_element : 003"  # scripted group (container) (typed FeaturePython)
  n = 1
  ref = I_element
FEATURE [App::DocumentObjectGroupPython] G4_POTASSIUM_IODIDE  # scripted group (container) (typed FeaturePython)
  Dunit = g/cm3
  Dvalue = 3.13
  Group = -> [K_element008,I_element006]
  conduct = 2
  density = 1
  expand = 3
  formula = G4_POTASSIUM_IODIDE
  name = G4_POTASSIUM_IODIDE
  specific = 4
FEATURE [App::DocumentObjectGroupPython] K_element009  label="K_element : 2"  # scripted group (container) (typed FeaturePython)
  n = 2
  ref = K_element
FEATURE [App::DocumentObjectGroupPython] O_element085  label="O_element : 046"  # scripted group (container) (typed FeaturePython)
  n = 1
  ref = O_element
FEATURE [App::DocumentObjectGroupPython] G4_POTASSIUM_OXIDE  # scripted group (container) (typed FeaturePython)
  Dunit = g/cm3
  Dvalue = 2.32
  Group = -> [K_element009,O_element085]
  conduct = 2
  density = 1
  expand = 3
  formula = G4_POTASSIUM_OXIDE
  name = G4_POTASSIUM_OXIDE
  specific = 4
FEATURE [App::DocumentObjectGroupPython] C_element096  label="C_element : 054"  # scripted group (container) (typed FeaturePython)
  n = 3
  ref = C_element
FEATURE [App::DocumentObjectGroupPython] H_element088  label="H_element : 049"  # scripted group (container) (typed FeaturePython)
  n = 8
  ref = H_element
FEATURE [App::DocumentObjectGroupPython] G4_PROPANE  # scripted group (container) (typed FeaturePython)
  Dunit = g/cm3
  Dvalue = 0.00187939
  Group = -> [C_element096,H_element088]
  conduct = 2
  density = 1
  expand = 3
  formula = G4_PROPANE
  name = G4_PROPANE
  specific = 4
FEATURE [App::DocumentObjectGroupPython] C_element097  label="C_element : 055"  # scripted group (container) (typed FeaturePython)
  n = 3
  ref = C_element
FEATURE [App::DocumentObjectGroupPython] H_element089  label="H_element : 050"  # scripted group (container) (typed FeaturePython)
  n = 8
  ref = H_element
FEATURE [App::DocumentObjectGroupPython] G4_lPROPANE  # scripted group (container) (typed FeaturePython)
  Dunit = g/cm3
  Dvalue = 0.43
  Group = -> [C_element097,H_element089]
  conduct = 2
  density = 1
  expand = 3
  formula = G4_lPROPANE
  name = G4_lPROPANE
  specific = 4
FEATURE [App::DocumentObjectGroupPython] C_element098  label="C_element : 056"  # scripted group (container) (typed FeaturePython)
  n = 3
  ref = C_element
FEATURE [App::DocumentObjectGroupPython] H_element090  label="H_element : 051"  # scripted group (container) (typed FeaturePython)
  n = 8
  ref = H_element
FEATURE [App::DocumentObjectGroupPython] O_element086  label="O_element : 047"  # scripted group (container) (typed FeaturePython)
  n = 1
  ref = O_element
FEATURE [App::DocumentObjectGroupPython] G4_N_PROPYL_ALCOHOL  label="G4_N-PROPYL_ALCOHOL"  # scripted group (container) (typed FeaturePython)
  Dunit = g/cm3
  Dvalue = 0.8035
  Group = -> [C_element098,H_element090,O_element086]
  conduct = 2
  density = 1
  expand = 3
  formula = G4_N-PROPYL_ALCOHOL
  name = G4_N-PROPYL_ALCOHOL
  specific = 4
FEATURE [App::DocumentObjectGroupPython] C_element099  label="C_element : 057"  # scripted group (container) (typed FeaturePython)
  n = 5
  ref = C_element
FEATURE [App::DocumentObjectGroupPython] H_element091  label="H_element : 052"  # scripted group (container) (typed FeaturePython)
  n = 5
  ref = H_element
FEATURE [App::DocumentObjectGroupPython] N_element038  label="N_element : 017"  # scripted group (container) (typed FeaturePython)
  n = 1
  ref = N_element
FEATURE [App::DocumentObjectGroupPython] G4_PYRIDINE  # scripted group (container) (typed FeaturePython)
  Dunit = g/cm3
  Dvalue = 0.9819
  Group = -> [C_element099,H_element091,N_element038]
  conduct = 2
  density = 1
  expand = 3
  formula = G4_PYRIDINE
  name = G4_PYRIDINE
  specific = 4
FEATURE [App::DocumentObjectGroupPython] H_element092  label="H_element : 0.144"  # scripted group (container) (typed FeaturePython)
  n = 0.143711
FEATURE [App::DocumentObjectGroupPython] C_element100  label="C_element : 0.856"  # scripted group (container) (typed FeaturePython)
  n = 0.856289
FEATURE [App::DocumentObjectGroupPython] G4_RUBBER_BUTYL  # scripted group (container) (typed FeaturePython)
  Dunit = g/cm3
  Dvalue = 0.92
  Group = -> [H_element092,C_element100]
  conduct = 2
  density = 1
  expand = 3
  formula = G4_RUBBER_BUTYL
  name = G4_RUBBER_BUTYL
  specific = 4
FEATURE [App::DocumentObjectGroupPython] H_element093  label="H_element : 0.118"  # scripted group (container) (typed FeaturePython)
  n = 0.118371
FEATURE [App::DocumentObjectGroupPython] C_element101  label="C_element : 0.882"  # scripted group (container) (typed FeaturePython)
  n = 0.881629
FEATURE [App::DocumentObjectGroupPython] G4_RUBBER_NATURAL  # scripted group (container) (typed FeaturePython)
  Dunit = g/cm3
  Dvalue = 0.92
  Group = -> [H_element093,C_element101]
  conduct = 2
  density = 1
  expand = 3
  formula = G4_RUBBER_NATURAL
  name = G4_RUBBER_NATURAL
  specific = 4
FEATURE [App::DocumentObjectGroupPython] H_element094  label="H_element : 0.145"  # scripted group (container) (typed FeaturePython)
  n = 0.05692
FEATURE [App::DocumentObjectGroupPython] C_element102  label="C_element : 0.543"  # scripted group (container) (typed FeaturePython)
  n = 0.542646
FEATURE [App::DocumentObjectGroupPython] Cl_element021  label="Cl_element : 0.400"  # scripted group (container) (typed FeaturePython)
  n = 0.400434
FEATURE [App::DocumentObjectGroupPython] G4_RUBBER_NEOPRENE  # scripted group (container) (typed FeaturePython)
  Dunit = g/cm3
  Dvalue = 1.23
  Group = -> [H_element094,C_element102,Cl_element021]
  conduct = 2
  density = 1
  expand = 3
  formula = G4_RUBBER_NEOPRENE
  name = G4_RUBBER_NEOPRENE
  specific = 4
FEATURE [App::DocumentObjectGroupPython] Si_element006  label="Si_element : 1"  # scripted group (container) (typed FeaturePython)
  n = 1
  ref = Si_element
FEATURE [App::DocumentObjectGroupPython] O_element087  label="O_element : 048"  # scripted group (container) (typed FeaturePython)
  n = 2
  ref = O_element
FEATURE [App::DocumentObjectGroupPython] G4_SILICON_DIOXIDE  # scripted group (container) (typed FeaturePython)
  Dunit = g/cm3
  Dvalue = 2.32
  Group = -> [Si_element006,O_element087]
  conduct = 2
  density = 1
  expand = 3
  formula = G4_SILICON_DIOXIDE
  name = G4_SILICON_DIOXIDE
  specific = 4
FEATURE [App::DocumentObjectGroupPython] Ag_element002  label="Ag_element : 1"  # scripted group (container) (typed FeaturePython)
  n = 1
  ref = Ag_element
FEATURE [App::DocumentObjectGroupPython] Br_element005  label="Br_element : 003"  # scripted group (container) (typed FeaturePython)
  n = 1
  ref = Br_element
FEATURE [App::DocumentObjectGroupPython] G4_SILVER_BROMIDE  # scripted group (container) (typed FeaturePython)
  Dunit = g/cm3
  Dvalue = 6.473
  Group = -> [Ag_element002,Br_element005]
  conduct = 2
  density = 1
  expand = 3
  formula = G4_SILVER_BROMIDE
  name = G4_SILVER_BROMIDE
  specific = 4
FEATURE [App::DocumentObjectGroupPython] Ag_element003  label="Ag_element : 002"  # scripted group (container) (typed FeaturePython)
  n = 1
  ref = Ag_element
FEATURE [App::DocumentObjectGroupPython] Cl_element022  label="Cl_element : 011"  # scripted group (container) (typed FeaturePython)
  n = 1
  ref = Cl_element
FEATURE [App::DocumentObjectGroupPython] G4_SILVER_CHLORIDE  # scripted group (container) (typed FeaturePython)
  Dunit = g/cm3
  Dvalue = 5.56
  Group = -> [Ag_element003,Cl_element022]
  conduct = 2
  density = 1
  expand = 3
  formula = G4_SILVER_CHLORIDE
  name = G4_SILVER_CHLORIDE
  specific = 4
FEATURE [App::DocumentObjectGroupPython] Br_element006  label="Br_element : 0.423"  # scripted group (container) (typed FeaturePython)
  n = 0.422895
FEATURE [App::DocumentObjectGroupPython] Ag_element004  label="Ag_element : 0.574"  # scripted group (container) (typed FeaturePython)
  n = 0.573748
FEATURE [App::DocumentObjectGroupPython] I_element007  label="I_element : 0.649"  # scripted group (container) (typed FeaturePython)
  n = 0.003357
FEATURE [App::DocumentObjectGroupPython] G4_SILVER_HALIDES  # scripted group (container) (typed FeaturePython)
  Dunit = g/cm3
  Dvalue = 6.47
  Group = -> [Br_element006,Ag_element004,I_element007]
  conduct = 2
  density = 1
  expand = 3
  formula = G4_SILVER_HALIDES
  name = G4_SILVER_HALIDES
  specific = 4
FEATURE [App::DocumentObjectGroupPython] Ag_element005  label="Ag_element : 003"  # scripted group (container) (typed FeaturePython)
  n = 1
  ref = Ag_element
FEATURE [App::DocumentObjectGroupPython] I_element008  label="I_element : 004"  # scripted group (container) (typed FeaturePython)
  n = 1
  ref = I_element
FEATURE [App::DocumentObjectGroupPython] G4_SILVER_IODIDE  # scripted group (container) (typed FeaturePython)
  Dunit = g/cm3
  Dvalue = 6.01
  Group = -> [Ag_element005,I_element008]
  conduct = 2
  density = 1
  expand = 3
  formula = G4_SILVER_IODIDE
  name = G4_SILVER_IODIDE
  specific = 4
FEATURE [App::DocumentObjectGroupPython] H_element095  label="H_element : 0.100"  # scripted group (container) (typed FeaturePython)
  n = 0.1
FEATURE [App::DocumentObjectGroupPython] C_element103  label="C_element : 0.204"  # scripted group (container) (typed FeaturePython)
  n = 0.204
FEATURE [App::DocumentObjectGroupPython] N_element039  label="N_element : 0.759"  # scripted group (container) (typed FeaturePython)
  n = 0.042
FEATURE [App::DocumentObjectGroupPython] O_element088  label="O_element : 0.645"  # scripted group (container) (typed FeaturePython)
  n = 0.645
FEATURE [App::DocumentObjectGroupPython] Na_element013  label="Na_element : 0.100"  # scripted group (container) (typed FeaturePython)
  n = 0.002
FEATURE [App::DocumentObjectGroupPython] P_element009  label="P_element : 0.107"  # scripted group (container) (typed FeaturePython)
  n = 0.001
FEATURE [App::DocumentObjectGroupPython] S_element020  label="S_element : 0.021"  # scripted group (container) (typed FeaturePython)
  n = 0.002
FEATURE [App::DocumentObjectGroupPython] Cl_element023  label="Cl_element : 0.590"  # scripted group (container) (typed FeaturePython)
  n = 0.003
FEATURE [App::DocumentObjectGroupPython] K_element010  label="K_element : 0.001"  # scripted group (container) (typed FeaturePython)
  n = 0.001
FEATURE [App::DocumentObjectGroupPython] G4_SKIN_ICRP  # scripted group (container) (typed FeaturePython)
  Dunit = g/cm3
  Dvalue = 1.09
  Group = -> [H_element095,C_element103,N_element039,O_element088,Na_element013,P_element009,S_element020,Cl_element023,K_element010]
  conduct = 2
  density = 1
  expand = 3
  formula = G4_SKIN_ICRP
  name = G4_SKIN_ICRP
  specific = 4
FEATURE [App::DocumentObjectGroupPython] Na_element014  label="Na_element : 2"  # scripted group (container) (typed FeaturePython)
  n = 2
  ref = Na_element
FEATURE [App::DocumentObjectGroupPython] C_element104  label="C_element : 058"  # scripted group (container) (typed FeaturePython)
  n = 1
  ref = C_element
FEATURE [App::DocumentObjectGroupPython] O_element089  label="O_element : 049"  # scripted group (container) (typed FeaturePython)
  n = 3
  ref = O_element
FEATURE [App::DocumentObjectGroupPython] G4_SODIUM_CARBONATE  # scripted group (container) (typed FeaturePython)
  Dunit = g/cm3
  Dvalue = 2.532
  Group = -> [Na_element014,C_element104,O_element089]
  conduct = 2
  density = 1
  expand = 3
  formula = G4_SODIUM_CARBONATE
  name = G4_SODIUM_CARBONATE
  specific = 4
FEATURE [App::DocumentObjectGroupPython] Na_element015  label="Na_element : 1"  # scripted group (container) (typed FeaturePython)
  n = 1
  ref = Na_element
FEATURE [App::DocumentObjectGroupPython] I_element009  label="I_element : 005"  # scripted group (container) (typed FeaturePython)
  n = 1
  ref = I_element
FEATURE [App::DocumentObjectGroupPython] G4_SODIUM_IODIDE  # scripted group (container) (typed FeaturePython)
  Dunit = g/cm3
  Dvalue = 3.667
  Group = -> [Na_element015,I_element009]
  conduct = 2
  density = 1
  expand = 3
  formula = G4_SODIUM_IODIDE
  name = G4_SODIUM_IODIDE
  specific = 4
FEATURE [App::DocumentObjectGroupPython] Na_element016  label="Na_element : 003"  # scripted group (container) (typed FeaturePython)
  n = 2
  ref = Na_element
FEATURE [App::DocumentObjectGroupPython] O_element090  label="O_element : 050"  # scripted group (container) (typed FeaturePython)
  n = 1
  ref = O_element
FEATURE [App::DocumentObjectGroupPython] G4_SODIUM_MONOXIDE  # scripted group (container) (typed FeaturePython)
  Dunit = g/cm3
  Dvalue = 2.27
  Group = -> [Na_element016,O_element090]
  conduct = 2
  density = 1
  expand = 3
  formula = G4_SODIUM_MONOXIDE
  name = G4_SODIUM_MONOXIDE
  specific = 4
FEATURE [App::DocumentObjectGroupPython] Na_element017  label="Na_element : 004"  # scripted group (container) (typed FeaturePython)
  n = 1
  ref = Na_element
FEATURE [App::DocumentObjectGroupPython] N_element040  label="N_element : 018"  # scripted group (container) (typed FeaturePython)
  n = 1
  ref = N_element
FEATURE [App::DocumentObjectGroupPython] O_element091  label="O_element : 051"  # scripted group (container) (typed FeaturePython)
  n = 3
  ref = O_element
FEATURE [App::DocumentObjectGroupPython] G4_SODIUM_NITRATE  # scripted group (container) (typed FeaturePython)
  Dunit = g/cm3
  Dvalue = 2.261
  Group = -> [Na_element017,N_element040,O_element091]
  conduct = 2
  density = 1
  expand = 3
  formula = G4_SODIUM_NITRATE
  name = G4_SODIUM_NITRATE
  specific = 4
FEATURE [App::DocumentObjectGroupPython] C_element105  label="C_element : 059"  # scripted group (container) (typed FeaturePython)
  n = 14
  ref = C_element
FEATURE [App::DocumentObjectGroupPython] H_element096  label="H_element : 053"  # scripted group (container) (typed FeaturePython)
  n = 12
  ref = H_element
FEATURE [App::DocumentObjectGroupPython] G4_STILBENE  # scripted group (container) (typed FeaturePython)
  Dunit = g/cm3
  Dvalue = 0.9707
  Group = -> [C_element105,H_element096]
  conduct = 2
  density = 1
  expand = 3
  formula = G4_STILBENE
  name = G4_STILBENE
  specific = 4
FEATURE [App::DocumentObjectGroupPython] C_element106  label="C_element : 12"  # scripted group (container) (typed FeaturePython)
  n = 12
  ref = C_element
FEATURE [App::DocumentObjectGroupPython] H_element097  label="H_element : 22"  # scripted group (container) (typed FeaturePython)
  n = 22
  ref = H_element
FEATURE [App::DocumentObjectGroupPython] O_element092  label="O_element : 11"  # scripted group (container) (typed FeaturePython)
  n = 11
  ref = O_element
FEATURE [App::DocumentObjectGroupPython] G4_SUCROSE  # scripted group (container) (typed FeaturePython)
  Dunit = g/cm3
  Dvalue = 1.5805
  Group = -> [C_element106,H_element097,O_element092]
  conduct = 2
  density = 1
  expand = 3
  formula = G4_SUCROSE
  name = G4_SUCROSE
  specific = 4
FEATURE [App::DocumentObjectGroupPython] C_element107  label="C_element : 18"  # scripted group (container) (typed FeaturePython)
  n = 18
  ref = C_element
FEATURE [App::DocumentObjectGroupPython] H_element098  label="H_element : 054"  # scripted group (container) (typed FeaturePython)
  n = 14
  ref = H_element
FEATURE [App::DocumentObjectGroupPython] G4_TERPHENYL  # scripted group (container) (typed FeaturePython)
  Dunit = g/cm3
  Dvalue = 1.24
  Group = -> [C_element107,H_element098]
  conduct = 2
  density = 1
  expand = 3
  formula = G4_TERPHENYL
  name = G4_TERPHENYL
  specific = 4
FEATURE [App::DocumentObjectGroupPython] H_element099  label="H_element : 0.146"  # scripted group (container) (typed FeaturePython)
  n = 0.106
FEATURE [App::DocumentObjectGroupPython] C_element108  label="C_element : 0.883"  # scripted group (container) (typed FeaturePython)
  n = 0.099
FEATURE [App::DocumentObjectGroupPython] N_element041  label="N_element : 0.020"  # scripted group (container) (typed FeaturePython)
  n = 0.02
FEATURE [App::DocumentObjectGroupPython] O_element093  label="O_element : 0.766"  # scripted group (container) (typed FeaturePython)
  n = 0.766
FEATURE [App::DocumentObjectGroupPython] Na_element018  label="Na_element : 0.101"  # scripted group (container) (typed FeaturePython)
  n = 0.002
FEATURE [App::DocumentObjectGroupPython] P_element010  label="P_element : 0.108"  # scripted group (container) (typed FeaturePython)
  n = 0.001
FEATURE [App::DocumentObjectGroupPython] S_element021  label="S_element : 0.022"  # scripted group (container) (typed FeaturePython)
  n = 0.002
FEATURE [App::DocumentObjectGroupPython] Cl_element024  label="Cl_element : 0.002"  # scripted group (container) (typed FeaturePython)
  n = 0.002
FEATURE [App::DocumentObjectGroupPython] K_element011  label="K_element : 0.017"  # scripted group (container) (typed FeaturePython)
  n = 0.002
FEATURE [App::DocumentObjectGroupPython] G4_TESTIS_ICRP  # scripted group (container) (typed FeaturePython)
  Dunit = g/cm3
  Dvalue = 1.04
  Group = -> [H_element099,C_element108,N_element041,O_element093,Na_element018,P_element010,S_element021,Cl_element024,K_element011]
  conduct = 2
  density = 1
  expand = 3
  formula = G4_TESTIS_ICRP
  name = G4_TESTIS_ICRP
  specific = 4
FEATURE [App::DocumentObjectGroupPython] C_element109  label="C_element : 060"  # scripted group (container) (typed FeaturePython)
  n = 2
  ref = C_element
FEATURE [App::DocumentObjectGroupPython] Cl_element025  label="Cl_element : 012"  # scripted group (container) (typed FeaturePython)
  n = 4
  ref = Cl_element
FEATURE [App::DocumentObjectGroupPython] G4_TETRACHLOROETHYLENE  # scripted group (container) (typed FeaturePython)
  Dunit = g/cm3
  Dvalue = 1.625
  Group = -> [C_element109,Cl_element025]
  conduct = 2
  density = 1
  expand = 3
  formula = G4_TETRACHLOROETHYLENE
  name = G4_TETRACHLOROETHYLENE
  specific = 4
FEATURE [App::DocumentObjectGroupPython] Tl_element001  label="Tl_element : 1"  # scripted group (container) (typed FeaturePython)
  n = 1
  ref = Tl_element
FEATURE [App::DocumentObjectGroupPython] Cl_element026  label="Cl_element : 013"  # scripted group (container) (typed FeaturePython)
  n = 1
  ref = Cl_element
FEATURE [App::DocumentObjectGroupPython] G4_THALLIUM_CHLORIDE  # scripted group (container) (typed FeaturePython)
  Dunit = g/cm3
  Dvalue = 7.004
  Group = -> [Tl_element001,Cl_element026]
  conduct = 2
  density = 1
  expand = 3
  formula = G4_THALLIUM_CHLORIDE
  name = G4_THALLIUM_CHLORIDE
  specific = 4
FEATURE [App::DocumentObjectGroupPython] H_element100  label="H_element : 0.147"  # scripted group (container) (typed FeaturePython)
  n = 0.105
FEATURE [App::DocumentObjectGroupPython] C_element110  label="C_element : 0.256"  # scripted group (container) (typed FeaturePython)
  n = 0.256
FEATURE [App::DocumentObjectGroupPython] N_element042  label="N_element : 0.760"  # scripted group (container) (typed FeaturePython)
  n = 0.027
FEATURE [App::DocumentObjectGroupPython] O_element094  label="O_element : 0.602"  # scripted group (container) (typed FeaturePython)
  n = 0.602
FEATURE [App::DocumentObjectGroupPython] Na_element019  label="Na_element : 0.102"  # scripted group (container) (typed FeaturePython)
  n = 0.001
FEATURE [App::DocumentObjectGroupPython] P_element011  label="P_element : 0.109"  # scripted group (container) (typed FeaturePython)
  n = 0.002
FEATURE [App::DocumentObjectGroupPython] S_element022  label="S_element : 0.023"  # scripted group (container) (typed FeaturePython)
  n = 0.003
FEATURE [App::DocumentObjectGroupPython] Cl_element027  label="Cl_element : 0.591"  # scripted group (container) (typed FeaturePython)
  n = 0.002
FEATURE [App::DocumentObjectGroupPython] K_element012  label="K_element : 0.018"  # scripted group (container) (typed FeaturePython)
  n = 0.002
FEATURE [App::DocumentObjectGroupPython] G4_TISSUE_SOFT_ICRP  # scripted group (container) (typed FeaturePython)
  Dunit = g/cm3
  Dvalue = 1.03
  Group = -> [H_element100,C_element110,N_element042,O_element094,Na_element019,P_element011,S_element022,Cl_element027,K_element012]
  conduct = 2
  density = 1
  expand = 3
  formula = G4_TISSUE_SOFT_ICRP
  name = G4_TISSUE_SOFT_ICRP
  specific = 4
FEATURE [App::DocumentObjectGroupPython] H_element101  label="H_element : 0.148"  # scripted group (container) (typed FeaturePython)
  n = 0.101
FEATURE [App::DocumentObjectGroupPython] C_element111  label="C_element : 0.111"  # scripted group (container) (typed FeaturePython)
  n = 0.111
FEATURE [App::DocumentObjectGroupPython] N_element043  label="N_element : 0.026"  # scripted group (container) (typed FeaturePython)
  n = 0.026
FEATURE [App::DocumentObjectGroupPython] O_element095  label="O_element : 0.762"  # scripted group (container) (typed FeaturePython)
  n = 0.762
FEATURE [App::DocumentObjectGroupPython] G4_TISSUE_SOFT_ICRU_4  label="G4_TISSUE_SOFT_ICRU-4"  # scripted group (container) (typed FeaturePython)
  Dunit = g/cm3
  Dvalue = 1
  Group = -> [H_element101,C_element111,N_element043,O_element095]
  conduct = 2
  density = 1
  expand = 3
  formula = G4_TISSUE_SOFT_ICRU-4
  name = G4_TISSUE_SOFT_ICRU-4
  specific = 4
FEATURE [App::DocumentObjectGroupPython] H_element102  label="H_element : 0.149"  # scripted group (container) (typed FeaturePython)
  n = 0.101869
FEATURE [App::DocumentObjectGroupPython] C_element112  label="C_element : 0.456"  # scripted group (container) (typed FeaturePython)
  n = 0.456179
FEATURE [App::DocumentObjectGroupPython] N_element044  label="N_element : 0.761"  # scripted group (container) (typed FeaturePython)
  n = 0.035172
FEATURE [App::DocumentObjectGroupPython] O_element096  label="O_element : 0.407"  # scripted group (container) (typed FeaturePython)
  n = 0.40678
FEATURE [App::DocumentObjectGroupPython] G4_TISSUE_METHANE  label="G4_TISSUE-METHANE"  # scripted group (container) (typed FeaturePython)
  Dunit = g/cm3
  Dvalue = 0.00106409
  Group = -> [H_element102,C_element112,N_element044,O_element096]
  conduct = 2
  density = 1
  expand = 3
  formula = G4_TISSUE-METHANE
  name = G4_TISSUE-METHANE
  specific = 4
FEATURE [App::DocumentObjectGroupPython] H_element103  label="H_element : 0.103"  # scripted group (container) (typed FeaturePython)
  n = 0.102672
FEATURE [App::DocumentObjectGroupPython] C_element113  label="C_element : 0.569"  # scripted group (container) (typed FeaturePython)
  n = 0.56894
FEATURE [App::DocumentObjectGroupPython] N_element045  label="N_element : 0.762"  # scripted group (container) (typed FeaturePython)
  n = 0.035022
FEATURE [App::DocumentObjectGroupPython] O_element097  label="O_element : 0.293"  # scripted group (container) (typed FeaturePython)
  n = 0.293366
FEATURE [App::DocumentObjectGroupPython] G4_TISSUE_PROPANE  label="G4_TISSUE-PROPANE"  # scripted group (container) (typed FeaturePython)
  Dunit = g/cm3
  Dvalue = 0.00182628
  Group = -> [H_element103,C_element113,N_element045,O_element097]
  conduct = 2
  density = 1
  expand = 3
  formula = G4_TISSUE-PROPANE
  name = G4_TISSUE-PROPANE
  specific = 4
FEATURE [App::DocumentObjectGroupPython] Ti_element003  label="Ti_element : 1"  # scripted group (container) (typed FeaturePython)
  n = 1
  ref = Ti_element
FEATURE [App::DocumentObjectGroupPython] O_element098  label="O_element : 052"  # scripted group (container) (typed FeaturePython)
  n = 2
  ref = O_element
FEATURE [App::DocumentObjectGroupPython] G4_TITANIUM_DIOXIDE  # scripted group (container) (typed FeaturePython)
  Dunit = g/cm3
  Dvalue = 4.26
  Group = -> [Ti_element003,O_element098]
  conduct = 2
  density = 1
  expand = 3
  formula = G4_TITANIUM_DIOXIDE
  name = G4_TITANIUM_DIOXIDE
  specific = 4
FEATURE [App::DocumentObjectGroupPython] C_element114  label="C_element : 061"  # scripted group (container) (typed FeaturePython)
  n = 7
  ref = C_element
FEATURE [App::DocumentObjectGroupPython] H_element104  label="H_element : 055"  # scripted group (container) (typed FeaturePython)
  n = 8
  ref = H_element
FEATURE [App::DocumentObjectGroupPython] G4_TOLUENE  # scripted group (container) (typed FeaturePython)
  Dunit = g/cm3
  Dvalue = 0.8669
  Group = -> [C_element114,H_element104]
  conduct = 2
  density = 1
  expand = 3
  formula = G4_TOLUENE
  name = G4_TOLUENE
  specific = 4
FEATURE [App::DocumentObjectGroupPython] C_element115  label="C_element : 062"  # scripted group (container) (typed FeaturePython)
  n = 2
  ref = C_element
FEATURE [App::DocumentObjectGroupPython] H_element105  label="H_element : 056"  # scripted group (container) (typed FeaturePython)
  n = 1
  ref = H_element
FEATURE [App::DocumentObjectGroupPython] Cl_element028  label="Cl_element : 014"  # scripted group (container) (typed FeaturePython)
  n = 3
  ref = Cl_element
FEATURE [App::DocumentObjectGroupPython] G4_TRICHLOROETHYLENE  # scripted group (container) (typed FeaturePython)
  Dunit = g/cm3
  Dvalue = 1.46
  Group = -> [C_element115,H_element105,Cl_element028]
  conduct = 2
  density = 1
  expand = 3
  formula = G4_TRICHLOROETHYLENE
  name = G4_TRICHLOROETHYLENE
  specific = 4
FEATURE [App::DocumentObjectGroupPython] C_element116  label="C_element : 063"  # scripted group (container) (typed FeaturePython)
  n = 6
  ref = C_element
FEATURE [App::DocumentObjectGroupPython] H_element106  label="H_element : 15"  # scripted group (container) (typed FeaturePython)
  n = 15
  ref = H_element
FEATURE [App::DocumentObjectGroupPython] O_element099  label="O_element : 053"  # scripted group (container) (typed FeaturePython)
  n = 4
  ref = O_element
FEATURE [App::DocumentObjectGroupPython] P_element012  label="P_element : 1"  # scripted group (container) (typed FeaturePython)
  n = 1
  ref = P_element
FEATURE [App::DocumentObjectGroupPython] G4_TRIETHYL_PHOSPHATE  # scripted group (container) (typed FeaturePython)
  Dunit = g/cm3
  Dvalue = 1.07
  Group = -> [C_element116,H_element106,O_element099,P_element012]
  conduct = 2
  density = 1
  expand = 3
  formula = G4_TRIETHYL_PHOSPHATE
  name = G4_TRIETHYL_PHOSPHATE
  specific = 4
FEATURE [App::DocumentObjectGroupPython] W_element003  label="W_element : 003"  # scripted group (container) (typed FeaturePython)
  n = 1
  ref = W_element
FEATURE [App::DocumentObjectGroupPython] F_element017  label="F_element : 6"  # scripted group (container) (typed FeaturePython)
  n = 6
  ref = F_element
FEATURE [App::DocumentObjectGroupPython] G4_TUNGSTEN_HEXAFLUORIDE  # scripted group (container) (typed FeaturePython)
  Dunit = g/cm3
  Dvalue = 2.4
  Group = -> [W_element003,F_element017]
  conduct = 2
  density = 1
  expand = 3
  formula = G4_TUNGSTEN_HEXAFLUORIDE
  name = G4_TUNGSTEN_HEXAFLUORIDE
  specific = 4
FEATURE [App::DocumentObjectGroupPython] U_element001  label="U_element : 1"  # scripted group (container) (typed FeaturePython)
  n = 1
  ref = U_element
FEATURE [App::DocumentObjectGroupPython] C_element117  label="C_element : 064"  # scripted group (container) (typed FeaturePython)
  n = 2
  ref = C_element
FEATURE [App::DocumentObjectGroupPython] G4_URANIUM_DICARBIDE  # scripted group (container) (typed FeaturePython)
  Dunit = g/cm3
  Dvalue = 11.28
  Group = -> [U_element001,C_element117]
  conduct = 2
  density = 1
  expand = 3
  formula = G4_URANIUM_DICARBIDE
  name = G4_URANIUM_DICARBIDE
  specific = 4
FEATURE [App::DocumentObjectGroupPython] U_element002  label="U_element : 002"  # scripted group (container) (typed FeaturePython)
  n = 1
  ref = U_element
FEATURE [App::DocumentObjectGroupPython] C_element118  label="C_element : 065"  # scripted group (container) (typed FeaturePython)
  n = 1
  ref = C_element
FEATURE [App::DocumentObjectGroupPython] G4_URANIUM_MONOCARBIDE  # scripted group (container) (typed FeaturePython)
  Dunit = g/cm3
  Dvalue = 13.63
  Group = -> [U_element002,C_element118]
  conduct = 2
  density = 1
  expand = 3
  formula = G4_URANIUM_MONOCARBIDE
  name = G4_URANIUM_MONOCARBIDE
  specific = 4
FEATURE [App::DocumentObjectGroupPython] U_element003  label="U_element : 003"  # scripted group (container) (typed FeaturePython)
  n = 1
  ref = U_element
FEATURE [App::DocumentObjectGroupPython] O_element100  label="O_element : 054"  # scripted group (container) (typed FeaturePython)
  n = 2
  ref = O_element
FEATURE [App::DocumentObjectGroupPython] G4_URANIUM_OXIDE  # scripted group (container) (typed FeaturePython)
  Dunit = g/cm3
  Dvalue = 10.96
  Group = -> [U_element003,O_element100]
  conduct = 2
  density = 1
  expand = 3
  formula = G4_URANIUM_OXIDE
  name = G4_URANIUM_OXIDE
  specific = 4
FEATURE [App::DocumentObjectGroupPython] C_element119  label="C_element : 066"  # scripted group (container) (typed FeaturePython)
  n = 1
  ref = C_element
FEATURE [App::DocumentObjectGroupPython] H_element107  label="H_element : 057"  # scripted group (container) (typed FeaturePython)
  n = 4
  ref = H_element
FEATURE [App::DocumentObjectGroupPython] N_element046  label="N_element : 019"  # scripted group (container) (typed FeaturePython)
  n = 2
  ref = N_element
FEATURE [App::DocumentObjectGroupPython] O_element101  label="O_element : 055"  # scripted group (container) (typed FeaturePython)
  n = 1
  ref = O_element
FEATURE [App::DocumentObjectGroupPython] G4_UREA  # scripted group (container) (typed FeaturePython)
  Dunit = g/cm3
  Dvalue = 1.323
  Group = -> [C_element119,H_element107,N_element046,O_element101]
  conduct = 2
  density = 1
  expand = 3
  formula = G4_UREA
  name = G4_UREA
  specific = 4
FEATURE [App::DocumentObjectGroupPython] C_element120  label="C_element : 067"  # scripted group (container) (typed FeaturePython)
  n = 5
  ref = C_element
FEATURE [App::DocumentObjectGroupPython] H_element108  label="H_element : 058"  # scripted group (container) (typed FeaturePython)
  n = 11
  ref = H_element
FEATURE [App::DocumentObjectGroupPython] N_element047  label="N_element : 020"  # scripted group (container) (typed FeaturePython)
  n = 1
  ref = N_element
FEATURE [App::DocumentObjectGroupPython] O_element102  label="O_element : 056"  # scripted group (container) (typed FeaturePython)
  n = 2
  ref = O_element
FEATURE [App::DocumentObjectGroupPython] G4_VALINE  # scripted group (container) (typed FeaturePython)
  Dunit = g/cm3
  Dvalue = 1.23
  Group = -> [C_element120,H_element108,N_element047,O_element102]
  conduct = 2
  density = 1
  expand = 3
  formula = G4_VALINE
  name = G4_VALINE
  specific = 4
FEATURE [App::DocumentObjectGroupPython] H_element109  label="H_element : 0.009"  # scripted group (container) (typed FeaturePython)
  n = 0.009417
FEATURE [App::DocumentObjectGroupPython] C_element121  label="C_element : 0.281"  # scripted group (container) (typed FeaturePython)
  n = 0.280555
FEATURE [App::DocumentObjectGroupPython] F_element018  label="F_element : 0.710"  # scripted group (container) (typed FeaturePython)
  n = 0.710028
FEATURE [App::DocumentObjectGroupPython] G4_VITON  # scripted group (container) (typed FeaturePython)
  Dunit = g/cm3
  Dvalue = 1.8
  Group = -> [H_element109,C_element121,F_element018]
  conduct = 2
  density = 1
  expand = 3
  formula = G4_VITON
  name = G4_VITON
  specific = 4
FEATURE [App::DocumentObjectGroupPython] H_element110  label="H_element : 059"  # scripted group (container) (typed FeaturePython)
  n = 2
  ref = H_element
FEATURE [App::DocumentObjectGroupPython] O_element103  label="O_element : 057"  # scripted group (container) (typed FeaturePython)
  n = 1
  ref = O_element
FEATURE [App::DocumentObjectGroupPython] G4_WATER  # scripted group (container) (typed FeaturePython)
  Dunit = g/cm3
  Dvalue = 1
  Group = -> [H_element110,O_element103]
  conduct = 2
  density = 1
  expand = 3
  formula = G4_WATER
  name = G4_WATER
  specific = 4
FEATURE [App::DocumentObjectGroupPython] H_element111  label="H_element : 060"  # scripted group (container) (typed FeaturePython)
  n = 2
  ref = H_element
FEATURE [App::DocumentObjectGroupPython] O_element104  label="O_element : 058"  # scripted group (container) (typed FeaturePython)
  n = 1
  ref = O_element
FEATURE [App::DocumentObjectGroupPython] G4_WATER_VAPOR  # scripted group (container) (typed FeaturePython)
  Dunit = g/cm3
  Dvalue = 0.000756182
  Group = -> [H_element111,O_element104]
  conduct = 2
  density = 1
  expand = 3
  formula = G4_WATER_VAPOR
  name = G4_WATER_VAPOR
  specific = 4
FEATURE [App::DocumentObjectGroupPython] C_element122  label="C_element : 068"  # scripted group (container) (typed FeaturePython)
  n = 8
  ref = C_element
FEATURE [App::DocumentObjectGroupPython] H_element112  label="H_element : 061"  # scripted group (container) (typed FeaturePython)
  n = 10
  ref = H_element
FEATURE [App::DocumentObjectGroupPython] G4_XYLENE  # scripted group (container) (typed FeaturePython)
  Dunit = g/cm3
  Dvalue = 0.87
  Group = -> [C_element122,H_element112]
  conduct = 2
  density = 1
  expand = 3
  formula = G4_XYLENE
  name = G4_XYLENE
  specific = 4
FEATURE [App::DocumentObjectGroupPython] C_element123  label="C_element : 069"  # scripted group (container) (typed FeaturePython)
  n = 1
  ref = C_element
FEATURE [App::DocumentObjectGroupPython] G4_GRAPHITE  # scripted group (container) (typed FeaturePython)
  Dunit = g/cm3
  Dvalue = 2.21
  Group = -> [C_element123]
  conduct = 2
  density = 1
  expand = 3
  formula = G4_GRAPHITE
  name = G4_GRAPHITE
  specific = 4
FEATURE [App::DocumentObjectGroupPython] NIST  # scripted group (container) (typed FeaturePython)
  Group = -> [G4_A_150_TISSUE,G4_ACETONE,G4_ACETYLENE,G4_ADENINE,G4_ADIPOSE_TISSUE_ICRP,G4_AIR,G4_ALANINE,G4_ALUMINUM_OXIDE,G4_AMBER,G4_AMMONIA,G4_ANILINE,G4_ANTHRACENE,G4_B_100_BONE,G4_BAKELITE,G4_BARIUM_FLUORIDE,G4_BARIUM_SULFATE,G4_BENZENE,G4_BERYLLIUM_OXIDE,G4_BGO,G4_BLOOD_ICRP,G4_BONE_COMPACT_ICRU,G4_BONE_CORTICAL_ICRP,G4_BORON_CARBIDE,G4_BORON_OXIDE,G4_BRAIN_ICRP,G4_BUTANE,G4_N_BUTYL_ALCOHOL,G4_C_552,+152 more]
FEATURE [App::DocumentObjectGroupPython] H_element113  label="H_element : 062"  # scripted group (container) (typed FeaturePython)
  n = 1
  ref = H_element
FEATURE [App::DocumentObjectGroupPython] G4_H  # scripted group (container) (typed FeaturePython)
  Dunit = g/cm3
  Dvalue = 8.3748e-05
  Group = -> [H_element113]
  conduct = 2
  density = 1
  expand = 3
  formula = H
  name = G4_H
  specific = 4
FEATURE [App::DocumentObjectGroupPython] He_element001  label="He_element : 1"  # scripted group (container) (typed FeaturePython)
  n = 1
  ref = He_element
FEATURE [App::DocumentObjectGroupPython] G4_He  # scripted group (container) (typed FeaturePython)
  Dunit = g/cm3
  Dvalue = 0.000166322
  Group = -> [He_element001]
  conduct = 2
  density = 1
  expand = 3
  formula = He
  name = G4_He
  specific = 4
FEATURE [App::DocumentObjectGroupPython] Li_element008  label="Li_element : 008"  # scripted group (container) (typed FeaturePython)
  n = 1
  ref = Li_element
FEATURE [App::DocumentObjectGroupPython] G4_Li  # scripted group (container) (typed FeaturePython)
  Dunit = g/cm3
  Dvalue = 0.534
  Group = -> [Li_element008]
  conduct = 2
  density = 1
  expand = 3
  formula = Li
  name = G4_Li
  specific = 4
FEATURE [App::DocumentObjectGroupPython] Be_element002  label="Be_element : 002"  # scripted group (container) (typed FeaturePython)
  n = 1
  ref = Be_element
FEATURE [App::DocumentObjectGroupPython] G4_Be  # scripted group (container) (typed FeaturePython)
  Dunit = g/cm3
  Dvalue = 1.848
  Group = -> [Be_element002]
  conduct = 2
  density = 1
  expand = 3
  formula = Be
  name = G4_Be
  specific = 4
FEATURE [App::DocumentObjectGroupPython] B_element007  label="B_element : 007"  # scripted group (container) (typed FeaturePython)
  n = 1
  ref = B_element
FEATURE [App::DocumentObjectGroupPython] G4_B  # scripted group (container) (typed FeaturePython)
  Dunit = g/cm3
  Dvalue = 2.37
  Group = -> [B_element007]
  conduct = 2
  density = 1
  expand = 3
  formula = B
  name = G4_B
  specific = 4
FEATURE [App::DocumentObjectGroupPython] C_element124  label="C_element : 070"  # scripted group (container) (typed FeaturePython)
  n = 1
  ref = C_element
FEATURE [App::DocumentObjectGroupPython] G4_C  # scripted group (container) (typed FeaturePython)
  Dunit = g/cm3
  Dvalue = 2
  Group = -> [C_element124]
  conduct = 2
  density = 1
  expand = 3
  formula = C
  name = G4_C
  specific = 4
FEATURE [App::DocumentObjectGroupPython] N_element048  label="N_element : 021"  # scripted group (container) (typed FeaturePython)
  n = 1
  ref = N_element
FEATURE [App::DocumentObjectGroupPython] G4_N  # scripted group (container) (typed FeaturePython)
  Dunit = g/cm3
  Dvalue = 0.0011652
  Group = -> [N_element048]
  conduct = 2
  density = 1
  expand = 3
  formula = N
  name = G4_N
  specific = 4
FEATURE [App::DocumentObjectGroupPython] O_element105  label="O_element : 059"  # scripted group (container) (typed FeaturePython)
  n = 1
  ref = O_element
FEATURE [App::DocumentObjectGroupPython] G4_O  # scripted group (container) (typed FeaturePython)
  Dunit = g/cm3
  Dvalue = 0.00133151
  Group = -> [O_element105]
  conduct = 2
  density = 1
  expand = 3
  formula = O
  name = G4_O
  specific = 4
FEATURE [App::DocumentObjectGroupPython] F_element019  label="F_element : 008"  # scripted group (container) (typed FeaturePython)
  n = 1
  ref = F_element
FEATURE [App::DocumentObjectGroupPython] G4_F  # scripted group (container) (typed FeaturePython)
  Dunit = g/cm3
  Dvalue = 0.00158029
  Group = -> [F_element019]
  conduct = 2
  density = 1
  expand = 3
  formula = F
  name = G4_F
  specific = 4
FEATURE [App::DocumentObjectGroupPython] Ne_element001  label="Ne_element : 1"  # scripted group (container) (typed FeaturePython)
  n = 1
  ref = Ne_element
FEATURE [App::DocumentObjectGroupPython] G4_Ne  # scripted group (container) (typed FeaturePython)
  Dunit = g/cm3
  Dvalue = 0.000838505
  Group = -> [Ne_element001]
  conduct = 2
  density = 1
  expand = 3
  formula = Ne
  name = G4_Ne
  specific = 4
FEATURE [App::DocumentObjectGroupPython] Na_element020  label="Na_element : 005"  # scripted group (container) (typed FeaturePython)
  n = 1
  ref = Na_element
FEATURE [App::DocumentObjectGroupPython] G4_Na  # scripted group (container) (typed FeaturePython)
  Dunit = g/cm3
  Dvalue = 0.971
  Group = -> [Na_element020]
  conduct = 2
  density = 1
  expand = 3
  formula = Na
  name = G4_Na
  specific = 4
FEATURE [App::DocumentObjectGroupPython] Mg_element011  label="Mg_element : 005"  # scripted group (container) (typed FeaturePython)
  n = 1
  ref = Mg_element
FEATURE [App::DocumentObjectGroupPython] G4_Mg  # scripted group (container) (typed FeaturePython)
  Dunit = g/cm3
  Dvalue = 1.74
  Group = -> [Mg_element011]
  conduct = 2
  density = 1
  expand = 3
  formula = Mg
  name = G4_Mg
  specific = 4
FEATURE [App::DocumentObjectGroupPython] Al_element004  label="Al_element : 1"  # scripted group (container) (typed FeaturePython)
  n = 1
  ref = Al_element
FEATURE [App::DocumentObjectGroupPython] G4_Al  # scripted group (container) (typed FeaturePython)
  Dunit = g/cm3
  Dvalue = 2.699
  Group = -> [Al_element004]
  conduct = 2
  density = 1
  expand = 3
  formula = Al
  name = G4_Al
  specific = 4
FEATURE [App::DocumentObjectGroupPython] Si_element007  label="Si_element : 002"  # scripted group (container) (typed FeaturePython)
  n = 1
  ref = Si_element
FEATURE [App::DocumentObjectGroupPython] G4_Si  # scripted group (container) (typed FeaturePython)
  Dunit = g/cm3
  Dvalue = 2.33
  Group = -> [Si_element007]
  conduct = 2
  density = 1
  expand = 3
  formula = Si
  name = G4_Si
  specific = 4
FEATURE [App::DocumentObjectGroupPython] P_element013  label="P_element : 002"  # scripted group (container) (typed FeaturePython)
  n = 1
  ref = P_element
FEATURE [App::DocumentObjectGroupPython] G4_P  # scripted group (container) (typed FeaturePython)
  Dunit = g/cm3
  Dvalue = 2.2
  Group = -> [P_element013]
  conduct = 2
  density = 1
  expand = 3
  formula = P
  name = G4_P
  specific = 4
FEATURE [App::DocumentObjectGroupPython] S_element023  label="S_element : 007"  # scripted group (container) (typed FeaturePython)
  n = 1
  ref = S_element
FEATURE [App::DocumentObjectGroupPython] G4_S  # scripted group (container) (typed FeaturePython)
  Dunit = g/cm3
  Dvalue = 2
  Group = -> [S_element023]
  conduct = 2
  density = 1
  expand = 3
  formula = S
  name = G4_S
  specific = 4
FEATURE [App::DocumentObjectGroupPython] Cl_element029  label="Cl_element : 015"  # scripted group (container) (typed FeaturePython)
  n = 1
  ref = Cl_element
FEATURE [App::DocumentObjectGroupPython] G4_Cl  # scripted group (container) (typed FeaturePython)
  Dunit = g/cm3
  Dvalue = 0.00299473
  Group = -> [Cl_element029]
  conduct = 2
  density = 1
  expand = 3
  formula = Cl
  name = G4_Cl
  specific = 4
FEATURE [App::DocumentObjectGroupPython] Ar_element002  label="Ar_element : 1"  # scripted group (container) (typed FeaturePython)
  n = 1
  ref = Ar_element
FEATURE [App::DocumentObjectGroupPython] G4_Ar  # scripted group (container) (typed FeaturePython)
  Dunit = g/cm3
  Dvalue = 0.00166201
  Group = -> [Ar_element002]
  conduct = 2
  density = 1
  expand = 3
  formula = Ar
  name = G4_Ar
  specific = 4
FEATURE [App::DocumentObjectGroupPython] K_element013  label="K_element : 003"  # scripted group (container) (typed FeaturePython)
  n = 1
  ref = K_element
FEATURE [App::DocumentObjectGroupPython] G4_K  # scripted group (container) (typed FeaturePython)
  Dunit = g/cm3
  Dvalue = 0.862
  Group = -> [K_element013]
  conduct = 2
  density = 1
  expand = 3
  formula = K
  name = G4_K
  specific = 4
FEATURE [App::DocumentObjectGroupPython] Ca_element014  label="Ca_element : 007"  # scripted group (container) (typed FeaturePython)
  n = 1
  ref = Ca_element
FEATURE [App::DocumentObjectGroupPython] G4_Ca  # scripted group (container) (typed FeaturePython)
  Dunit = g/cm3
  Dvalue = 1.55
  Group = -> [Ca_element014]
  conduct = 2
  density = 1
  expand = 3
  formula = Ca
  name = G4_Ca
  specific = 4
FEATURE [App::DocumentObjectGroupPython] Sc_element001  label="Sc_element : 1"  # scripted group (container) (typed FeaturePython)
  n = 1
  ref = Sc_element
FEATURE [App::DocumentObjectGroupPython] G4_Sc  # scripted group (container) (typed FeaturePython)
  Dunit = g/cm3
  Dvalue = 2.989
  Group = -> [Sc_element001]
  conduct = 2
  density = 1
  expand = 3
  formula = Sc
  name = G4_Sc
  specific = 4
FEATURE [App::DocumentObjectGroupPython] Ti_element004  label="Ti_element : 002"  # scripted group (container) (typed FeaturePython)
  n = 1
  ref = Ti_element
FEATURE [App::DocumentObjectGroupPython] G4_Ti  # scripted group (container) (typed FeaturePython)
  Dunit = g/cm3
  Dvalue = 4.54
  Group = -> [Ti_element004]
  conduct = 2
  density = 1
  expand = 3
  formula = Ti
  name = G4_Ti
  specific = 4
FEATURE [App::DocumentObjectGroupPython] V_element001  label="V_element : 1"  # scripted group (container) (typed FeaturePython)
  n = 1
  ref = V_element
FEATURE [App::DocumentObjectGroupPython] G4_V  # scripted group (container) (typed FeaturePython)
  Dunit = g/cm3
  Dvalue = 6.11
  Group = -> [V_element001]
  conduct = 2
  density = 1
  expand = 3
  formula = V
  name = G4_V
  specific = 4
FEATURE [App::DocumentObjectGroupPython] Cr_element001  label="Cr_element : 1"  # scripted group (container) (typed FeaturePython)
  n = 1
  ref = Cr_element
FEATURE [App::DocumentObjectGroupPython] G4_Cr  # scripted group (container) (typed FeaturePython)
  Dunit = g/cm3
  Dvalue = 7.18
  Group = -> [Cr_element001]
  conduct = 2
  density = 1
  expand = 3
  formula = Cr
  name = G4_Cr
  specific = 4
FEATURE [App::DocumentObjectGroupPython] Mn_element001  label="Mn_element : 1"  # scripted group (container) (typed FeaturePython)
  n = 1
  ref = Mn_element
FEATURE [App::DocumentObjectGroupPython] G4_Mn  # scripted group (container) (typed FeaturePython)
  Dunit = g/cm3
  Dvalue = 7.44
  Group = -> [Mn_element001]
  conduct = 2
  density = 1
  expand = 3
  formula = Mn
  name = G4_Mn
  specific = 4
FEATURE [App::DocumentObjectGroupPython] Fe_element007  label="Fe_element : 004"  # scripted group (container) (typed FeaturePython)
  n = 1
  ref = Fe_element
FEATURE [App::DocumentObjectGroupPython] G4_Fe  # scripted group (container) (typed FeaturePython)
  Dunit = g/cm3
  Dvalue = 7.874
  Group = -> [Fe_element007]
  conduct = 2
  density = 1
  expand = 3
  formula = Fe
  name = G4_Fe
  specific = 4
FEATURE [App::DocumentObjectGroupPython] Co_element001  label="Co_element : 1"  # scripted group (container) (typed FeaturePython)
  n = 1
  ref = Co_element
FEATURE [App::DocumentObjectGroupPython] G4_Co  # scripted group (container) (typed FeaturePython)
  Dunit = g/cm3
  Dvalue = 8.9
  Group = -> [Co_element001]
  conduct = 2
  density = 1
  expand = 3
  formula = Co
  name = G4_Co
  specific = 4
FEATURE [App::DocumentObjectGroupPython] Ni_element001  label="Ni_element : 1"  # scripted group (container) (typed FeaturePython)
  n = 1
  ref = Ni_element
FEATURE [App::DocumentObjectGroupPython] G4_Ni  # scripted group (container) (typed FeaturePython)
  Dunit = g/cm3
  Dvalue = 8.902
  Group = -> [Ni_element001]
  conduct = 2
  density = 1
  expand = 3
  formula = Ni
  name = G4_Ni
  specific = 4
FEATURE [App::DocumentObjectGroupPython] Cu_element001  label="Cu_element : 1"  # scripted group (container) (typed FeaturePython)
  n = 1
  ref = Cu_element
FEATURE [App::DocumentObjectGroupPython] G4_Cu  # scripted group (container) (typed FeaturePython)
  Dunit = g/cm3
  Dvalue = 8.96
  Group = -> [Cu_element001]
  conduct = 2
  density = 1
  expand = 3
  formula = Cu
  name = G4_Cu
  specific = 4
FEATURE [App::DocumentObjectGroupPython] Zn_element001  label="Zn_element : 1"  # scripted group (container) (typed FeaturePython)
  n = 1
  ref = Zn_element
FEATURE [App::DocumentObjectGroupPython] G4_Zn  # scripted group (container) (typed FeaturePython)
  Dunit = g/cm3
  Dvalue = 7.133
  Group = -> [Zn_element001]
  conduct = 2
  density = 1
  expand = 3
  formula = Zn
  name = G4_Zn
  specific = 4
FEATURE [App::DocumentObjectGroupPython] Ga_element002  label="Ga_element : 002"  # scripted group (container) (typed FeaturePython)
  n = 1
  ref = Ga_element
FEATURE [App::DocumentObjectGroupPython] G4_Ga  # scripted group (container) (typed FeaturePython)
  Dunit = g/cm3
  Dvalue = 5.904
  Group = -> [Ga_element002]
  conduct = 2
  density = 1
  expand = 3
  formula = Ga
  name = G4_Ga
  specific = 4
FEATURE [App::DocumentObjectGroupPython] Ge_element002  label="Ge_element : 1"  # scripted group (container) (typed FeaturePython)
  n = 1
  ref = Ge_element
FEATURE [App::DocumentObjectGroupPython] G4_Ge  # scripted group (container) (typed FeaturePython)
  Dunit = g/cm3
  Dvalue = 5.323
  Group = -> [Ge_element002]
  conduct = 2
  density = 1
  expand = 3
  formula = Ge
  name = G4_Ge
  specific = 4
FEATURE [App::DocumentObjectGroupPython] As_element003  label="As_element : 002"  # scripted group (container) (typed FeaturePython)
  n = 1
  ref = As_element
FEATURE [App::DocumentObjectGroupPython] G4_As  # scripted group (container) (typed FeaturePython)
  Dunit = g/cm3
  Dvalue = 5.73
  Group = -> [As_element003]
  conduct = 2
  density = 1
  expand = 3
  formula = As
  name = G4_As
  specific = 4
FEATURE [App::DocumentObjectGroupPython] Se_element001  label="Se_element : 1"  # scripted group (container) (typed FeaturePython)
  n = 1
  ref = Se_element
FEATURE [App::DocumentObjectGroupPython] G4_Se  # scripted group (container) (typed FeaturePython)
  Dunit = g/cm3
  Dvalue = 4.5
  Group = -> [Se_element001]
  conduct = 2
  density = 1
  expand = 3
  formula = Se
  name = G4_Se
  specific = 4
FEATURE [App::DocumentObjectGroupPython] Br_element007  label="Br_element : 004"  # scripted group (container) (typed FeaturePython)
  n = 1
  ref = Br_element
FEATURE [App::DocumentObjectGroupPython] G4_Br  # scripted group (container) (typed FeaturePython)
  Dunit = g/cm3
  Dvalue = 0.0070721
  Group = -> [Br_element007]
  conduct = 2
  density = 1
  expand = 3
  formula = Br
  name = G4_Br
  specific = 4
FEATURE [App::DocumentObjectGroupPython] Kr_element001  label="Kr_element : 1"  # scripted group (container) (typed FeaturePython)
  n = 1
  ref = Kr_element
FEATURE [App::DocumentObjectGroupPython] G4_Kr  # scripted group (container) (typed FeaturePython)
  Dunit = g/cm3
  Dvalue = 0.00347832
  Group = -> [Kr_element001]
  conduct = 2
  density = 1
  expand = 3
  formula = Kr
  name = G4_Kr
  specific = 4
FEATURE [App::DocumentObjectGroupPython] Rb_element001  label="Rb_element : 1"  # scripted group (container) (typed FeaturePython)
  n = 1
  ref = Rb_element
FEATURE [App::DocumentObjectGroupPython] G4_Rb  # scripted group (container) (typed FeaturePython)
  Dunit = g/cm3
  Dvalue = 1.532
  Group = -> [Rb_element001]
  conduct = 2
  density = 1
  expand = 3
  formula = Rb
  name = G4_Rb
  specific = 4
FEATURE [App::DocumentObjectGroupPython] Sr_element001  label="Sr_element : 1"  # scripted group (container) (typed FeaturePython)
  n = 1
  ref = Sr_element
FEATURE [App::DocumentObjectGroupPython] G4_Sr  # scripted group (container) (typed FeaturePython)
  Dunit = g/cm3
  Dvalue = 2.54
  Group = -> [Sr_element001]
  conduct = 2
  density = 1
  expand = 3
  formula = Sr
  name = G4_Sr
  specific = 4
FEATURE [App::DocumentObjectGroupPython] Y_element001  label="Y_element : 1"  # scripted group (container) (typed FeaturePython)
  n = 1
  ref = Y_element
FEATURE [App::DocumentObjectGroupPython] G4_Y  # scripted group (container) (typed FeaturePython)
  Dunit = g/cm3
  Dvalue = 4.469
  Group = -> [Y_element001]
  conduct = 2
  density = 1
  expand = 3
  formula = Y
  name = G4_Y
  specific = 4
FEATURE [App::DocumentObjectGroupPython] Zr_element001  label="Zr_element : 1"  # scripted group (container) (typed FeaturePython)
  n = 1
  ref = Zr_element
FEATURE [App::DocumentObjectGroupPython] G4_Zr  # scripted group (container) (typed FeaturePython)
  Dunit = g/cm3
  Dvalue = 6.506
  Group = -> [Zr_element001]
  conduct = 2
  density = 1
  expand = 3
  formula = Zr
  name = G4_Zr
  specific = 4
FEATURE [App::DocumentObjectGroupPython] Nb_element001  label="Nb_element : 1"  # scripted group (container) (typed FeaturePython)
  n = 1
  ref = Nb_element
FEATURE [App::DocumentObjectGroupPython] G4_Nb  # scripted group (container) (typed FeaturePython)
  Dunit = g/cm3
  Dvalue = 8.57
  Group = -> [Nb_element001]
  conduct = 2
  density = 1
  expand = 3
  formula = Nb
  name = G4_Nb
  specific = 4
FEATURE [App::DocumentObjectGroupPython] Mo_element001  label="Mo_element : 1"  # scripted group (container) (typed FeaturePython)
  n = 1
  ref = Mo_element
FEATURE [App::DocumentObjectGroupPython] G4_Mo  # scripted group (container) (typed FeaturePython)
  Dunit = g/cm3
  Dvalue = 10.22
  Group = -> [Mo_element001]
  conduct = 2
  density = 1
  expand = 3
  formula = Mo
  name = G4_Mo
  specific = 4
FEATURE [App::DocumentObjectGroupPython] Tc_element001  label="Tc_element : 1"  # scripted group (container) (typed FeaturePython)
  n = 1
  ref = Tc_element
FEATURE [App::DocumentObjectGroupPython] G4_Tc  # scripted group (container) (typed FeaturePython)
  Dunit = g/cm3
  Dvalue = 11.5
  Group = -> [Tc_element001]
  conduct = 2
  density = 1
  expand = 3
  formula = Tc
  name = G4_Tc
  specific = 4
FEATURE [App::DocumentObjectGroupPython] Ru_element001  label="Ru_element : 1"  # scripted group (container) (typed FeaturePython)
  n = 1
  ref = Ru_element
FEATURE [App::DocumentObjectGroupPython] G4_Ru  # scripted group (container) (typed FeaturePython)
  Dunit = g/cm3
  Dvalue = 12.41
  Group = -> [Ru_element001]
  conduct = 2
  density = 1
  expand = 3
  formula = Ru
  name = G4_Ru
  specific = 4
FEATURE [App::DocumentObjectGroupPython] Rh_element001  label="Rh_element : 1"  # scripted group (container) (typed FeaturePython)
  n = 1
  ref = Rh_element
FEATURE [App::DocumentObjectGroupPython] G4_Rh  # scripted group (container) (typed FeaturePython)
  Dunit = g/cm3
  Dvalue = 12.41
  Group = -> [Rh_element001]
  conduct = 2
  density = 1
  expand = 3
  formula = Rh
  name = G4_Rh
  specific = 4
FEATURE [App::DocumentObjectGroupPython] Pd_element001  label="Pd_element : 1"  # scripted group (container) (typed FeaturePython)
  n = 1
  ref = Pd_element
FEATURE [App::DocumentObjectGroupPython] G4_Pd  # scripted group (container) (typed FeaturePython)
  Dunit = g/cm3
  Dvalue = 12.02
  Group = -> [Pd_element001]
  conduct = 2
  density = 1
  expand = 3
  formula = Pd
  name = G4_Pd
  specific = 4
FEATURE [App::DocumentObjectGroupPython] Ag_element006  label="Ag_element : 004"  # scripted group (container) (typed FeaturePython)
  n = 1
  ref = Ag_element
FEATURE [App::DocumentObjectGroupPython] G4_Ag  # scripted group (container) (typed FeaturePython)
  Dunit = g/cm3
  Dvalue = 10.5
  Group = -> [Ag_element006]
  conduct = 2
  density = 1
  expand = 3
  formula = Ag
  name = G4_Ag
  specific = 4
FEATURE [App::DocumentObjectGroupPython] Cd_element003  label="Cd_element : 003"  # scripted group (container) (typed FeaturePython)
  n = 1
  ref = Cd_element
FEATURE [App::DocumentObjectGroupPython] G4_Cd  # scripted group (container) (typed FeaturePython)
  Dunit = g/cm3
  Dvalue = 8.65
  Group = -> [Cd_element003]
  conduct = 2
  density = 1
  expand = 3
  formula = Cd
  name = G4_Cd
  specific = 4
FEATURE [App::DocumentObjectGroupPython] In_element001  label="In_element : 1"  # scripted group (container) (typed FeaturePython)
  n = 1
  ref = In_element
FEATURE [App::DocumentObjectGroupPython] G4_In  # scripted group (container) (typed FeaturePython)
  Dunit = g/cm3
  Dvalue = 7.31
  Group = -> [In_element001]
  conduct = 2
  density = 1
  expand = 3
  formula = In
  name = G4_In
  specific = 4
FEATURE [App::DocumentObjectGroupPython] Sn_element001  label="Sn_element : 1"  # scripted group (container) (typed FeaturePython)
  n = 1
  ref = Sn_element
FEATURE [App::DocumentObjectGroupPython] G4_Sn  # scripted group (container) (typed FeaturePython)
  Dunit = g/cm3
  Dvalue = 7.31
  Group = -> [Sn_element001]
  conduct = 2
  density = 1
  expand = 3
  formula = Sn
  name = G4_Sn
  specific = 4
FEATURE [App::DocumentObjectGroupPython] Sb_element001  label="Sb_element : 1"  # scripted group (container) (typed FeaturePython)
  n = 1
  ref = Sb_element
FEATURE [App::DocumentObjectGroupPython] G4_Sb  # scripted group (container) (typed FeaturePython)
  Dunit = g/cm3
  Dvalue = 6.691
  Group = -> [Sb_element001]
  conduct = 2
  density = 1
  expand = 3
  formula = Sb
  name = G4_Sb
  specific = 4
FEATURE [App::DocumentObjectGroupPython] Te_element002  label="Te_element : 002"  # scripted group (container) (typed FeaturePython)
  n = 1
  ref = Te_element
FEATURE [App::DocumentObjectGroupPython] G4_Te  # scripted group (container) (typed FeaturePython)
  Dunit = g/cm3
  Dvalue = 6.24
  Group = -> [Te_element002]
  conduct = 2
  density = 1
  expand = 3
  formula = Te
  name = G4_Te
  specific = 4
FEATURE [App::DocumentObjectGroupPython] I_element010  label="I_element : 006"  # scripted group (container) (typed FeaturePython)
  n = 1
  ref = I_element
FEATURE [App::DocumentObjectGroupPython] G4_I  # scripted group (container) (typed FeaturePython)
  Dunit = g/cm3
  Dvalue = 4.93
  Group = -> [I_element010]
  conduct = 2
  density = 1
  expand = 3
  formula = I
  name = G4_I
  specific = 4
FEATURE [App::DocumentObjectGroupPython] Xe_element001  label="Xe_element : 1"  # scripted group (container) (typed FeaturePython)
  n = 1
  ref = Xe_element
FEATURE [App::DocumentObjectGroupPython] G4_Xe  # scripted group (container) (typed FeaturePython)
  Dunit = g/cm3
  Dvalue = 0.00548536
  Group = -> [Xe_element001]
  conduct = 2
  density = 1
  expand = 3
  formula = Xe
  name = G4_Xe
  specific = 4
FEATURE [App::DocumentObjectGroupPython] Cs_element003  label="Cs_element : 003"  # scripted group (container) (typed FeaturePython)
  n = 1
  ref = Cs_element
FEATURE [App::DocumentObjectGroupPython] G4_Cs  # scripted group (container) (typed FeaturePython)
  Dunit = g/cm3
  Dvalue = 1.873
  Group = -> [Cs_element003]
  conduct = 2
  density = 1
  expand = 3
  formula = Cs
  name = G4_Cs
  specific = 4
FEATURE [App::DocumentObjectGroupPython] Ba_element003  label="Ba_element : 003"  # scripted group (container) (typed FeaturePython)
  n = 1
  ref = Ba_element
FEATURE [App::DocumentObjectGroupPython] G4_Ba  # scripted group (container) (typed FeaturePython)
  Dunit = g/cm3
  Dvalue = 3.5
  Group = -> [Ba_element003]
  conduct = 2
  density = 1
  expand = 3
  formula = Ba
  name = G4_Ba
  specific = 4
FEATURE [App::DocumentObjectGroupPython] La_element003  label="La_element : 003"  # scripted group (container) (typed FeaturePython)
  n = 1
  ref = La_element
FEATURE [App::DocumentObjectGroupPython] G4_La  # scripted group (container) (typed FeaturePython)
  Dunit = g/cm3
  Dvalue = 6.154
  Group = -> [La_element003]
  conduct = 2
  density = 1
  expand = 3
  formula = La
  name = G4_La
  specific = 4
FEATURE [App::DocumentObjectGroupPython] Ce_element002  label="Ce_element : 1"  # scripted group (container) (typed FeaturePython)
  n = 1
  ref = Ce_element
FEATURE [App::DocumentObjectGroupPython] G4_Ce  # scripted group (container) (typed FeaturePython)
  Dunit = g/cm3
  Dvalue = 6.657
  Group = -> [Ce_element002]
  conduct = 2
  density = 1
  expand = 3
  formula = Ce
  name = G4_Ce
  specific = 4
FEATURE [App::DocumentObjectGroupPython] Pr_element001  label="Pr_element : 1"  # scripted group (container) (typed FeaturePython)
  n = 1
  ref = Pr_element
FEATURE [App::DocumentObjectGroupPython] G4_Pr  # scripted group (container) (typed FeaturePython)
  Dunit = g/cm3
  Dvalue = 6.71
  Group = -> [Pr_element001]
  conduct = 2
  density = 1
  expand = 3
  formula = Pr
  name = G4_Pr
  specific = 4
FEATURE [App::DocumentObjectGroupPython] Nd_element001  label="Nd_element : 1"  # scripted group (container) (typed FeaturePython)
  n = 1
  ref = Nd_element
FEATURE [App::DocumentObjectGroupPython] G4_Nd  # scripted group (container) (typed FeaturePython)
  Dunit = g/cm3
  Dvalue = 6.9
  Group = -> [Nd_element001]
  conduct = 2
  density = 1
  expand = 3
  formula = Nd
  name = G4_Nd
  specific = 4
FEATURE [App::DocumentObjectGroupPython] Pm_element001  label="Pm_element : 1"  # scripted group (container) (typed FeaturePython)
  n = 1
  ref = Pm_element
FEATURE [App::DocumentObjectGroupPython] G4_Pm  # scripted group (container) (typed FeaturePython)
  Dunit = g/cm3
  Dvalue = 7.22
  Group = -> [Pm_element001]
  conduct = 2
  density = 1
  expand = 3
  formula = Pm
  name = G4_Pm
  specific = 4
FEATURE [App::DocumentObjectGroupPython] Sm_element001  label="Sm_element : 1"  # scripted group (container) (typed FeaturePython)
  n = 1
  ref = Sm_element
FEATURE [App::DocumentObjectGroupPython] G4_Sm  # scripted group (container) (typed FeaturePython)
  Dunit = g/cm3
  Dvalue = 7.46
  Group = -> [Sm_element001]
  conduct = 2
  density = 1
  expand = 3
  formula = Sm
  name = G4_Sm
  specific = 4
FEATURE [App::DocumentObjectGroupPython] Eu_element001  label="Eu_element : 1"  # scripted group (container) (typed FeaturePython)
  n = 1
  ref = Eu_element
FEATURE [App::DocumentObjectGroupPython] G4_Eu  # scripted group (container) (typed FeaturePython)
  Dunit = g/cm3
  Dvalue = 5.243
  Group = -> [Eu_element001]
  conduct = 2
  density = 1
  expand = 3
  formula = Eu
  name = G4_Eu
  specific = 4
FEATURE [App::DocumentObjectGroupPython] Gd_element002  label="Gd_element : 1"  # scripted group (container) (typed FeaturePython)
  n = 1
  ref = Gd_element
FEATURE [App::DocumentObjectGroupPython] G4_Gd  # scripted group (container) (typed FeaturePython)
  Dunit = g/cm3
  Dvalue = 7.9004
  Group = -> [Gd_element002]
  conduct = 2
  density = 1
  expand = 3
  formula = Gd
  name = G4_Gd
  specific = 4
FEATURE [App::DocumentObjectGroupPython] Tb_element001  label="Tb_element : 1"  # scripted group (container) (typed FeaturePython)
  n = 1
  ref = Tb_element
FEATURE [App::DocumentObjectGroupPython] G4_Tb  # scripted group (container) (typed FeaturePython)
  Dunit = g/cm3
  Dvalue = 8.229
  Group = -> [Tb_element001]
  conduct = 2
  density = 1
  expand = 3
  formula = Tb
  name = G4_Tb
  specific = 4
FEATURE [App::DocumentObjectGroupPython] Dy_element001  label="Dy_element : 1"  # scripted group (container) (typed FeaturePython)
  n = 1
  ref = Dy_element
FEATURE [App::DocumentObjectGroupPython] G4_Dy  # scripted group (container) (typed FeaturePython)
  Dunit = g/cm3
  Dvalue = 8.55
  Group = -> [Dy_element001]
  conduct = 2
  density = 1
  expand = 3
  formula = Dy
  name = G4_Dy
  specific = 4
FEATURE [App::DocumentObjectGroupPython] Ho_element001  label="Ho_element : 1"  # scripted group (container) (typed FeaturePython)
  n = 1
  ref = Ho_element
FEATURE [App::DocumentObjectGroupPython] G4_Ho  # scripted group (container) (typed FeaturePython)
  Dunit = g/cm3
  Dvalue = 8.795
  Group = -> [Ho_element001]
  conduct = 2
  density = 1
  expand = 3
  formula = Ho
  name = G4_Ho
  specific = 4
FEATURE [App::DocumentObjectGroupPython] Er_element001  label="Er_element : 1"  # scripted group (container) (typed FeaturePython)
  n = 1
  ref = Er_element
FEATURE [App::DocumentObjectGroupPython] G4_Er  # scripted group (container) (typed FeaturePython)
  Dunit = g/cm3
  Dvalue = 9.066
  Group = -> [Er_element001]
  conduct = 2
  density = 1
  expand = 3
  formula = Er
  name = G4_Er
  specific = 4
FEATURE [App::DocumentObjectGroupPython] Tm_element001  label="Tm_element : 1"  # scripted group (container) (typed FeaturePython)
  n = 1
  ref = Tm_element
FEATURE [App::DocumentObjectGroupPython] G4_Tm  # scripted group (container) (typed FeaturePython)
  Dunit = g/cm3
  Dvalue = 9.321
  Group = -> [Tm_element001]
  conduct = 2
  density = 1
  expand = 3
  formula = Tm
  name = G4_Tm
  specific = 4
FEATURE [App::DocumentObjectGroupPython] Yb_element001  label="Yb_element : 1"  # scripted group (container) (typed FeaturePython)
  n = 1
  ref = Yb_element
FEATURE [App::DocumentObjectGroupPython] G4_Yb  # scripted group (container) (typed FeaturePython)
  Dunit = g/cm3
  Dvalue = 6.73
  Group = -> [Yb_element001]
  conduct = 2
  density = 1
  expand = 3
  formula = Yb
  name = G4_Yb
  specific = 4
FEATURE [App::DocumentObjectGroupPython] Lu_element001  label="Lu_element : 1"  # scripted group (container) (typed FeaturePython)
  n = 1
  ref = Lu_element
FEATURE [App::DocumentObjectGroupPython] G4_Lu  # scripted group (container) (typed FeaturePython)
  Dunit = g/cm3
  Dvalue = 9.84
  Group = -> [Lu_element001]
  conduct = 2
  density = 1
  expand = 3
  formula = Lu
  name = G4_Lu
  specific = 4
FEATURE [App::DocumentObjectGroupPython] Hf_element001  label="Hf_element : 1"  # scripted group (container) (typed FeaturePython)
  n = 1
  ref = Hf_element
FEATURE [App::DocumentObjectGroupPython] G4_Hf  # scripted group (container) (typed FeaturePython)
  Dunit = g/cm3
  Dvalue = 13.31
  Group = -> [Hf_element001]
  conduct = 2
  density = 1
  expand = 3
  formula = Hf
  name = G4_Hf
  specific = 4
FEATURE [App::DocumentObjectGroupPython] Ta_element001  label="Ta_element : 1"  # scripted group (container) (typed FeaturePython)
  n = 1
  ref = Ta_element
FEATURE [App::DocumentObjectGroupPython] G4_Ta  # scripted group (container) (typed FeaturePython)
  Dunit = g/cm3
  Dvalue = 16.654
  Group = -> [Ta_element001]
  conduct = 2
  density = 1
  expand = 3
  formula = Ta
  name = G4_Ta
  specific = 4
FEATURE [App::DocumentObjectGroupPython] W_element004  label="W_element : 004"  # scripted group (container) (typed FeaturePython)
  n = 1
  ref = W_element
FEATURE [App::DocumentObjectGroupPython] G4_W  # scripted group (container) (typed FeaturePython)
  Dunit = g/cm3
  Dvalue = 19.3
  Group = -> [W_element004]
  conduct = 2
  density = 1
  expand = 3
  formula = W
  name = G4_W
  specific = 4
FEATURE [App::DocumentObjectGroupPython] Re_element001  label="Re_element : 1"  # scripted group (container) (typed FeaturePython)
  n = 1
  ref = Re_element
FEATURE [App::DocumentObjectGroupPython] G4_Re  # scripted group (container) (typed FeaturePython)
  Dunit = g/cm3
  Dvalue = 21.02
  Group = -> [Re_element001]
  conduct = 2
  density = 1
  expand = 3
  formula = Re
  name = G4_Re
  specific = 4
FEATURE [App::DocumentObjectGroupPython] Os_element001  label="Os_element : 1"  # scripted group (container) (typed FeaturePython)
  n = 1
  ref = Os_element
FEATURE [App::DocumentObjectGroupPython] G4_Os  # scripted group (container) (typed FeaturePython)
  Dunit = g/cm3
  Dvalue = 22.57
  Group = -> [Os_element001]
  conduct = 2
  density = 1
  expand = 3
  formula = Os
  name = G4_Os
  specific = 4
FEATURE [App::DocumentObjectGroupPython] Ir_element001  label="Ir_element : 1"  # scripted group (container) (typed FeaturePython)
  n = 1
  ref = Ir_element
FEATURE [App::DocumentObjectGroupPython] G4_Ir  # scripted group (container) (typed FeaturePython)
  Dunit = g/cm3
  Dvalue = 22.42
  Group = -> [Ir_element001]
  conduct = 2
  density = 1
  expand = 3
  formula = Ir
  name = G4_Ir
  specific = 4
FEATURE [App::DocumentObjectGroupPython] Pt_element001  label="Pt_element : 1"  # scripted group (container) (typed FeaturePython)
  n = 1
  ref = Pt_element
FEATURE [App::DocumentObjectGroupPython] G4_Pt  # scripted group (container) (typed FeaturePython)
  Dunit = g/cm3
  Dvalue = 21.45
  Group = -> [Pt_element001]
  conduct = 2
  density = 1
  expand = 3
  formula = Pt
  name = G4_Pt
  specific = 4
FEATURE [App::DocumentObjectGroupPython] Au_element001  label="Au_element : 1"  # scripted group (container) (typed FeaturePython)
  n = 1
  ref = Au_element
FEATURE [App::DocumentObjectGroupPython] G4_Au  # scripted group (container) (typed FeaturePython)
  Dunit = g/cm3
  Dvalue = 19.32
  Group = -> [Au_element001]
  conduct = 2
  density = 1
  expand = 3
  formula = Au
  name = G4_Au
  specific = 4
FEATURE [App::DocumentObjectGroupPython] Hg_element002  label="Hg_element : 002"  # scripted group (container) (typed FeaturePython)
  n = 1
  ref = Hg_element
FEATURE [App::DocumentObjectGroupPython] G4_Hg  # scripted group (container) (typed FeaturePython)
  Dunit = g/cm3
  Dvalue = 13.546
  Group = -> [Hg_element002]
  conduct = 2
  density = 1
  expand = 3
  formula = Hg
  name = G4_Hg
  specific = 4
FEATURE [App::DocumentObjectGroupPython] Tl_element002  label="Tl_element : 002"  # scripted group (container) (typed FeaturePython)
  n = 1
  ref = Tl_element
FEATURE [App::DocumentObjectGroupPython] G4_Tl  # scripted group (container) (typed FeaturePython)
  Dunit = g/cm3
  Dvalue = 11.72
  Group = -> [Tl_element002]
  conduct = 2
  density = 1
  expand = 3
  formula = Tl
  name = G4_Tl
  specific = 4
FEATURE [App::DocumentObjectGroupPython] Pb_element003  label="Pb_element : 1"  # scripted group (container) (typed FeaturePython)
  n = 1
  ref = Pb_element
FEATURE [App::DocumentObjectGroupPython] G4_Pb  # scripted group (container) (typed FeaturePython)
  Dunit = g/cm3
  Dvalue = 11.35
  Group = -> [Pb_element003]
  conduct = 2
  density = 1
  expand = 3
  formula = Pb
  name = G4_Pb
  specific = 4
FEATURE [App::DocumentObjectGroupPython] Bi_element002  label="Bi_element : 1"  # scripted group (container) (typed FeaturePython)
  n = 1
  ref = Bi_element
FEATURE [App::DocumentObjectGroupPython] G4_Bi  # scripted group (container) (typed FeaturePython)
  Dunit = g/cm3
  Dvalue = 9.747
  Group = -> [Bi_element002]
  conduct = 2
  density = 1
  expand = 3
  formula = Bi
  name = G4_Bi
  specific = 4
FEATURE [App::DocumentObjectGroupPython] Po_element001  label="Po_element : 1"  # scripted group (container) (typed FeaturePython)
  n = 1
  ref = Po_element
FEATURE [App::DocumentObjectGroupPython] G4_Po  # scripted group (container) (typed FeaturePython)
  Dunit = g/cm3
  Dvalue = 9.32
  Group = -> [Po_element001]
  conduct = 2
  density = 1
  expand = 3
  formula = Po
  name = G4_Po
  specific = 4
FEATURE [App::DocumentObjectGroupPython] At_element001  label="At_element : 1"  # scripted group (container) (typed FeaturePython)
  n = 1
  ref = At_element
FEATURE [App::DocumentObjectGroupPython] G4_At  # scripted group (container) (typed FeaturePython)
  Dunit = g/cm3
  Dvalue = 9.32
  Group = -> [At_element001]
  conduct = 2
  density = 1
  expand = 3
  formula = At
  name = G4_At
  specific = 4
FEATURE [App::DocumentObjectGroupPython] Rn_element001  label="Rn_element : 1"  # scripted group (container) (typed FeaturePython)
  n = 1
  ref = Rn_element
FEATURE [App::DocumentObjectGroupPython] G4_Rn  # scripted group (container) (typed FeaturePython)
  Dunit = g/cm3
  Dvalue = 0.00900662
  Group = -> [Rn_element001]
  conduct = 2
  density = 1
  expand = 3
  formula = Rn
  name = G4_Rn
  specific = 4
FEATURE [App::DocumentObjectGroupPython] Fr_element001  label="Fr_element : 1"  # scripted group (container) (typed FeaturePython)
  n = 1
  ref = Fr_element
FEATURE [App::DocumentObjectGroupPython] G4_Fr  # scripted group (container) (typed FeaturePython)
  Dunit = g/cm3
  Dvalue = 1
  Group = -> [Fr_element001]
  conduct = 2
  density = 1
  expand = 3
  formula = Fr
  name = G4_Fr
  specific = 4
FEATURE [App::DocumentObjectGroupPython] Ra_element001  label="Ra_element : 1"  # scripted group (container) (typed FeaturePython)
  n = 1
  ref = Ra_element
FEATURE [App::DocumentObjectGroupPython] G4_Ra  # scripted group (container) (typed FeaturePython)
  Dunit = g/cm3
  Dvalue = 5
  Group = -> [Ra_element001]
  conduct = 2
  density = 1
  expand = 3
  formula = Ra
  name = G4_Ra
  specific = 4
FEATURE [App::DocumentObjectGroupPython] Ac_element001  label="Ac_element : 1"  # scripted group (container) (typed FeaturePython)
  n = 1
  ref = Ac_element
FEATURE [App::DocumentObjectGroupPython] G4_Ac  # scripted group (container) (typed FeaturePython)
  Dunit = g/cm3
  Dvalue = 10.07
  Group = -> [Ac_element001]
  conduct = 2
  density = 1
  expand = 3
  formula = Ac
  name = G4_Ac
  specific = 4
FEATURE [App::DocumentObjectGroupPython] Th_element001  label="Th_element : 1"  # scripted group (container) (typed FeaturePython)
  n = 1
  ref = Th_element
FEATURE [App::DocumentObjectGroupPython] G4_Th  # scripted group (container) (typed FeaturePython)
  Dunit = g/cm3
  Dvalue = 11.72
  Group = -> [Th_element001]
  conduct = 2
  density = 1
  expand = 3
  formula = Th
  name = G4_Th
  specific = 4
FEATURE [App::DocumentObjectGroupPython] Pa_element001  label="Pa_element : 1"  # scripted group (container) (typed FeaturePython)
  n = 1
  ref = Pa_element
FEATURE [App::DocumentObjectGroupPython] G4_Pa  # scripted group (container) (typed FeaturePython)
  Dunit = g/cm3
  Dvalue = 15.37
  Group = -> [Pa_element001]
  conduct = 2
  density = 1
  expand = 3
  formula = Pa
  name = G4_Pa
  specific = 4
FEATURE [App::DocumentObjectGroupPython] U_element004  label="U_element : 004"  # scripted group (container) (typed FeaturePython)
  n = 1
  ref = U_element
FEATURE [App::DocumentObjectGroupPython] G4_U  # scripted group (container) (typed FeaturePython)
  Dunit = g/cm3
  Dvalue = 18.95
  Group = -> [U_element004]
  conduct = 2
  density = 1
  expand = 3
  formula = U
  name = G4_U
  specific = 4
FEATURE [App::DocumentObjectGroupPython] Np_element001  label="Np_element : 1"  # scripted group (container) (typed FeaturePython)
  n = 1
  ref = Np_element
FEATURE [App::DocumentObjectGroupPython] G4_Np  # scripted group (container) (typed FeaturePython)
  Dunit = g/cm3
  Dvalue = 20.25
  Group = -> [Np_element001]
  conduct = 2
  density = 1
  expand = 3
  formula = Np
  name = G4_Np
  specific = 4
FEATURE [App::DocumentObjectGroupPython] Pu_element002  label="Pu_element : 002"  # scripted group (container) (typed FeaturePython)
  n = 1
  ref = Pu_element
FEATURE [App::DocumentObjectGroupPython] G4_Pu  # scripted group (container) (typed FeaturePython)
  Dunit = g/cm3
  Dvalue = 19.84
  Group = -> [Pu_element002]
  conduct = 2
  density = 1
  expand = 3
  formula = Pu
  name = G4_Pu
  specific = 4
FEATURE [App::DocumentObjectGroupPython] Am_element001  label="Am_element : 1"  # scripted group (container) (typed FeaturePython)
  n = 1
  ref = Am_element
FEATURE [App::DocumentObjectGroupPython] G4_Am  # scripted group (container) (typed FeaturePython)
  Dunit = g/cm3
  Dvalue = 13.67
  Group = -> [Am_element001]
  conduct = 2
  density = 1
  expand = 3
  formula = Am
  name = G4_Am
  specific = 4
FEATURE [App::DocumentObjectGroupPython] Cm_element001  label="Cm_element : 1"  # scripted group (container) (typed FeaturePython)
  n = 1
  ref = Cm_element
FEATURE [App::DocumentObjectGroupPython] G4_Cm  # scripted group (container) (typed FeaturePython)
  Dunit = g/cm3
  Dvalue = 13.51
  Group = -> [Cm_element001]
  conduct = 2
  density = 1
  expand = 3
  formula = Cm
  name = G4_Cm
  specific = 4
FEATURE [App::DocumentObjectGroupPython] Bk_element001  label="Bk_element : 1"  # scripted group (container) (typed FeaturePython)
  n = 1
  ref = Bk_element
FEATURE [App::DocumentObjectGroupPython] G4_Bk  # scripted group (container) (typed FeaturePython)
  Dunit = g/cm3
  Dvalue = 14
  Group = -> [Bk_element001]
  conduct = 2
  density = 1
  expand = 3
  formula = Bk
  name = G4_Bk
  specific = 4
FEATURE [App::DocumentObjectGroupPython] Cf_element001  label="Cf_element : 1"  # scripted group (container) (typed FeaturePython)
  n = 1
  ref = Cf_element
FEATURE [App::DocumentObjectGroupPython] G4_Cf  # scripted group (container) (typed FeaturePython)
  Dunit = g/cm3
  Dvalue = 10
  Group = -> [Cf_element001]
  conduct = 2
  density = 1
  expand = 3
  formula = Cf
  name = G4_Cf
  specific = 4
FEATURE [App::DocumentObjectGroupPython] Element  # scripted group (container) (typed FeaturePython)
  Group = -> [G4_H,G4_He,G4_Li,G4_Be,G4_B,G4_C,G4_N,G4_O,G4_F,G4_Ne,G4_Na,G4_Mg,G4_Al,G4_Si,G4_P,G4_S,G4_Cl,G4_Ar,G4_K,G4_Ca,G4_Sc,G4_Ti,G4_V,G4_Cr,G4_Mn,G4_Fe,G4_Co,G4_Ni,G4_Cu,G4_Zn,G4_Ga,G4_Ge,G4_As,G4_Se,G4_Br,G4_Kr,G4_Rb,G4_Sr,G4_Y,G4_Zr,G4_Nb,G4_Mo,G4_Tc,G4_Ru,G4_Rh,G4_Pd,G4_Ag,G4_Cd,G4_In,G4_Sn,G4_Sb,G4_Te,G4_I,G4_Xe,G4_Cs,G4_Ba,G4_La,G4_Ce,G4_Pr,G4_Nd,G4_Pm,G4_Sm,G4_Eu,G4_Gd,G4_Tb,G4_Dy,G4_Ho,G4_Er,+30 more]
FEATURE [App::DocumentObjectGroupPython] H_element114  label="H_element : 063"  # scripted group (container) (typed FeaturePython)
  n = 2
  ref = H_element
FEATURE [App::DocumentObjectGroupPython] G4_lH2  # scripted group (container) (typed FeaturePython)
  Dunit = g/cm3
  Dvalue = 0.0708
  Group = -> [H_element114]
  conduct = 2
  density = 1
  expand = 3
  formula = G4_lH2
  name = G4_lH2
  specific = 4
FEATURE [App::DocumentObjectGroupPython] N_element049  label="N_element : 022"  # scripted group (container) (typed FeaturePython)
  n = 2
  ref = N_element
FEATURE [App::DocumentObjectGroupPython] G4_lN2  # scripted group (container) (typed FeaturePython)
  Dunit = g/cm3
  Dvalue = 0.807
  Group = -> [N_element049]
  conduct = 2
  density = 1
  expand = 3
  formula = G4_lN2
  name = G4_lN2
  specific = 4
FEATURE [App::DocumentObjectGroupPython] O_element106  label="O_element : 060"  # scripted group (container) (typed FeaturePython)
  n = 2
  ref = O_element
FEATURE [App::DocumentObjectGroupPython] G4_lO2  # scripted group (container) (typed FeaturePython)
  Dunit = g/cm3
  Dvalue = 1.141
  Group = -> [O_element106]
  conduct = 2
  density = 1
  expand = 3
  formula = G4_lO2
  name = G4_lO2
  specific = 4
FEATURE [App::DocumentObjectGroupPython] Ar  label="Ar : 1"  # scripted group (container) (typed FeaturePython)
  n = 1
  ref = Ar
FEATURE [App::DocumentObjectGroupPython] G4_lAr  # scripted group (container) (typed FeaturePython)
  Dunit = g/cm3
  Dvalue = 1.396
  Group = -> [Ar]
  conduct = 2
  density = 1
  expand = 3
  formula = G4_lAr
  name = G4_lAr
  specific = 4
FEATURE [App::DocumentObjectGroupPython] Br  label="Br : 1"  # scripted group (container) (typed FeaturePython)
  n = 1
  ref = Br
FEATURE [App::DocumentObjectGroupPython] G4_lBr  # scripted group (container) (typed FeaturePython)
  Dunit = g/cm3
  Dvalue = 3.1028
  Group = -> [Br]
  conduct = 2
  density = 1
  expand = 3
  formula = G4_lBr
  name = G4_lBr
  specific = 4
FEATURE [App::DocumentObjectGroupPython] Kr  label="Kr : 1"  # scripted group (container) (typed FeaturePython)
  n = 1
  ref = Kr
FEATURE [App::DocumentObjectGroupPython] G4_lKr  # scripted group (container) (typed FeaturePython)
  Dunit = g/cm3
  Dvalue = 2.418
  Group = -> [Kr]
  conduct = 2
  density = 1
  expand = 3
  formula = G4_lKr
  name = G4_lKr
  specific = 4
FEATURE [App::DocumentObjectGroupPython] Xe  label="Xe : 1"  # scripted group (container) (typed FeaturePython)
  n = 1
  ref = Xe
FEATURE [App::DocumentObjectGroupPython] G4_lXe  # scripted group (container) (typed FeaturePython)
  Dunit = g/cm3
  Dvalue = 2.953
  Group = -> [Xe]
  conduct = 2
  density = 1
  expand = 3
  formula = G4_lXe
  name = G4_lXe
  specific = 4
FEATURE [App::DocumentObjectGroupPython] O_element107  label="O_element : 061"  # scripted group (container) (typed FeaturePython)
  n = 4
  ref = O_element
FEATURE [App::DocumentObjectGroupPython] Pb_element004  label="Pb_element : 002"  # scripted group (container) (typed FeaturePython)
  n = 1
  ref = Pb_element
FEATURE [App::DocumentObjectGroupPython] W_element005  label="W_element : 005"  # scripted group (container) (typed FeaturePython)
  n = 1
  ref = W_element
FEATURE [App::DocumentObjectGroupPython] G4_PbWO4  # scripted group (container) (typed FeaturePython)
  Dunit = g/cm3
  Dvalue = 8.28
  Group = -> [O_element107,Pb_element004,W_element005]
  conduct = 2
  density = 1
  expand = 3
  formula = G4_PbWO4
  name = G4_PbWO4
  specific = 4
FEATURE [App::DocumentObjectGroupPython] alactic  label="alactic : 1"  # scripted group (container) (typed FeaturePython)
  n = 1
  ref = alactic
FEATURE [App::DocumentObjectGroupPython] G4_Galactic  # scripted group (container) (typed FeaturePython)
  Dunit = g/cm3
  Dvalue = 0
  Group = -> [alactic]
  conduct = 2
  density = 1
  expand = 3
  formula = G4_Galactic
  name = G4_Galactic
  specific = 4
FEATURE [App::DocumentObjectGroupPython] RAPHITE_POROUS  label="RAPHITE_POROUS : 1"  # scripted group (container) (typed FeaturePython)
  n = 1
  ref = RAPHITE_POROUS
FEATURE [App::DocumentObjectGroupPython] G4_GRAPHITE_POROUS  # scripted group (container) (typed FeaturePython)
  Dunit = g/cm3
  Dvalue = 1.7
  Group = -> [RAPHITE_POROUS]
  conduct = 2
  density = 1
  expand = 3
  formula = G4_GRAPHITE_POROUS
  name = G4_GRAPHITE_POROUS
  specific = 4
FEATURE [App::DocumentObjectGroupPython] H_element115  label="H_element : 0.150"  # scripted group (container) (typed FeaturePython)
  n = 0.080538
FEATURE [App::DocumentObjectGroupPython] C_element125  label="C_element : 0.600"  # scripted group (container) (typed FeaturePython)
  n = 0.599848
FEATURE [App::DocumentObjectGroupPython] O_element108  label="O_element : 0.320"  # scripted group (container) (typed FeaturePython)
  n = 0.319614
FEATURE [App::DocumentObjectGroupPython] G4_LUCITE  # scripted group (container) (typed FeaturePython)
  Dunit = g/cm3
  Dvalue = 1.19
  Group = -> [H_element115,C_element125,O_element108]
  conduct = 2
  density = 1
  expand = 3
  formula = G4_LUCITE
  name = G4_LUCITE
  specific = 4
FEATURE [App::DocumentObjectGroupPython] Cu_element002  label="Cu_element : 62"  # scripted group (container) (typed FeaturePython)
  n = 62
  ref = Cu_element
FEATURE [App::DocumentObjectGroupPython] Zn_element002  label="Zn_element : 35"  # scripted group (container) (typed FeaturePython)
  n = 35
  ref = Zn_element
FEATURE [App::DocumentObjectGroupPython] Pb_element005  label="Pb_element : 3"  # scripted group (container) (typed FeaturePython)
  n = 3
  ref = Pb_element
FEATURE [App::DocumentObjectGroupPython] G4_BRASS  # scripted group (container) (typed FeaturePython)
  Dunit = g/cm3
  Dvalue = 8.52
  Group = -> [Cu_element002,Zn_element002,Pb_element005]
  conduct = 2
  density = 1
  expand = 3
  formula = G4_BRASS
  name = G4_BRASS
  specific = 4
FEATURE [App::DocumentObjectGroupPython] Cu_element003  label="Cu_element : 89"  # scripted group (container) (typed FeaturePython)
  n = 89
  ref = Cu_element
FEATURE [App::DocumentObjectGroupPython] Zn_element003  label="Zn_element : 9"  # scripted group (container) (typed FeaturePython)
  n = 9
  ref = Zn_element
FEATURE [App::DocumentObjectGroupPython] Pb_element006  label="Pb_element : 2"  # scripted group (container) (typed FeaturePython)
  n = 2
  ref = Pb_element
FEATURE [App::DocumentObjectGroupPython] G4_BRONZE  # scripted group (container) (typed FeaturePython)
  Dunit = g/cm3
  Dvalue = 8.82
  Group = -> [Cu_element003,Zn_element003,Pb_element006]
  conduct = 2
  density = 1
  expand = 3
  formula = G4_BRONZE
  name = G4_BRONZE
  specific = 4
FEATURE [App::DocumentObjectGroupPython] Fe_element008  label="Fe_element : 74"  # scripted group (container) (typed FeaturePython)
  n = 74
  ref = Fe_element
FEATURE [App::DocumentObjectGroupPython] Cr_element002  label="Cr_element : 18"  # scripted group (container) (typed FeaturePython)
  n = 18
  ref = Cr_element
FEATURE [App::DocumentObjectGroupPython] Ni_element002  label="Ni_element : 8"  # scripted group (container) (typed FeaturePython)
  n = 8
  ref = Ni_element
FEATURE [App::DocumentObjectGroupPython] G4_STAINLESS_STEEL  label="G4_STAINLESS-STEEL"  # scripted group (container) (typed FeaturePython)
  Dunit = g/cm3
  Dvalue = 8
  Group = -> [Fe_element008,Cr_element002,Ni_element002]
  conduct = 2
  density = 1
  expand = 3
  formula = G4_STAINLESS-STEEL
  name = G4_STAINLESS-STEEL
  specific = 4
FEATURE [App::DocumentObjectGroupPython] H_element116  label="H_element : 064"  # scripted group (container) (typed FeaturePython)
  n = 18
  ref = H_element
FEATURE [App::DocumentObjectGroupPython] C_element126  label="C_element : 071"  # scripted group (container) (typed FeaturePython)
  n = 12
  ref = C_element
FEATURE [App::DocumentObjectGroupPython] O_element109  label="O_element : 062"  # scripted group (container) (typed FeaturePython)
  n = 7
  ref = O_element
FEATURE [App::DocumentObjectGroupPython] G4_CR39  # scripted group (container) (typed FeaturePython)
  Dunit = g/cm3
  Dvalue = 1.32
  Group = -> [H_element116,C_element126,O_element109]
  conduct = 2
  density = 1
  expand = 3
  formula = G4_CR39
  name = G4_CR39
  specific = 4
FEATURE [App::DocumentObjectGroupPython] H_element117  label="H_element : 38"  # scripted group (container) (typed FeaturePython)
  n = 38
  ref = H_element
FEATURE [App::DocumentObjectGroupPython] C_element127  label="C_element : 072"  # scripted group (container) (typed FeaturePython)
  n = 18
  ref = C_element
FEATURE [App::DocumentObjectGroupPython] O_element110  label="O_element : 063"  # scripted group (container) (typed FeaturePython)
  n = 1
  ref = O_element
FEATURE [App::DocumentObjectGroupPython] G4_OCTADECANOL  # scripted group (container) (typed FeaturePython)
  Dunit = g/cm3
  Dvalue = 0.812
  Group = -> [H_element117,C_element127,O_element110]
  conduct = 2
  density = 1
  expand = 3
  formula = G4_OCTADECANOL
  name = G4_OCTADECANOL
  specific = 4
FEATURE [App::DocumentObjectGroupPython] HEP  # scripted group (container) (typed FeaturePython)
  Group = -> [G4_lH2,G4_lN2,G4_lO2,G4_lAr,G4_lBr,G4_lKr,G4_lXe,G4_PbWO4,G4_Galactic,G4_GRAPHITE_POROUS,G4_LUCITE,G4_BRASS,G4_BRONZE,G4_STAINLESS_STEEL,G4_CR39,G4_OCTADECANOL]
FEATURE [App::DocumentObjectGroupPython] C_element128  label="C_element : 073"  # scripted group (container) (typed FeaturePython)
  n = 14
  ref = C_element
FEATURE [App::DocumentObjectGroupPython] H_element118  label="H_element : 065"  # scripted group (container) (typed FeaturePython)
  n = 10
  ref = H_element
FEATURE [App::DocumentObjectGroupPython] O_element111  label="O_element : 064"  # scripted group (container) (typed FeaturePython)
  n = 2
  ref = O_element
FEATURE [App::DocumentObjectGroupPython] N_element050  label="N_element : 023"  # scripted group (container) (typed FeaturePython)
  n = 2
  ref = N_element
FEATURE [App::DocumentObjectGroupPython] G4_KEVLAR  # scripted group (container) (typed FeaturePython)
  Dunit = g/cm3
  Dvalue = 1.44
  Group = -> [C_element128,H_element118,O_element111,N_element050]
  conduct = 2
  density = 1
  expand = 3
  formula = G4_KEVLAR
  name = G4_KEVLAR
  specific = 4
FEATURE [App::DocumentObjectGroupPython] C_element129  label="C_element : 074"  # scripted group (container) (typed FeaturePython)
  n = 10
  ref = C_element
FEATURE [App::DocumentObjectGroupPython] H_element119  label="H_element : 066"  # scripted group (container) (typed FeaturePython)
  n = 8
  ref = H_element
FEATURE [App::DocumentObjectGroupPython] O_element112  label="O_element : 065"  # scripted group (container) (typed FeaturePython)
  n = 4
  ref = O_element
FEATURE [App::DocumentObjectGroupPython] G4_DACRON  # scripted group (container) (typed FeaturePython)
  Dunit = g/cm3
  Dvalue = 1.4
  Group = -> [C_element129,H_element119,O_element112]
  conduct = 2
  density = 1
  expand = 3
  formula = G4_DACRON
  name = G4_DACRON
  specific = 4
FEATURE [App::DocumentObjectGroupPython] C_element130  label="C_element : 075"  # scripted group (container) (typed FeaturePython)
  n = 4
  ref = C_element
FEATURE [App::DocumentObjectGroupPython] H_element120  label="H_element : 067"  # scripted group (container) (typed FeaturePython)
  n = 5
  ref = H_element
FEATURE [App::DocumentObjectGroupPython] Cl_element030  label="Cl_element : 016"  # scripted group (container) (typed FeaturePython)
  n = 1
  ref = Cl_element
FEATURE [App::DocumentObjectGroupPython] G4_NEOPRENE  # scripted group (container) (typed FeaturePython)
  Dunit = g/cm3
  Dvalue = 1.23
  Group = -> [C_element130,H_element120,Cl_element030]
  conduct = 2
  density = 1
  expand = 3
  formula = G4_NEOPRENE
  name = G4_NEOPRENE
  specific = 4
FEATURE [App::DocumentObjectGroupPython] Space  # scripted group (container) (typed FeaturePython)
  Group = -> [G4_KEVLAR,G4_DACRON,G4_NEOPRENE]
FEATURE [App::DocumentObjectGroupPython] H_element121  label="H_element : 068"  # scripted group (container) (typed FeaturePython)
  n = 5
  ref = H_element
FEATURE [App::DocumentObjectGroupPython] C_element131  label="C_element : 076"  # scripted group (container) (typed FeaturePython)
  n = 4
  ref = C_element
FEATURE [App::DocumentObjectGroupPython] N_element051  label="N_element : 3"  # scripted group (container) (typed FeaturePython)
  n = 3
  ref = N_element
FEATURE [App::DocumentObjectGroupPython] O_element113  label="O_element : 066"  # scripted group (container) (typed FeaturePython)
  n = 1
  ref = O_element
FEATURE [App::DocumentObjectGroupPython] G4_CYTOSINE  # scripted group (container) (typed FeaturePython)
  Dunit = g/cm3
  Dvalue = 1.55
  Group = -> [H_element121,C_element131,N_element051,O_element113]
  conduct = 2
  density = 1
  expand = 3
  formula = G4_CYTOSINE
  name = G4_CYTOSINE
  specific = 4
FEATURE [App::DocumentObjectGroupPython] H_element122  label="H_element : 069"  # scripted group (container) (typed FeaturePython)
  n = 6
  ref = H_element
FEATURE [App::DocumentObjectGroupPython] C_element132  label="C_element : 077"  # scripted group (container) (typed FeaturePython)
  n = 5
  ref = C_element
FEATURE [App::DocumentObjectGroupPython] N_element052  label="N_element : 024"  # scripted group (container) (typed FeaturePython)
  n = 2
  ref = N_element
FEATURE [App::DocumentObjectGroupPython] O_element114  label="O_element : 067"  # scripted group (container) (typed FeaturePython)
  n = 2
  ref = O_element
FEATURE [App::DocumentObjectGroupPython] G4_THYMINE  # scripted group (container) (typed FeaturePython)
  Dunit = g/cm3
  Dvalue = 1.23
  Group = -> [H_element122,C_element132,N_element052,O_element114]
  conduct = 2
  density = 1
  expand = 3
  formula = G4_THYMINE
  name = G4_THYMINE
  specific = 4
FEATURE [App::DocumentObjectGroupPython] H_element123  label="H_element : 070"  # scripted group (container) (typed FeaturePython)
  n = 4
  ref = H_element
FEATURE [App::DocumentObjectGroupPython] C_element133  label="C_element : 078"  # scripted group (container) (typed FeaturePython)
  n = 4
  ref = C_element
FEATURE [App::DocumentObjectGroupPython] N_element053  label="N_element : 025"  # scripted group (container) (typed FeaturePython)
  n = 2
  ref = N_element
FEATURE [App::DocumentObjectGroupPython] O_element115  label="O_element : 068"  # scripted group (container) (typed FeaturePython)
  n = 2
  ref = O_element
FEATURE [App::DocumentObjectGroupPython] G4_URACIL  # scripted group (container) (typed FeaturePython)
  Dunit = g/cm3
  Dvalue = 1.32
  Group = -> [H_element123,C_element133,N_element053,O_element115]
  conduct = 2
  density = 1
  expand = 3
  formula = G4_URACIL
  name = G4_URACIL
  specific = 4
FEATURE [App::DocumentObjectGroupPython] H_element124  label="H_element : 071"  # scripted group (container) (typed FeaturePython)
  n = 4
  ref = H_element
FEATURE [App::DocumentObjectGroupPython] C_element134  label="C_element : 079"  # scripted group (container) (typed FeaturePython)
  n = 5
  ref = C_element
FEATURE [App::DocumentObjectGroupPython] N_element054  label="N_element : 026"  # scripted group (container) (typed FeaturePython)
  n = 5
  ref = N_element
FEATURE [App::DocumentObjectGroupPython] G4_DNA_ADENINE  # scripted group (container) (typed FeaturePython)
  Dunit = g/cm3
  Dvalue = 1
  Group = -> [H_element124,C_element134,N_element054]
  conduct = 2
  density = 1
  expand = 3
  formula = G4_DNA_ADENINE
  name = G4_DNA_ADENINE
  specific = 4
FEATURE [App::DocumentObjectGroupPython] H_element125  label="H_element : 072"  # scripted group (container) (typed FeaturePython)
  n = 4
  ref = H_element
FEATURE [App::DocumentObjectGroupPython] C_element135  label="C_element : 080"  # scripted group (container) (typed FeaturePython)
  n = 5
  ref = C_element
FEATURE [App::DocumentObjectGroupPython] N_element055  label="N_element : 027"  # scripted group (container) (typed FeaturePython)
  n = 5
  ref = N_element
FEATURE [App::DocumentObjectGroupPython] O_element116  label="O_element : 069"  # scripted group (container) (typed FeaturePython)
  n = 1
  ref = O_element
FEATURE [App::DocumentObjectGroupPython] G4_DNA_GUANINE  # scripted group (container) (typed FeaturePython)
  Dunit = g/cm3
  Dvalue = 1
  Group = -> [H_element125,C_element135,N_element055,O_element116]
  conduct = 2
  density = 1
  expand = 3
  formula = G4_DNA_GUANINE
  name = G4_DNA_GUANINE
  specific = 4
FEATURE [App::DocumentObjectGroupPython] H_element126  label="H_element : 073"  # scripted group (container) (typed FeaturePython)
  n = 4
  ref = H_element
FEATURE [App::DocumentObjectGroupPython] C_element136  label="C_element : 081"  # scripted group (container) (typed FeaturePython)
  n = 4
  ref = C_element
FEATURE [App::DocumentObjectGroupPython] N_element056  label="N_element : 028"  # scripted group (container) (typed FeaturePython)
  n = 3
  ref = N_element
FEATURE [App::DocumentObjectGroupPython] O_element117  label="O_element : 070"  # scripted group (container) (typed FeaturePython)
  n = 1
  ref = O_element
FEATURE [App::DocumentObjectGroupPython] G4_DNA_CYTOSINE  # scripted group (container) (typed FeaturePython)
  Dunit = g/cm3
  Dvalue = 1
  Group = -> [H_element126,C_element136,N_element056,O_element117]
  conduct = 2
  density = 1
  expand = 3
  formula = G4_DNA_CYTOSINE
  name = G4_DNA_CYTOSINE
  specific = 4
FEATURE [App::DocumentObjectGroupPython] H_element127  label="H_element : 074"  # scripted group (container) (typed FeaturePython)
  n = 5
  ref = H_element
FEATURE [App::DocumentObjectGroupPython] C_element137  label="C_element : 082"  # scripted group (container) (typed FeaturePython)
  n = 5
  ref = C_element
FEATURE [App::DocumentObjectGroupPython] N_element057  label="N_element : 029"  # scripted group (container) (typed FeaturePython)
  n = 2
  ref = N_element
FEATURE [App::DocumentObjectGroupPython] O_element118  label="O_element : 071"  # scripted group (container) (typed FeaturePython)
  n = 2
  ref = O_element
FEATURE [App::DocumentObjectGroupPython] G4_DNA_THYMINE  # scripted group (container) (typed FeaturePython)
  Dunit = g/cm3
  Dvalue = 1
  Group = -> [H_element127,C_element137,N_element057,O_element118]
  conduct = 2
  density = 1
  expand = 3
  formula = G4_DNA_THYMINE
  name = G4_DNA_THYMINE
  specific = 4
FEATURE [App::DocumentObjectGroupPython] H_element128  label="H_element : 075"  # scripted group (container) (typed FeaturePython)
  n = 3
  ref = H_element
FEATURE [App::DocumentObjectGroupPython] C_element138  label="C_element : 083"  # scripted group (container) (typed FeaturePython)
  n = 4
  ref = C_element
FEATURE [App::DocumentObjectGroupPython] N_element058  label="N_element : 030"  # scripted group (container) (typed FeaturePython)
  n = 2
  ref = N_element
FEATURE [App::DocumentObjectGroupPython] O_element119  label="O_element : 072"  # scripted group (container) (typed FeaturePython)
  n = 2
  ref = O_element
FEATURE [App::DocumentObjectGroupPython] G4_DNA_URACIL  # scripted group (container) (typed FeaturePython)
  Dunit = g/cm3
  Dvalue = 1
  Group = -> [H_element128,C_element138,N_element058,O_element119]
  conduct = 2
  density = 1
  expand = 3
  formula = G4_DNA_URACIL
  name = G4_DNA_URACIL
  specific = 4
FEATURE [App::DocumentObjectGroupPython] H_element129  label="H_element : 076"  # scripted group (container) (typed FeaturePython)
  n = 10
  ref = H_element
FEATURE [App::DocumentObjectGroupPython] C_element139  label="C_element : 084"  # scripted group (container) (typed FeaturePython)
  n = 10
  ref = C_element
FEATURE [App::DocumentObjectGroupPython] N_element059  label="N_element : 031"  # scripted group (container) (typed FeaturePython)
  n = 5
  ref = N_element
FEATURE [App::DocumentObjectGroupPython] O_element120  label="O_element : 073"  # scripted group (container) (typed FeaturePython)
  n = 4
  ref = O_element
FEATURE [App::DocumentObjectGroupPython] G4_DNA_ADENOSINE  # scripted group (container) (typed FeaturePython)
  Dunit = g/cm3
  Dvalue = 1
  Group = -> [H_element129,C_element139,N_element059,O_element120]
  conduct = 2
  density = 1
  expand = 3
  formula = G4_DNA_ADENOSINE
  name = G4_DNA_ADENOSINE
  specific = 4
FEATURE [App::DocumentObjectGroupPython] H_element130  label="H_element : 077"  # scripted group (container) (typed FeaturePython)
  n = 10
  ref = H_element
FEATURE [App::DocumentObjectGroupPython] C_element140  label="C_element : 085"  # scripted group (container) (typed FeaturePython)
  n = 10
  ref = C_element
FEATURE [App::DocumentObjectGroupPython] N_element060  label="N_element : 032"  # scripted group (container) (typed FeaturePython)
  n = 5
  ref = N_element
FEATURE [App::DocumentObjectGroupPython] O_element121  label="O_element : 074"  # scripted group (container) (typed FeaturePython)
  n = 5
  ref = O_element
FEATURE [App::DocumentObjectGroupPython] G4_DNA_GUANOSINE  # scripted group (container) (typed FeaturePython)
  Dunit = g/cm3
  Dvalue = 1
  Group = -> [H_element130,C_element140,N_element060,O_element121]
  conduct = 2
  density = 1
  expand = 3
  formula = G4_DNA_GUANOSINE
  name = G4_DNA_GUANOSINE
  specific = 4
FEATURE [App::DocumentObjectGroupPython] H_element131  label="H_element : 078"  # scripted group (container) (typed FeaturePython)
  n = 10
  ref = H_element
FEATURE [App::DocumentObjectGroupPython] C_element141  label="C_element : 086"  # scripted group (container) (typed FeaturePython)
  n = 9
  ref = C_element
FEATURE [App::DocumentObjectGroupPython] N_element061  label="N_element : 033"  # scripted group (container) (typed FeaturePython)
  n = 3
  ref = N_element
FEATURE [App::DocumentObjectGroupPython] O_element122  label="O_element : 075"  # scripted group (container) (typed FeaturePython)
  n = 5
  ref = O_element
FEATURE [App::DocumentObjectGroupPython] G4_DNA_CYTIDINE  # scripted group (container) (typed FeaturePython)
  Dunit = g/cm3
  Dvalue = 1
  Group = -> [H_element131,C_element141,N_element061,O_element122]
  conduct = 2
  density = 1
  expand = 3
  formula = G4_DNA_CYTIDINE
  name = G4_DNA_CYTIDINE
  specific = 4
FEATURE [App::DocumentObjectGroupPython] H_element132  label="H_element : 079"  # scripted group (container) (typed FeaturePython)
  n = 9
  ref = H_element
FEATURE [App::DocumentObjectGroupPython] C_element142  label="C_element : 087"  # scripted group (container) (typed FeaturePython)
  n = 9
  ref = C_element
FEATURE [App::DocumentObjectGroupPython] N_element062  label="N_element : 034"  # scripted group (container) (typed FeaturePython)
  n = 2
  ref = N_element
FEATURE [App::DocumentObjectGroupPython] O_element123  label="O_element : 076"  # scripted group (container) (typed FeaturePython)
  n = 6
  ref = O_element
FEATURE [App::DocumentObjectGroupPython] G4_DNA_URIDINE  # scripted group (container) (typed FeaturePython)
  Dunit = g/cm3
  Dvalue = 1
  Group = -> [H_element132,C_element142,N_element062,O_element123]
  conduct = 2
  density = 1
  expand = 3
  formula = G4_DNA_URIDINE
  name = G4_DNA_URIDINE
  specific = 4
FEATURE [App::DocumentObjectGroupPython] H_element133  label="H_element : 080"  # scripted group (container) (typed FeaturePython)
  n = 11
  ref = H_element
FEATURE [App::DocumentObjectGroupPython] C_element143  label="C_element : 088"  # scripted group (container) (typed FeaturePython)
  n = 10
  ref = C_element
FEATURE [App::DocumentObjectGroupPython] N_element063  label="N_element : 035"  # scripted group (container) (typed FeaturePython)
  n = 2
  ref = N_element
FEATURE [App::DocumentObjectGroupPython] O_element124  label="O_element : 077"  # scripted group (container) (typed FeaturePython)
  n = 6
  ref = O_element
FEATURE [App::DocumentObjectGroupPython] G4_DNA_METHYLURIDINE  # scripted group (container) (typed FeaturePython)
  Dunit = g/cm3
  Dvalue = 1
  Group = -> [H_element133,C_element143,N_element063,O_element124]
  conduct = 2
  density = 1
  expand = 3
  formula = G4_DNA_METHYLURIDINE
  name = G4_DNA_METHYLURIDINE
  specific = 4
FEATURE [App::DocumentObjectGroupPython] P_element014  label="P_element : 003"  # scripted group (container) (typed FeaturePython)
  n = 1
  ref = P_element
FEATURE [App::DocumentObjectGroupPython] O_element125  label="O_element : 078"  # scripted group (container) (typed FeaturePython)
  n = 3
  ref = O_element
FEATURE [App::DocumentObjectGroupPython] G4_DNA_MONOPHOSPHATE  # scripted group (container) (typed FeaturePython)
  Dunit = g/cm3
  Dvalue = 1
  Group = -> [P_element014,O_element125]
  conduct = 2
  density = 1
  expand = 3
  formula = G4_DNA_MONOPHOSPHATE
  name = G4_DNA_MONOPHOSPHATE
  specific = 4
FEATURE [App::DocumentObjectGroupPython] H_element134  label="H_element : 081"  # scripted group (container) (typed FeaturePython)
  n = 10
  ref = H_element
FEATURE [App::DocumentObjectGroupPython] C_element144  label="C_element : 089"  # scripted group (container) (typed FeaturePython)
  n = 10
  ref = C_element
FEATURE [App::DocumentObjectGroupPython] N_element064  label="N_element : 036"  # scripted group (container) (typed FeaturePython)
  n = 5
  ref = N_element
FEATURE [App::DocumentObjectGroupPython] O_element126  label="O_element : 079"  # scripted group (container) (typed FeaturePython)
  n = 7
  ref = O_element
FEATURE [App::DocumentObjectGroupPython] P_element015  label="P_element : 004"  # scripted group (container) (typed FeaturePython)
  n = 1
  ref = P_element
FEATURE [App::DocumentObjectGroupPython] G4_DNA_A  # scripted group (container) (typed FeaturePython)
  Dunit = g/cm3
  Dvalue = 1
  Group = -> [H_element134,C_element144,N_element064,O_element126,P_element015]
  conduct = 2
  density = 1
  expand = 3
  formula = G4_DNA_A
  name = G4_DNA_A
  specific = 4
FEATURE [App::DocumentObjectGroupPython] H_element135  label="H_element : 082"  # scripted group (container) (typed FeaturePython)
  n = 10
  ref = H_element
FEATURE [App::DocumentObjectGroupPython] C_element145  label="C_element : 090"  # scripted group (container) (typed FeaturePython)
  n = 10
  ref = C_element
FEATURE [App::DocumentObjectGroupPython] N_element065  label="N_element : 037"  # scripted group (container) (typed FeaturePython)
  n = 5
  ref = N_element
FEATURE [App::DocumentObjectGroupPython] O_element127  label="O_element : 8"  # scripted group (container) (typed FeaturePython)
  n = 8
  ref = O_element
FEATURE [App::DocumentObjectGroupPython] P_element016  label="P_element : 005"  # scripted group (container) (typed FeaturePython)
  n = 1
  ref = P_element
FEATURE [App::DocumentObjectGroupPython] G4_DNA_G  # scripted group (container) (typed FeaturePython)
  Dunit = g/cm3
  Dvalue = 1
  Group = -> [H_element135,C_element145,N_element065,O_element127,P_element016]
  conduct = 2
  density = 1
  expand = 3
  formula = G4_DNA_G
  name = G4_DNA_G
  specific = 4
FEATURE [App::DocumentObjectGroupPython] H_element136  label="H_element : 083"  # scripted group (container) (typed FeaturePython)
  n = 10
  ref = H_element
FEATURE [App::DocumentObjectGroupPython] C_element146  label="C_element : 091"  # scripted group (container) (typed FeaturePython)
  n = 9
  ref = C_element
FEATURE [App::DocumentObjectGroupPython] N_element066  label="N_element : 038"  # scripted group (container) (typed FeaturePython)
  n = 3
  ref = N_element
FEATURE [App::DocumentObjectGroupPython] O_element128  label="O_element : 080"  # scripted group (container) (typed FeaturePython)
  n = 8
  ref = O_element
FEATURE [App::DocumentObjectGroupPython] P_element017  label="P_element : 006"  # scripted group (container) (typed FeaturePython)
  n = 1
  ref = P_element
FEATURE [App::DocumentObjectGroupPython] G4_DNA_C  # scripted group (container) (typed FeaturePython)
  Dunit = g/cm3
  Dvalue = 1
  Group = -> [H_element136,C_element146,N_element066,O_element128,P_element017]
  conduct = 2
  density = 1
  expand = 3
  formula = G4_DNA_C
  name = G4_DNA_C
  specific = 4
FEATURE [App::DocumentObjectGroupPython] H_element137  label="H_element : 084"  # scripted group (container) (typed FeaturePython)
  n = 9
  ref = H_element
FEATURE [App::DocumentObjectGroupPython] C_element147  label="C_element : 092"  # scripted group (container) (typed FeaturePython)
  n = 9
  ref = C_element
FEATURE [App::DocumentObjectGroupPython] N_element067  label="N_element : 039"  # scripted group (container) (typed FeaturePython)
  n = 2
  ref = N_element
FEATURE [App::DocumentObjectGroupPython] O_element129  label="O_element : 9"  # scripted group (container) (typed FeaturePython)
  n = 9
  ref = O_element
FEATURE [App::DocumentObjectGroupPython] P_element018  label="P_element : 007"  # scripted group (container) (typed FeaturePython)
  n = 1
  ref = P_element
FEATURE [App::DocumentObjectGroupPython] G4_DNA_U  # scripted group (container) (typed FeaturePython)
  Dunit = g/cm3
  Dvalue = 1
  Group = -> [H_element137,C_element147,N_element067,O_element129,P_element018]
  conduct = 2
  density = 1
  expand = 3
  formula = G4_DNA_U
  name = G4_DNA_U
  specific = 4
FEATURE [App::DocumentObjectGroupPython] H_element138  label="H_element : 085"  # scripted group (container) (typed FeaturePython)
  n = 11
  ref = H_element
FEATURE [App::DocumentObjectGroupPython] C_element148  label="C_element : 093"  # scripted group (container) (typed FeaturePython)
  n = 10
  ref = C_element
FEATURE [App::DocumentObjectGroupPython] N_element068  label="N_element : 040"  # scripted group (container) (typed FeaturePython)
  n = 2
  ref = N_element
FEATURE [App::DocumentObjectGroupPython] O_element130  label="O_element : 081"  # scripted group (container) (typed FeaturePython)
  n = 9
  ref = O_element
FEATURE [App::DocumentObjectGroupPython] P_element019  label="P_element : 008"  # scripted group (container) (typed FeaturePython)
  n = 1
  ref = P_element
FEATURE [App::DocumentObjectGroupPython] G4_DNA_MU  # scripted group (container) (typed FeaturePython)
  Dunit = g/cm3
  Dvalue = 1
  Group = -> [H_element138,C_element148,N_element068,O_element130,P_element019]
  conduct = 2
  density = 1
  expand = 3
  formula = G4_DNA_MU
  name = G4_DNA_MU
  specific = 4
FEATURE [App::DocumentObjectGroupPython] BioChemical  # scripted group (container) (typed FeaturePython)
  Group = -> [G4_CYTOSINE,G4_THYMINE,G4_URACIL,G4_DNA_ADENINE,G4_DNA_GUANINE,G4_DNA_CYTOSINE,G4_DNA_THYMINE,G4_DNA_URACIL,G4_DNA_ADENOSINE,G4_DNA_GUANOSINE,G4_DNA_CYTIDINE,G4_DNA_URIDINE,G4_DNA_METHYLURIDINE,G4_DNA_MONOPHOSPHATE,G4_DNA_A,G4_DNA_G,G4_DNA_C,G4_DNA_U,G4_DNA_MU]
FEATURE [App::DocumentObjectGroupPython] G4Materials  # scripted group (container) (typed FeaturePython)
  Group = -> [NIST,Element,HEP,Space,BioChemical]
  version = 1
FEATURE [App::DocumentObjectGroupPython] Geant4  # scripted group (container) (typed FeaturePython)
  Group = -> [G4Isotopes,G4Elements,G4Materials]
FEATURE [App::DocumentObjectGroupPython] Materials  # scripted group (container) (typed FeaturePython)
  Group = -> [Geant4]
FEATURE [Part::FeaturePython] GDMLBox_WorldBox  # WARN: FeaturePython — macro-defined, semantics opaque (R4)
  lunit = 2
  material = 5
  x = 273
  y = 273
  z = 130
FEATURE [Part::FeaturePython] GDMLBox_Box  # WARN: FeaturePython — macro-defined, semantics opaque (R4)
  lunit = 2
  material = 0
  x = 10
  y = 10
  z = 10
FEATURE [App::Part] LV_Box
  Group = -> [GDMLBox_Box]
  Origin = -> Origin002
FEATURE [Part::FeaturePython] Array  # Draft array (typed FeaturePython)
  AlwaysSyncPlacement = false
  Angle = 360
  ArrayType = 1
  Axis = (0,0,1)
  Base = -> LV_Box
  Center = (0,0,0)
  Count = 5
  ExpandArray = false
  Fuse = false
  IntervalAxis = (0,0,0)
  IntervalX = (100,0,0)
  IntervalY = (0,100,0)
  IntervalZ = (0,0,100)
  NumberCircles = 3
  NumberPolar = 5
  NumberX = 2
  NumberY = 2
  NumberZ = 1
  PlacementList = 5 placements: [(0,0,0),(0,0,0),(0,0,0),(0,0,0),(0,0,0)]
  RadialDistance = 50
  ScaleList = (5) [(1,1,1),(1,1,1),(1,1,1),(1,1,1),(1,1,1)]
  Symmetry = 1
  TangentialDistance = 25
FEATURE [App::Part] Part  label="experiment"
  Group = -> [LV_Box,Array]
  Origin = -> Origin001
FEATURE [App::Part] worldVOL
  Group = -> [GDMLBox_WorldBox,Part]
  Origin = -> Origin
